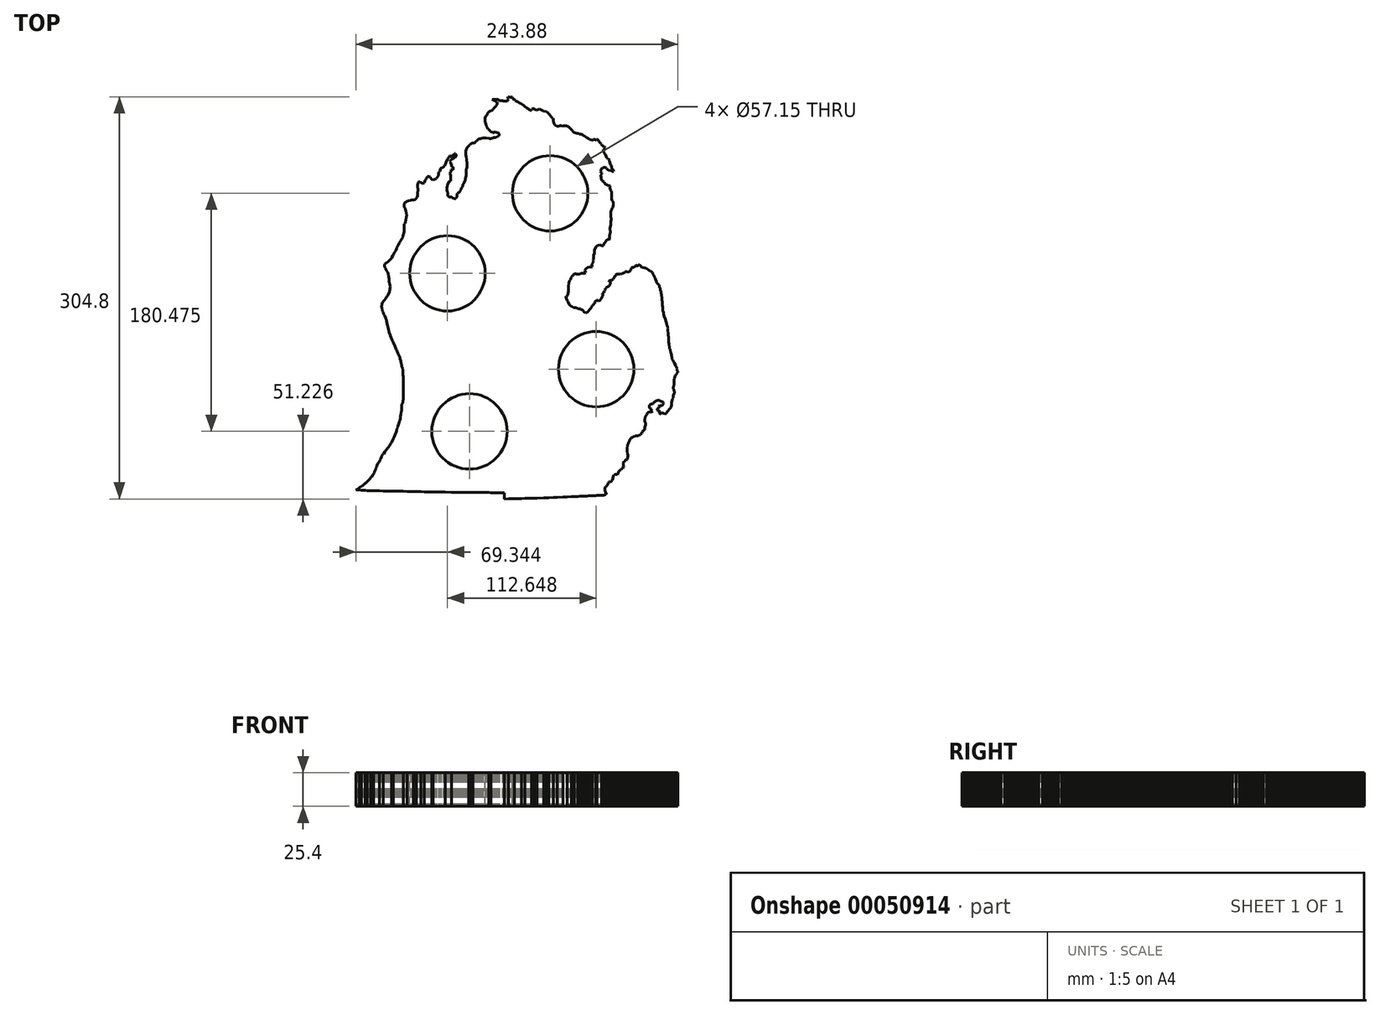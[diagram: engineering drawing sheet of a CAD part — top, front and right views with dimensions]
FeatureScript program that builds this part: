
annotation { "Feature Type Name" : "Feature", "Feature Type Description" : "" }
export const myFeature = defineFeature(function(context is Context, id is Id, definition is map)
    precondition{}
    {
        {
            var Q0;
            Q0=qCreatedBy(makeId("Top.planeOp"),FACE);
            var sketch = newSketch(context, id + "F0", { "sketchPlane" : qUnion([Q0])});
            skLineSegment(sketch, "E0", {"start": v(-98.47, -18.7) * mm, "end": v(-98.65, -17.82) * mm});
            skLineSegment(sketch, "E1", {"start": v(-98.65, -17.82) * mm, "end": v(-98.82, -17.3) * mm});
            skLineSegment(sketch, "E2", {"start": v(-98.82, -17.3) * mm, "end": v(-98.82, -16.95) * mm});
            skLineSegment(sketch, "E3", {"start": v(-98.82, -16.95) * mm, "end": v(-99.34, -15.56) * mm});
            skLineSegment(sketch, "E4", {"start": v(-99.34, -15.56) * mm, "end": v(-99.34, -15.39) * mm});
            skLineSegment(sketch, "E5", {"start": v(-99.34, -15.39) * mm, "end": v(-100.38, -13.13) * mm});
            skLineSegment(sketch, "E6", {"start": v(-100.38, -13.13) * mm, "end": v(-100.56, -12.6) * mm});
            skLineSegment(sketch, "E7", {"start": v(-100.56, -12.6) * mm, "end": v(-100.9, -12.08) * mm});
            skLineSegment(sketch, "E8", {"start": v(-100.9, -12.08) * mm, "end": v(-101.43, -10.87) * mm});
            skLineSegment(sketch, "E9", {"start": v(-101.43, -10.87) * mm, "end": v(-101.77, -9.82) * mm});
            skLineSegment(sketch, "E10", {"start": v(-101.77, -9.82) * mm, "end": v(-101.95, -9.65) * mm});
            skLineSegment(sketch, "E11", {"start": v(-101.95, -9.65) * mm, "end": v(-101.95, -9.48) * mm});
            skLineSegment(sketch, "E12", {"start": v(-101.95, -9.48) * mm, "end": v(-102.3, -7.74) * mm});
            skLineSegment(sketch, "E13", {"start": v(-102.3, -7.74) * mm, "end": v(-102.47, -6.7) * mm});
            skLineSegment(sketch, "E14", {"start": v(-102.47, -6.7) * mm, "end": v(-102.47, -6.52) * mm});
            skLineSegment(sketch, "E15", {"start": v(-102.47, -6.52) * mm, "end": v(-102.47, -6) * mm});
            skLineSegment(sketch, "E16", {"start": v(-102.47, -6) * mm, "end": v(-102.47, -5.83) * mm});
            skLineSegment(sketch, "E17", {"start": v(-102.47, -5.83) * mm, "end": v(-102.47, -5.65) * mm});
            skLineSegment(sketch, "E18", {"start": v(-102.47, -5.65) * mm, "end": v(-102.3, -5.65) * mm});
            skLineSegment(sketch, "E19", {"start": v(-102.3, -5.65) * mm, "end": v(-102.3, -4.96) * mm});
            skLineSegment(sketch, "E20", {"start": v(-102.3, -4.96) * mm, "end": v(-102.3, -4.78) * mm});
            skLineSegment(sketch, "E21", {"start": v(-102.3, -4.78) * mm, "end": v(-102.3, -4.6) * mm});
            skLineSegment(sketch, "E22", {"start": v(-102.3, -4.6) * mm, "end": v(-101.77, -3.4) * mm});
            skLineSegment(sketch, "E23", {"start": v(-101.77, -3.4) * mm, "end": v(-100.73, -1.83) * mm});
            skLineSegment(sketch, "E24", {"start": v(-100.73, -1.83) * mm, "end": v(-99, 0.09) * mm});
            skLineSegment(sketch, "E25", {"start": v(-99, 0.09) * mm, "end": v(-98.65, 0.78) * mm});
            skLineSegment(sketch, "E26", {"start": v(-98.65, 0.78) * mm, "end": v(-97.95, 1.65) * mm});
            skLineSegment(sketch, "E27", {"start": v(-97.95, 1.65) * mm, "end": v(-97.95, 1.83) * mm});
            skLineSegment(sketch, "E28", {"start": v(-97.95, 1.83) * mm, "end": v(-97.08, 3.4) * mm});
            skLineSegment(sketch, "E29", {"start": v(-97.08, 3.4) * mm, "end": v(-97.08, 3.56) * mm});
            skLineSegment(sketch, "E30", {"start": v(-97.08, 3.56) * mm, "end": v(-96.9, 3.56) * mm});
            skLineSegment(sketch, "E31", {"start": v(-96.9, 3.56) * mm, "end": v(-96.9, 3.74) * mm});
            skLineSegment(sketch, "E32", {"start": v(-96.9, 3.74) * mm, "end": v(-96.9, 3.91) * mm});
            skLineSegment(sketch, "E33", {"start": v(-96.9, 3.91) * mm, "end": v(-96.56, 4.78) * mm});
            skLineSegment(sketch, "E34", {"start": v(-96.56, 4.78) * mm, "end": v(-96.56, 4.96) * mm});
            skLineSegment(sketch, "E35", {"start": v(-96.56, 4.96) * mm, "end": v(-96.21, 6.7) * mm});
            skLineSegment(sketch, "E36", {"start": v(-96.21, 6.7) * mm, "end": v(-96.21, 6.87) * mm});
            skLineSegment(sketch, "E37", {"start": v(-96.21, 6.87) * mm, "end": v(-96.21, 7.04) * mm});
            skLineSegment(sketch, "E38", {"start": v(-96.21, 7.04) * mm, "end": v(-96.04, 8.6) * mm});
            skLineSegment(sketch, "E39", {"start": v(-96.04, 8.6) * mm, "end": v(-96.21, 9.82) * mm});
            skLineSegment(sketch, "E40", {"start": v(-96.21, 9.82) * mm, "end": v(-96.73, 12.26) * mm});
            skLineSegment(sketch, "E41", {"start": v(-96.73, 12.26) * mm, "end": v(-96.73, 12.43) * mm});
            skLineSegment(sketch, "E42", {"start": v(-96.73, 12.43) * mm, "end": v(-96.73, 13.13) * mm});
            skLineSegment(sketch, "E43", {"start": v(-96.73, 13.13) * mm, "end": v(-96.9, 14.52) * mm});
            skLineSegment(sketch, "E44", {"start": v(-96.9, 14.52) * mm, "end": v(-97.25, 16.08) * mm});
            skLineSegment(sketch, "E45", {"start": v(-97.25, 16.08) * mm, "end": v(-97.25, 16.6) * mm});
            skLineSegment(sketch, "E46", {"start": v(-97.25, 16.6) * mm, "end": v(-97.25, 16.95) * mm});
            skLineSegment(sketch, "E47", {"start": v(-97.25, 16.95) * mm, "end": v(-97.43, 17.47) * mm});
            skLineSegment(sketch, "E48", {"start": v(-97.43, 17.47) * mm, "end": v(-97.6, 18.34) * mm});
            skLineSegment(sketch, "E49", {"start": v(-97.6, 18.34) * mm, "end": v(-97.6, 18.52) * mm});
            skLineSegment(sketch, "E50", {"start": v(-97.6, 18.52) * mm, "end": v(-97.95, 19.39) * mm});
            skLineSegment(sketch, "E51", {"start": v(-97.95, 19.39) * mm, "end": v(-98.65, 20.6) * mm});
            skLineSegment(sketch, "E52", {"start": v(-98.65, 20.6) * mm, "end": v(-99.34, 22) * mm});
            skLineSegment(sketch, "E53", {"start": v(-99.34, 22) * mm, "end": v(-99.51, 22.17) * mm});
            skLineSegment(sketch, "E54", {"start": v(-99.51, 22.17) * mm, "end": v(-99.51, 22.34) * mm});
            skLineSegment(sketch, "E55", {"start": v(-99.51, 22.34) * mm, "end": v(-99.86, 22.86) * mm});
            skLineSegment(sketch, "E56", {"start": v(-99.86, 22.86) * mm, "end": v(-99.86, 23.04) * mm});
            skLineSegment(sketch, "E57", {"start": v(-99.86, 23.04) * mm, "end": v(-100.04, 23.21) * mm});
            skLineSegment(sketch, "E58", {"start": v(-100.04, 23.21) * mm, "end": v(-100.2, 24.26) * mm});
            skLineSegment(sketch, "E59", {"start": v(-100.2, 24.26) * mm, "end": v(-100.2, 24.95) * mm});
            skLineSegment(sketch, "E60", {"start": v(-100.2, 24.95) * mm, "end": v(-99.86, 25.65) * mm});
            skLineSegment(sketch, "E61", {"start": v(-99.86, 25.65) * mm, "end": v(-99.34, 26.17) * mm});
            skLineSegment(sketch, "E62", {"start": v(-99.34, 26.17) * mm, "end": v(-98.82, 26.69) * mm});
            skLineSegment(sketch, "E63", {"start": v(-98.82, 26.69) * mm, "end": v(-97.95, 27.21) * mm});
            skLineSegment(sketch, "E64", {"start": v(-97.95, 27.21) * mm, "end": v(-96.56, 28.43) * mm});
            skLineSegment(sketch, "E65", {"start": v(-96.56, 28.43) * mm, "end": v(-96.39, 28.43) * mm});
            skLineSegment(sketch, "E66", {"start": v(-96.39, 28.43) * mm, "end": v(-96.39, 28.6) * mm});
            skLineSegment(sketch, "E67", {"start": v(-96.39, 28.6) * mm, "end": v(-95.52, 29.47) * mm});
            skLineSegment(sketch, "E68", {"start": v(-95.52, 29.47) * mm, "end": v(-95, 30.17) * mm});
            skLineSegment(sketch, "E69", {"start": v(-95, 30.17) * mm, "end": v(-95, 30.34) * mm});
            skLineSegment(sketch, "E70", {"start": v(-95, 30.34) * mm, "end": v(-93.95, 32.08) * mm});
            skLineSegment(sketch, "E71", {"start": v(-93.95, 32.08) * mm, "end": v(-93.08, 33.82) * mm});
            skLineSegment(sketch, "E72", {"start": v(-93.08, 33.82) * mm, "end": v(-92.74, 34.51) * mm});
            skLineSegment(sketch, "E73", {"start": v(-92.74, 34.51) * mm, "end": v(-92.56, 34.69) * mm});
            skLineSegment(sketch, "E74", {"start": v(-92.56, 34.69) * mm, "end": v(-91.7, 35.9) * mm});
            skLineSegment(sketch, "E75", {"start": v(-91.7, 35.9) * mm, "end": v(-91.17, 37.47) * mm});
            skLineSegment(sketch, "E76", {"start": v(-91.17, 37.47) * mm, "end": v(-91, 38) * mm});
            skLineSegment(sketch, "E77", {"start": v(-91, 38) * mm, "end": v(-90.65, 39.03) * mm});
            skLineSegment(sketch, "E78", {"start": v(-90.65, 39.03) * mm, "end": v(-89.78, 39.9) * mm});
            skLineSegment(sketch, "E79", {"start": v(-89.78, 39.9) * mm, "end": v(-89.78, 40.08) * mm});
            skLineSegment(sketch, "E80", {"start": v(-89.78, 40.08) * mm, "end": v(-89.08, 41.47) * mm});
            skLineSegment(sketch, "E81", {"start": v(-89.08, 41.47) * mm, "end": v(-88.74, 42.34) * mm});
            skLineSegment(sketch, "E82", {"start": v(-88.74, 42.34) * mm, "end": v(-88.22, 43.2) * mm});
            skLineSegment(sketch, "E83", {"start": v(-88.22, 43.2) * mm, "end": v(-86.48, 45.99) * mm});
            skLineSegment(sketch, "E84", {"start": v(-86.48, 45.99) * mm, "end": v(-86.3, 46.86) * mm});
            skLineSegment(sketch, "E85", {"start": v(-86.3, 46.86) * mm, "end": v(-86.3, 47.03) * mm});
            skLineSegment(sketch, "E86", {"start": v(-86.3, 47.03) * mm, "end": v(-85.43, 50.16) * mm});
            skLineSegment(sketch, "E87", {"start": v(-85.43, 50.16) * mm, "end": v(-85.26, 51.55) * mm});
            skLineSegment(sketch, "E88", {"start": v(-85.26, 51.55) * mm, "end": v(-85.26, 52.07) * mm});
            skLineSegment(sketch, "E89", {"start": v(-85.26, 52.07) * mm, "end": v(-85.26, 52.42) * mm});
            skLineSegment(sketch, "E90", {"start": v(-85.26, 52.42) * mm, "end": v(-85.26, 52.6) * mm});
            skLineSegment(sketch, "E91", {"start": v(-85.26, 52.6) * mm, "end": v(-85.26, 52.77) * mm});
            skLineSegment(sketch, "E92", {"start": v(-85.26, 52.77) * mm, "end": v(-85.43, 53.81) * mm});
            skLineSegment(sketch, "E93", {"start": v(-85.43, 53.81) * mm, "end": v(-85.43, 54.16) * mm});
            skLineSegment(sketch, "E94", {"start": v(-85.43, 54.16) * mm, "end": v(-85.43, 54.68) * mm});
            skLineSegment(sketch, "E95", {"start": v(-85.43, 54.68) * mm, "end": v(-85.43, 54.86) * mm});
            skLineSegment(sketch, "E96", {"start": v(-85.43, 54.86) * mm, "end": v(-85.26, 55.03) * mm});
            skLineSegment(sketch, "E97", {"start": v(-85.26, 55.03) * mm, "end": v(-85.26, 55.2) * mm});
            skLineSegment(sketch, "E98", {"start": v(-85.26, 55.2) * mm, "end": v(-85.26, 56.25) * mm});
            skLineSegment(sketch, "E99", {"start": v(-85.26, 56.25) * mm, "end": v(-84.91, 56.6) * mm});
            skLineSegment(sketch, "E100", {"start": v(-84.91, 56.6) * mm, "end": v(-84.57, 57.47) * mm});
            skLineSegment(sketch, "E101", {"start": v(-84.57, 57.47) * mm, "end": v(-84.57, 57.64) * mm});
            skLineSegment(sketch, "E102", {"start": v(-84.57, 57.64) * mm, "end": v(-84.22, 58.86) * mm});
            skLineSegment(sketch, "E103", {"start": v(-84.22, 58.86) * mm, "end": v(-83.7, 61.12) * mm});
            skLineSegment(sketch, "E104", {"start": v(-83.7, 61.12) * mm, "end": v(-83.52, 62.5) * mm});
            skLineSegment(sketch, "E105", {"start": v(-83.52, 62.5) * mm, "end": v(-83.7, 64.25) * mm});
            skLineSegment(sketch, "E106", {"start": v(-83.7, 64.25) * mm, "end": v(-83.7, 64.42) * mm});
            skLineSegment(sketch, "E107", {"start": v(-83.7, 64.42) * mm, "end": v(-83.7, 64.6) * mm});
            skLineSegment(sketch, "E108", {"start": v(-83.7, 64.6) * mm, "end": v(-83.87, 64.94) * mm});
            skLineSegment(sketch, "E109", {"start": v(-83.87, 64.94) * mm, "end": v(-84.04, 65.29) * mm});
            skLineSegment(sketch, "E110", {"start": v(-84.04, 65.29) * mm, "end": v(-84.04, 65.64) * mm});
            skLineSegment(sketch, "E111", {"start": v(-84.04, 65.64) * mm, "end": v(-84.22, 65.81) * mm});
            skLineSegment(sketch, "E112", {"start": v(-84.22, 65.81) * mm, "end": v(-84.57, 67.2) * mm});
            skLineSegment(sketch, "E113", {"start": v(-84.57, 67.2) * mm, "end": v(-84.91, 67.9) * mm});
            skLineSegment(sketch, "E114", {"start": v(-84.91, 67.9) * mm, "end": v(-85.09, 68.25) * mm});
            skLineSegment(sketch, "E115", {"start": v(-85.09, 68.25) * mm, "end": v(-85.09, 68.6) * mm});
            skLineSegment(sketch, "E116", {"start": v(-85.09, 68.6) * mm, "end": v(-85.26, 69.29) * mm});
            skLineSegment(sketch, "E117", {"start": v(-85.26, 69.29) * mm, "end": v(-85.43, 69.64) * mm});
            skLineSegment(sketch, "E118", {"start": v(-85.43, 69.64) * mm, "end": v(-85.43, 69.8) * mm});
            skLineSegment(sketch, "E119", {"start": v(-85.43, 69.8) * mm, "end": v(-85.26, 70.68) * mm});
            skLineSegment(sketch, "E120", {"start": v(-85.26, 70.68) * mm, "end": v(-85.26, 71.38) * mm});
            skLineSegment(sketch, "E121", {"start": v(-85.26, 71.38) * mm, "end": v(-85.09, 71.72) * mm});
            skLineSegment(sketch, "E122", {"start": v(-85.09, 71.72) * mm, "end": v(-85.09, 71.9) * mm});
            skLineSegment(sketch, "E123", {"start": v(-85.09, 71.9) * mm, "end": v(-84.74, 72.24) * mm});
            skLineSegment(sketch, "E124", {"start": v(-84.74, 72.24) * mm, "end": v(-83.87, 72.77) * mm});
            skLineSegment(sketch, "E125", {"start": v(-83.87, 72.77) * mm, "end": v(-83.87, 72.94) * mm});
            skLineSegment(sketch, "E126", {"start": v(-83.87, 72.94) * mm, "end": v(-82.13, 73.46) * mm});
            skLineSegment(sketch, "E127", {"start": v(-82.13, 73.46) * mm, "end": v(-80.74, 73.8) * mm});
            skLineSegment(sketch, "E128", {"start": v(-80.74, 73.8) * mm, "end": v(-80.05, 74.33) * mm});
            skLineSegment(sketch, "E129", {"start": v(-80.05, 74.33) * mm, "end": v(-79.87, 74.33) * mm});
            skLineSegment(sketch, "E130", {"start": v(-79.87, 74.33) * mm, "end": v(-77.96, 74.33) * mm});
            skLineSegment(sketch, "E131", {"start": v(-77.96, 74.33) * mm, "end": v(-77.27, 74.5) * mm});
            skLineSegment(sketch, "E132", {"start": v(-77.27, 74.5) * mm, "end": v(-76.22, 75.2) * mm});
            skLineSegment(sketch, "E133", {"start": v(-76.22, 75.2) * mm, "end": v(-76.22, 75.37) * mm});
            skLineSegment(sketch, "E134", {"start": v(-76.22, 75.37) * mm, "end": v(-76.05, 75.9) * mm});
            skLineSegment(sketch, "E135", {"start": v(-76.05, 75.9) * mm, "end": v(-75.7, 76.6) * mm});
            skLineSegment(sketch, "E136", {"start": v(-75.7, 76.6) * mm, "end": v(-75.35, 77.29) * mm});
            skLineSegment(sketch, "E137", {"start": v(-75.35, 77.29) * mm, "end": v(-75.35, 77.98) * mm});
            skLineSegment(sketch, "E138", {"start": v(-75.35, 77.98) * mm, "end": v(-75.18, 79.9) * mm});
            skLineSegment(sketch, "E139", {"start": v(-75.18, 79.9) * mm, "end": v(-75, 81.11) * mm});
            skLineSegment(sketch, "E140", {"start": v(-75, 81.11) * mm, "end": v(-74.83, 81.29) * mm});
            skLineSegment(sketch, "E141", {"start": v(-74.83, 81.29) * mm, "end": v(-74.83, 81.46) * mm});
            skLineSegment(sketch, "E142", {"start": v(-74.83, 81.46) * mm, "end": v(-74.83, 82.16) * mm});
            skLineSegment(sketch, "E143", {"start": v(-74.83, 82.16) * mm, "end": v(-75.18, 84.42) * mm});
            skLineSegment(sketch, "E144", {"start": v(-75.18, 84.42) * mm, "end": v(-75.18, 85.98) * mm});
            skLineSegment(sketch, "E145", {"start": v(-75.18, 85.98) * mm, "end": v(-75, 86.68) * mm});
            skLineSegment(sketch, "E146", {"start": v(-75, 86.68) * mm, "end": v(-74.83, 87.55) * mm});
            skLineSegment(sketch, "E147", {"start": v(-74.83, 87.55) * mm, "end": v(-74.31, 87.9) * mm});
            skLineSegment(sketch, "E148", {"start": v(-74.31, 87.9) * mm, "end": v(-73.27, 88.24) * mm});
            skLineSegment(sketch, "E149", {"start": v(-73.27, 88.24) * mm, "end": v(-72.92, 87.55) * mm});
            skLineSegment(sketch, "E150", {"start": v(-72.92, 87.55) * mm, "end": v(-72.4, 87.2) * mm});
            skLineSegment(sketch, "E151", {"start": v(-72.4, 87.2) * mm, "end": v(-71.88, 87.02) * mm});
            skLineSegment(sketch, "E152", {"start": v(-71.88, 87.02) * mm, "end": v(-70.83, 87.02) * mm});
            skLineSegment(sketch, "E153", {"start": v(-70.83, 87.02) * mm, "end": v(-70.31, 87.37) * mm});
            skLineSegment(sketch, "E154", {"start": v(-70.31, 87.37) * mm, "end": v(-69.8, 88.07) * mm});
            skLineSegment(sketch, "E155", {"start": v(-69.8, 88.07) * mm, "end": v(-69.44, 89.1) * mm});
            skLineSegment(sketch, "E156", {"start": v(-69.44, 89.1) * mm, "end": v(-69.27, 89.63) * mm});
            skLineSegment(sketch, "E157", {"start": v(-69.27, 89.63) * mm, "end": v(-68.75, 89.98) * mm});
            skLineSegment(sketch, "E158", {"start": v(-68.75, 89.98) * mm, "end": v(-68.23, 90.85) * mm});
            skLineSegment(sketch, "E159", {"start": v(-68.23, 90.85) * mm, "end": v(-68.23, 91.02) * mm});
            skLineSegment(sketch, "E160", {"start": v(-68.23, 91.02) * mm, "end": v(-67.88, 91.72) * mm});
            skLineSegment(sketch, "E161", {"start": v(-67.88, 91.72) * mm, "end": v(-67.88, 91.9) * mm});
            skLineSegment(sketch, "E162", {"start": v(-67.88, 91.9) * mm, "end": v(-67.53, 92.07) * mm});
            skLineSegment(sketch, "E163", {"start": v(-67.53, 92.07) * mm, "end": v(-66.84, 92.07) * mm});
            skLineSegment(sketch, "E164", {"start": v(-66.84, 92.07) * mm, "end": v(-65.8, 91.54) * mm});
            skLineSegment(sketch, "E165", {"start": v(-65.8, 91.54) * mm, "end": v(-65.45, 91.2) * mm});
            skLineSegment(sketch, "E166", {"start": v(-65.45, 91.2) * mm, "end": v(-64.92, 90.15) * mm});
            skLineSegment(sketch, "E167", {"start": v(-64.92, 90.15) * mm, "end": v(-64.58, 89.8) * mm});
            skLineSegment(sketch, "E168", {"start": v(-64.58, 89.8) * mm, "end": v(-64.4, 89.8) * mm});
            skLineSegment(sketch, "E169", {"start": v(-64.4, 89.8) * mm, "end": v(-63.53, 89.63) * mm});
            skLineSegment(sketch, "E170", {"start": v(-63.53, 89.63) * mm, "end": v(-62.66, 89.8) * mm});
            skLineSegment(sketch, "E171", {"start": v(-62.66, 89.8) * mm, "end": v(-61.45, 90.15) * mm});
            skLineSegment(sketch, "E172", {"start": v(-61.45, 90.15) * mm, "end": v(-61.27, 90.33) * mm});
            skLineSegment(sketch, "E173", {"start": v(-61.27, 90.33) * mm, "end": v(-61.1, 90.5) * mm});
            skLineSegment(sketch, "E174", {"start": v(-61.1, 90.5) * mm, "end": v(-60.93, 90.67) * mm});
            skLineSegment(sketch, "E175", {"start": v(-60.93, 90.67) * mm, "end": v(-59.54, 92.59) * mm});
            skLineSegment(sketch, "E176", {"start": v(-59.54, 92.59) * mm, "end": v(-59.54, 92.94) * mm});
            skLineSegment(sketch, "E177", {"start": v(-59.54, 92.94) * mm, "end": v(-59.36, 94.33) * mm});
            skLineSegment(sketch, "E178", {"start": v(-59.36, 94.33) * mm, "end": v(-59.01, 95.37) * mm});
            skLineSegment(sketch, "E179", {"start": v(-59.01, 95.37) * mm, "end": v(-58.5, 95.9) * mm});
            skLineSegment(sketch, "E180", {"start": v(-58.5, 95.9) * mm, "end": v(-57.62, 97.98) * mm});
            skLineSegment(sketch, "E181", {"start": v(-57.62, 97.98) * mm, "end": v(-57.45, 98.33) * mm});
            skLineSegment(sketch, "E182", {"start": v(-57.45, 98.33) * mm, "end": v(-55.88, 99.02) * mm});
            skLineSegment(sketch, "E183", {"start": v(-55.88, 99.02) * mm, "end": v(-55.02, 99.9) * mm});
            skLineSegment(sketch, "E184", {"start": v(-55.02, 99.9) * mm, "end": v(-54.84, 100.24) * mm});
            skLineSegment(sketch, "E185", {"start": v(-54.84, 100.24) * mm, "end": v(-54.67, 100.41) * mm});
            skLineSegment(sketch, "E186", {"start": v(-54.67, 100.41) * mm, "end": v(-54.15, 101.1) * mm});
            skLineSegment(sketch, "E187", {"start": v(-54.15, 101.1) * mm, "end": v(-53.97, 101.98) * mm});
            skLineSegment(sketch, "E188", {"start": v(-53.97, 101.98) * mm, "end": v(-53.8, 102.85) * mm});
            skLineSegment(sketch, "E189", {"start": v(-53.8, 102.85) * mm, "end": v(-52.76, 104.93) * mm});
            skLineSegment(sketch, "E190", {"start": v(-52.76, 104.93) * mm, "end": v(-51.54, 106.67) * mm});
            skLineSegment(sketch, "E191", {"start": v(-51.54, 106.67) * mm, "end": v(-50.84, 107.89) * mm});
            skLineSegment(sketch, "E192", {"start": v(-50.84, 107.89) * mm, "end": v(-50.5, 107.89) * mm});
            skLineSegment(sketch, "E193", {"start": v(-50.5, 107.89) * mm, "end": v(-50.5, 107.54) * mm});
            skLineSegment(sketch, "E194", {"start": v(-50.5, 107.54) * mm, "end": v(-50.15, 107.37) * mm});
            skLineSegment(sketch, "E195", {"start": v(-50.15, 107.37) * mm, "end": v(-49.45, 107.37) * mm});
            skLineSegment(sketch, "E196", {"start": v(-49.45, 107.37) * mm, "end": v(-49.1, 107.54) * mm});
            skLineSegment(sketch, "E197", {"start": v(-49.1, 107.54) * mm, "end": v(-47.89, 108.41) * mm});
            skLineSegment(sketch, "E198", {"start": v(-47.89, 108.41) * mm, "end": v(-47.72, 108.93) * mm});
            skLineSegment(sketch, "E199", {"start": v(-47.72, 108.93) * mm, "end": v(-47.2, 109.63) * mm});
            skLineSegment(sketch, "E200", {"start": v(-47.2, 109.63) * mm, "end": v(-46.67, 109.63) * mm});
            skLineSegment(sketch, "E201", {"start": v(-46.67, 109.63) * mm, "end": v(-45.98, 108.06) * mm});
            skLineSegment(sketch, "E202", {"start": v(-45.98, 108.06) * mm, "end": v(-46.15, 107.2) * mm});
            skLineSegment(sketch, "E203", {"start": v(-46.15, 107.2) * mm, "end": v(-46.5, 106.85) * mm});
            skLineSegment(sketch, "E204", {"start": v(-46.5, 106.85) * mm, "end": v(-47.37, 106.5) * mm});
            skLineSegment(sketch, "E205", {"start": v(-47.37, 106.5) * mm, "end": v(-47.89, 105.8) * mm});
            skLineSegment(sketch, "E206", {"start": v(-47.89, 105.8) * mm, "end": v(-47.89, 105.63) * mm});
            skLineSegment(sketch, "E207", {"start": v(-47.89, 105.63) * mm, "end": v(-47.89, 105.45) * mm});
            skLineSegment(sketch, "E208", {"start": v(-47.89, 105.45) * mm, "end": v(-48.06, 105.45) * mm});
            skLineSegment(sketch, "E209", {"start": v(-48.06, 105.45) * mm, "end": v(-48.24, 105.45) * mm});
            skLineSegment(sketch, "E210", {"start": v(-48.24, 105.45) * mm, "end": v(-48.24, 105.63) * mm});
            skLineSegment(sketch, "E211", {"start": v(-48.24, 105.63) * mm, "end": v(-48.41, 105.63) * mm});
            skLineSegment(sketch, "E212", {"start": v(-48.41, 105.63) * mm, "end": v(-49.28, 105.45) * mm});
            skLineSegment(sketch, "E213", {"start": v(-49.28, 105.45) * mm, "end": v(-49.8, 105.1) * mm});
            skLineSegment(sketch, "E214", {"start": v(-49.8, 105.1) * mm, "end": v(-49.97, 104.76) * mm});
            skLineSegment(sketch, "E215", {"start": v(-49.97, 104.76) * mm, "end": v(-50.5, 104.06) * mm});
            skLineSegment(sketch, "E216", {"start": v(-50.5, 104.06) * mm, "end": v(-50.67, 103.54) * mm});
            skLineSegment(sketch, "E217", {"start": v(-50.67, 103.54) * mm, "end": v(-50.32, 102.5) * mm});
            skLineSegment(sketch, "E218", {"start": v(-50.32, 102.5) * mm, "end": v(-49.97, 101.63) * mm});
            skLineSegment(sketch, "E219", {"start": v(-49.97, 101.63) * mm, "end": v(-49.1, 99.37) * mm});
            skLineSegment(sketch, "E220", {"start": v(-49.1, 99.37) * mm, "end": v(-48.58, 99.2) * mm});
            skLineSegment(sketch, "E221", {"start": v(-48.58, 99.2) * mm, "end": v(-48.24, 98.5) * mm});
            skLineSegment(sketch, "E222", {"start": v(-48.24, 98.5) * mm, "end": v(-48.24, 97.28) * mm});
            skLineSegment(sketch, "E223", {"start": v(-48.24, 97.28) * mm, "end": v(-48.41, 97.1) * mm});
            skLineSegment(sketch, "E224", {"start": v(-48.41, 97.1) * mm, "end": v(-48.58, 97.28) * mm});
            skLineSegment(sketch, "E225", {"start": v(-48.58, 97.28) * mm, "end": v(-49.8, 97.1) * mm});
            skLineSegment(sketch, "E226", {"start": v(-49.8, 97.1) * mm, "end": v(-49.97, 95.9) * mm});
            skLineSegment(sketch, "E227", {"start": v(-49.97, 95.9) * mm, "end": v(-49.97, 95.72) * mm});
            skLineSegment(sketch, "E228", {"start": v(-49.97, 95.72) * mm, "end": v(-50.15, 95.54) * mm});
            skLineSegment(sketch, "E229", {"start": v(-50.15, 95.54) * mm, "end": v(-50.15, 95.37) * mm});
            skLineSegment(sketch, "E230", {"start": v(-50.15, 95.37) * mm, "end": v(-50.32, 95.2) * mm});
            skLineSegment(sketch, "E231", {"start": v(-50.32, 95.2) * mm, "end": v(-50.5, 95.02) * mm});
            skLineSegment(sketch, "E232", {"start": v(-50.5, 95.02) * mm, "end": v(-51.2, 94.33) * mm});
            skLineSegment(sketch, "E233", {"start": v(-51.2, 94.33) * mm, "end": v(-50.67, 93.8) * mm});
            skLineSegment(sketch, "E234", {"start": v(-50.67, 93.8) * mm, "end": v(-50.32, 93.28) * mm});
            skLineSegment(sketch, "E235", {"start": v(-50.32, 93.28) * mm, "end": v(-50.32, 93.46) * mm});
            skLineSegment(sketch, "E236", {"start": v(-50.32, 93.46) * mm, "end": v(-50.15, 92.07) * mm});
            skLineSegment(sketch, "E237", {"start": v(-50.15, 92.07) * mm, "end": v(-50.15, 90.5) * mm});
            skLineSegment(sketch, "E238", {"start": v(-50.15, 90.5) * mm, "end": v(-50.15, 88.59) * mm});
            skLineSegment(sketch, "E239", {"start": v(-50.15, 88.59) * mm, "end": v(-50.32, 88.59) * mm});
            skLineSegment(sketch, "E240", {"start": v(-50.32, 88.59) * mm, "end": v(-51.2, 88.41) * mm});
            skLineSegment(sketch, "E241", {"start": v(-51.2, 88.41) * mm, "end": v(-51.54, 88.24) * mm});
            skLineSegment(sketch, "E242", {"start": v(-51.54, 88.24) * mm, "end": v(-52.23, 85.98) * mm});
            skLineSegment(sketch, "E243", {"start": v(-52.23, 85.98) * mm, "end": v(-52.58, 85.46) * mm});
            skLineSegment(sketch, "E244", {"start": v(-52.58, 85.46) * mm, "end": v(-52.58, 85.29) * mm});
            skLineSegment(sketch, "E245", {"start": v(-52.58, 85.29) * mm, "end": v(-52.76, 84.76) * mm});
            skLineSegment(sketch, "E246", {"start": v(-52.76, 84.76) * mm, "end": v(-52.93, 83.9) * mm});
            skLineSegment(sketch, "E247", {"start": v(-52.93, 83.9) * mm, "end": v(-52.93, 83.02) * mm});
            skLineSegment(sketch, "E248", {"start": v(-52.93, 83.02) * mm, "end": v(-52.93, 82.85) * mm});
            skLineSegment(sketch, "E249", {"start": v(-52.93, 82.85) * mm, "end": v(-52.93, 81.63) * mm});
            skLineSegment(sketch, "E250", {"start": v(-52.93, 81.63) * mm, "end": v(-52.58, 80.6) * mm});
            skLineSegment(sketch, "E251", {"start": v(-52.58, 80.6) * mm, "end": v(-52.58, 80.42) * mm});
            skLineSegment(sketch, "E252", {"start": v(-52.58, 80.42) * mm, "end": v(-52.4, 80.07) * mm});
            skLineSegment(sketch, "E253", {"start": v(-52.4, 80.07) * mm, "end": v(-52.23, 78.85) * mm});
            skLineSegment(sketch, "E254", {"start": v(-52.23, 78.85) * mm, "end": v(-52.23, 78.5) * mm});
            skLineSegment(sketch, "E255", {"start": v(-52.23, 78.5) * mm, "end": v(-52.4, 77.8) * mm});
            skLineSegment(sketch, "E256", {"start": v(-52.4, 77.8) * mm, "end": v(-52.4, 77.63) * mm});
            skLineSegment(sketch, "E257", {"start": v(-52.4, 77.63) * mm, "end": v(-52.4, 77.46) * mm});
            skLineSegment(sketch, "E258", {"start": v(-52.4, 77.46) * mm, "end": v(-52.4, 77.29) * mm});
            skLineSegment(sketch, "E259", {"start": v(-52.4, 77.29) * mm, "end": v(-52.23, 77.11) * mm});
            skLineSegment(sketch, "E260", {"start": v(-52.23, 77.11) * mm, "end": v(-52.06, 76.94) * mm});
            skLineSegment(sketch, "E261", {"start": v(-52.06, 76.94) * mm, "end": v(-51.89, 76.76) * mm});
            skLineSegment(sketch, "E262", {"start": v(-51.89, 76.76) * mm, "end": v(-51.71, 76.76) * mm});
            skLineSegment(sketch, "E263", {"start": v(-51.71, 76.76) * mm, "end": v(-51.37, 76.6) * mm});
            skLineSegment(sketch, "E264", {"start": v(-51.37, 76.6) * mm, "end": v(-51.02, 76.6) * mm});
            skLineSegment(sketch, "E265", {"start": v(-51.02, 76.6) * mm, "end": v(-50.84, 76.6) * mm});
            skLineSegment(sketch, "E266", {"start": v(-50.84, 76.6) * mm, "end": v(-50.67, 76.6) * mm});
            skLineSegment(sketch, "E267", {"start": v(-50.67, 76.6) * mm, "end": v(-50.5, 76.6) * mm});
            skLineSegment(sketch, "E268", {"start": v(-50.5, 76.6) * mm, "end": v(-50.32, 76.6) * mm});
            skLineSegment(sketch, "E269", {"start": v(-50.32, 76.6) * mm, "end": v(-50.15, 76.6) * mm});
            skLineSegment(sketch, "E270", {"start": v(-50.15, 76.6) * mm, "end": v(-49.67, 76.32) * mm});
            skLineSegment(sketch, "E271", {"start": v(-49.67, 76.32) * mm, "end": v(-49.32, 76.44) * mm});
            skLineSegment(sketch, "E272", {"start": v(-49.32, 76.44) * mm, "end": v(-49.1, 76.24) * mm});
            skLineSegment(sketch, "E273", {"start": v(-49.1, 76.24) * mm, "end": v(-48.93, 76.07) * mm});
            skLineSegment(sketch, "E274", {"start": v(-48.93, 76.07) * mm, "end": v(-48.76, 75.9) * mm});
            skLineSegment(sketch, "E275", {"start": v(-48.76, 75.9) * mm, "end": v(-48.76, 75.72) * mm});
            skLineSegment(sketch, "E276", {"start": v(-48.76, 75.72) * mm, "end": v(-48.06, 75.37) * mm});
            skLineSegment(sketch, "E277", {"start": v(-48.06, 75.37) * mm, "end": v(-47.89, 75.37) * mm});
            skLineSegment(sketch, "E278", {"start": v(-47.89, 75.37) * mm, "end": v(-47.02, 75.2) * mm});
            skLineSegment(sketch, "E279", {"start": v(-47.02, 75.2) * mm, "end": v(-46.85, 75.2) * mm});
            skLineSegment(sketch, "E280", {"start": v(-46.85, 75.2) * mm, "end": v(-46.67, 75.2) * mm});
            skLineSegment(sketch, "E281", {"start": v(-46.67, 75.2) * mm, "end": v(-46.5, 75.2) * mm});
            skLineSegment(sketch, "E282", {"start": v(-46.5, 75.2) * mm, "end": v(-46.5, 75.37) * mm});
            skLineSegment(sketch, "E283", {"start": v(-46.5, 75.37) * mm, "end": v(-46.32, 75.37) * mm});
            skLineSegment(sketch, "E284", {"start": v(-46.32, 75.37) * mm, "end": v(-45.46, 76.42) * mm});
            skLineSegment(sketch, "E285", {"start": v(-45.46, 76.42) * mm, "end": v(-45.46, 76.6) * mm});
            skLineSegment(sketch, "E286", {"start": v(-45.46, 76.6) * mm, "end": v(-45.28, 76.76) * mm});
            skLineSegment(sketch, "E287", {"start": v(-45.28, 76.76) * mm, "end": v(-45.28, 76.94) * mm});
            skLineSegment(sketch, "E288", {"start": v(-45.28, 76.94) * mm, "end": v(-45.1, 77.11) * mm});
            skLineSegment(sketch, "E289", {"start": v(-45.1, 77.11) * mm, "end": v(-45.28, 77.11) * mm});
            skLineSegment(sketch, "E290", {"start": v(-45.28, 77.11) * mm, "end": v(-45.28, 77.63) * mm});
            skLineSegment(sketch, "E291", {"start": v(-45.28, 77.63) * mm, "end": v(-45.28, 77.98) * mm});
            skLineSegment(sketch, "E292", {"start": v(-45.28, 77.98) * mm, "end": v(-45.46, 78.16) * mm});
            skLineSegment(sketch, "E293", {"start": v(-45.46, 78.16) * mm, "end": v(-44.93, 79.37) * mm});
            skLineSegment(sketch, "E294", {"start": v(-44.93, 79.37) * mm, "end": v(-44.59, 79.55) * mm});
            skLineSegment(sketch, "E295", {"start": v(-44.59, 79.55) * mm, "end": v(-43.9, 79.9) * mm});
            skLineSegment(sketch, "E296", {"start": v(-43.9, 79.9) * mm, "end": v(-43.54, 80.24) * mm});
            skLineSegment(sketch, "E297", {"start": v(-43.54, 80.24) * mm, "end": v(-43.02, 80.94) * mm});
            skLineSegment(sketch, "E298", {"start": v(-43.02, 80.94) * mm, "end": v(-42.85, 81.63) * mm});
            skLineSegment(sketch, "E299", {"start": v(-42.85, 81.63) * mm, "end": v(-42.33, 82.5) * mm});
            skLineSegment(sketch, "E300", {"start": v(-42.33, 82.5) * mm, "end": v(-41.8, 83.55) * mm});
            skLineSegment(sketch, "E301", {"start": v(-41.8, 83.55) * mm, "end": v(-41.63, 83.72) * mm});
            skLineSegment(sketch, "E302", {"start": v(-41.63, 83.72) * mm, "end": v(-40.94, 85.11) * mm});
            skLineSegment(sketch, "E303", {"start": v(-40.94, 85.11) * mm, "end": v(-40.94, 85.46) * mm});
            skLineSegment(sketch, "E304", {"start": v(-40.94, 85.46) * mm, "end": v(-40.94, 85.63) * mm});
            skLineSegment(sketch, "E305", {"start": v(-40.94, 85.63) * mm, "end": v(-40.76, 86.15) * mm});
            skLineSegment(sketch, "E306", {"start": v(-40.76, 86.15) * mm, "end": v(-40.59, 86.33) * mm});
            skLineSegment(sketch, "E307", {"start": v(-40.59, 86.33) * mm, "end": v(-40.41, 86.5) * mm});
            skLineSegment(sketch, "E308", {"start": v(-40.41, 86.5) * mm, "end": v(-40.24, 86.85) * mm});
            skLineSegment(sketch, "E309", {"start": v(-40.24, 86.85) * mm, "end": v(-39.9, 87.37) * mm});
            skLineSegment(sketch, "E310", {"start": v(-39.9, 87.37) * mm, "end": v(-39.37, 88.76) * mm});
            skLineSegment(sketch, "E311", {"start": v(-39.37, 88.76) * mm, "end": v(-39.2, 89.46) * mm});
            skLineSegment(sketch, "E312", {"start": v(-39.2, 89.46) * mm, "end": v(-39.02, 89.98) * mm});
            skLineSegment(sketch, "E313", {"start": v(-39.02, 89.98) * mm, "end": v(-38.5, 93.1) * mm});
            skLineSegment(sketch, "E314", {"start": v(-38.5, 93.1) * mm, "end": v(-38.33, 93.8) * mm});
            skLineSegment(sketch, "E315", {"start": v(-38.33, 93.8) * mm, "end": v(-38.5, 95.2) * mm});
            skLineSegment(sketch, "E316", {"start": v(-38.5, 95.2) * mm, "end": v(-38.5, 95.37) * mm});
            skLineSegment(sketch, "E317", {"start": v(-38.5, 95.37) * mm, "end": v(-38.33, 97.28) * mm});
            skLineSegment(sketch, "E318", {"start": v(-38.33, 97.28) * mm, "end": v(-38.33, 97.46) * mm});
            skLineSegment(sketch, "E319", {"start": v(-38.33, 97.46) * mm, "end": v(-38.15, 97.98) * mm});
            skLineSegment(sketch, "E320", {"start": v(-38.15, 97.98) * mm, "end": v(-37.63, 99.02) * mm});
            skLineSegment(sketch, "E321", {"start": v(-37.63, 99.02) * mm, "end": v(-37.63, 100.24) * mm});
            skLineSegment(sketch, "E322", {"start": v(-37.63, 100.24) * mm, "end": v(-37.63, 102.67) * mm});
            skLineSegment(sketch, "E323", {"start": v(-37.63, 102.67) * mm, "end": v(-37.8, 103.02) * mm});
            skLineSegment(sketch, "E324", {"start": v(-37.8, 103.02) * mm, "end": v(-37.98, 103.37) * mm});
            skLineSegment(sketch, "E325", {"start": v(-37.98, 103.37) * mm, "end": v(-37.98, 103.54) * mm});
            skLineSegment(sketch, "E326", {"start": v(-37.98, 103.54) * mm, "end": v(-38.15, 104.58) * mm});
            skLineSegment(sketch, "E327", {"start": v(-38.15, 104.58) * mm, "end": v(-38.33, 107.37) * mm});
            skLineSegment(sketch, "E328", {"start": v(-38.33, 107.37) * mm, "end": v(-38.68, 108.06) * mm});
            skLineSegment(sketch, "E329", {"start": v(-38.68, 108.06) * mm, "end": v(-38.68, 109.28) * mm});
            skLineSegment(sketch, "E330", {"start": v(-38.68, 109.28) * mm, "end": v(-38.68, 111.37) * mm});
            skLineSegment(sketch, "E331", {"start": v(-38.68, 111.37) * mm, "end": v(-37.63, 113.97) * mm});
            skLineSegment(sketch, "E332", {"start": v(-37.63, 113.97) * mm, "end": v(-36.94, 114.84) * mm});
            skLineSegment(sketch, "E333", {"start": v(-36.94, 114.84) * mm, "end": v(-35.9, 115.71) * mm});
            skLineSegment(sketch, "E334", {"start": v(-35.9, 115.71) * mm, "end": v(-35.72, 115.71) * mm});
            skLineSegment(sketch, "E335", {"start": v(-35.72, 115.71) * mm, "end": v(-35.2, 116.4) * mm});
            skLineSegment(sketch, "E336", {"start": v(-35.2, 116.4) * mm, "end": v(-34.85, 116.76) * mm});
            skLineSegment(sketch, "E337", {"start": v(-34.85, 116.76) * mm, "end": v(-34.33, 117.1) * mm});
            skLineSegment(sketch, "E338", {"start": v(-34.33, 117.1) * mm, "end": v(-33.64, 117.45) * mm});
            skLineSegment(sketch, "E339", {"start": v(-33.64, 117.45) * mm, "end": v(-33.29, 117.28) * mm});
            skLineSegment(sketch, "E340", {"start": v(-33.29, 117.28) * mm, "end": v(-32.6, 117.28) * mm});
            skLineSegment(sketch, "E341", {"start": v(-32.6, 117.28) * mm, "end": v(-32.42, 117.45) * mm});
            skLineSegment(sketch, "E342", {"start": v(-32.42, 117.45) * mm, "end": v(-32.25, 117.45) * mm});
            skLineSegment(sketch, "E343", {"start": v(-32.25, 117.45) * mm, "end": v(-31.9, 117.63) * mm});
            skLineSegment(sketch, "E344", {"start": v(-31.9, 117.63) * mm, "end": v(-31.55, 117.97) * mm});
            skLineSegment(sketch, "E345", {"start": v(-31.55, 117.97) * mm, "end": v(-31.55, 118.15) * mm});
            skLineSegment(sketch, "E346", {"start": v(-31.55, 118.15) * mm, "end": v(-31.38, 118.5) * mm});
            skLineSegment(sketch, "E347", {"start": v(-31.38, 118.5) * mm, "end": v(-30.5, 119.02) * mm});
            skLineSegment(sketch, "E348", {"start": v(-30.5, 119.02) * mm, "end": v(-29.64, 119.89) * mm});
            skLineSegment(sketch, "E349", {"start": v(-29.64, 119.89) * mm, "end": v(-29.12, 120.4) * mm});
            skLineSegment(sketch, "E350", {"start": v(-29.12, 120.4) * mm, "end": v(-28.42, 120.58) * mm});
            skLineSegment(sketch, "E351", {"start": v(-28.42, 120.58) * mm, "end": v(-27.73, 120.58) * mm});
            skLineSegment(sketch, "E352", {"start": v(-27.73, 120.58) * mm, "end": v(-27.03, 120.93) * mm});
            skLineSegment(sketch, "E353", {"start": v(-27.03, 120.93) * mm, "end": v(-25.64, 121.28) * mm});
            skLineSegment(sketch, "E354", {"start": v(-25.64, 121.28) * mm, "end": v(-23.2, 121.1) * mm});
            skLineSegment(sketch, "E355", {"start": v(-23.2, 121.1) * mm, "end": v(-20.95, 120.75) * mm});
            skLineSegment(sketch, "E356", {"start": v(-20.95, 120.75) * mm, "end": v(-20.42, 120.58) * mm});
            skLineSegment(sketch, "E357", {"start": v(-20.42, 120.58) * mm, "end": v(-19.9, 120.58) * mm});
            skLineSegment(sketch, "E358", {"start": v(-19.9, 120.58) * mm, "end": v(-19.38, 120.93) * mm});
            skLineSegment(sketch, "E359", {"start": v(-19.38, 120.93) * mm, "end": v(-18.16, 121.28) * mm});
            skLineSegment(sketch, "E360", {"start": v(-18.16, 121.28) * mm, "end": v(-18, 121.28) * mm});
            skLineSegment(sketch, "E361", {"start": v(-18, 121.28) * mm, "end": v(-17.3, 121.45) * mm});
            skLineSegment(sketch, "E362", {"start": v(-17.3, 121.45) * mm, "end": v(-16.77, 121.45) * mm});
            skLineSegment(sketch, "E363", {"start": v(-16.77, 121.45) * mm, "end": v(-16.08, 121.62) * mm});
            skLineSegment(sketch, "E364", {"start": v(-16.08, 121.62) * mm, "end": v(-15.9, 121.62) * mm});
            skLineSegment(sketch, "E365", {"start": v(-15.9, 121.62) * mm, "end": v(-15.04, 122.15) * mm});
            skLineSegment(sketch, "E366", {"start": v(-15.04, 122.15) * mm, "end": v(-13.82, 122.84) * mm});
            skLineSegment(sketch, "E367", {"start": v(-13.82, 122.84) * mm, "end": v(-13.65, 122.84) * mm});
            skLineSegment(sketch, "E368", {"start": v(-13.65, 122.84) * mm, "end": v(-13.65, 123.02) * mm});
            skLineSegment(sketch, "E369", {"start": v(-13.65, 123.02) * mm, "end": v(-13.47, 123.54) * mm});
            skLineSegment(sketch, "E370", {"start": v(-13.47, 123.54) * mm, "end": v(-13.47, 123.71) * mm});
            skLineSegment(sketch, "E371", {"start": v(-13.47, 123.71) * mm, "end": v(-13.47, 123.88) * mm});
            skLineSegment(sketch, "E372", {"start": v(-13.47, 123.88) * mm, "end": v(-13.47, 124.23) * mm});
            skLineSegment(sketch, "E373", {"start": v(-13.47, 124.23) * mm, "end": v(-13.65, 124.23) * mm});
            skLineSegment(sketch, "E374", {"start": v(-13.65, 124.23) * mm, "end": v(-13.65, 124.4) * mm});
            skLineSegment(sketch, "E375", {"start": v(-13.65, 124.4) * mm, "end": v(-13.65, 124.75) * mm});
            skLineSegment(sketch, "E376", {"start": v(-13.65, 124.75) * mm, "end": v(-14, 125.1) * mm});
            skLineSegment(sketch, "E377", {"start": v(-14, 125.1) * mm, "end": v(-16.6, 125.62) * mm});
            skLineSegment(sketch, "E378", {"start": v(-16.6, 125.62) * mm, "end": v(-17.12, 125.62) * mm});
            skLineSegment(sketch, "E379", {"start": v(-17.12, 125.62) * mm, "end": v(-17.64, 125.45) * mm});
            skLineSegment(sketch, "E380", {"start": v(-17.64, 125.45) * mm, "end": v(-17.64, 125.28) * mm});
            skLineSegment(sketch, "E381", {"start": v(-17.64, 125.28) * mm, "end": v(-17.3, 124.93) * mm});
            skLineSegment(sketch, "E382", {"start": v(-17.3, 124.93) * mm, "end": v(-16.95, 124.93) * mm});
            skLineSegment(sketch, "E383", {"start": v(-16.95, 124.93) * mm, "end": v(-17.82, 125.1) * mm});
            skLineSegment(sketch, "E384", {"start": v(-17.82, 125.1) * mm, "end": v(-17.82, 125.28) * mm});
            skLineSegment(sketch, "E385", {"start": v(-17.82, 125.28) * mm, "end": v(-18.86, 125.62) * mm});
            skLineSegment(sketch, "E386", {"start": v(-18.86, 125.62) * mm, "end": v(-19.9, 126.14) * mm});
            skLineSegment(sketch, "E387", {"start": v(-19.9, 126.14) * mm, "end": v(-20.25, 126.14) * mm});
            skLineSegment(sketch, "E388", {"start": v(-20.25, 126.14) * mm, "end": v(-20.42, 126.5) * mm});
            skLineSegment(sketch, "E389", {"start": v(-20.42, 126.5) * mm, "end": v(-20.95, 127.19) * mm});
            skLineSegment(sketch, "E390", {"start": v(-20.95, 127.19) * mm, "end": v(-21.64, 127.88) * mm});
            skLineSegment(sketch, "E391", {"start": v(-21.64, 127.88) * mm, "end": v(-21.82, 127.88) * mm});
            skLineSegment(sketch, "E392", {"start": v(-21.82, 127.88) * mm, "end": v(-22.68, 129.27) * mm});
            skLineSegment(sketch, "E393", {"start": v(-22.68, 129.27) * mm, "end": v(-22.68, 129.45) * mm});
            skLineSegment(sketch, "E394", {"start": v(-22.68, 129.45) * mm, "end": v(-23.03, 130.5) * mm});
            skLineSegment(sketch, "E395", {"start": v(-23.03, 130.5) * mm, "end": v(-23.55, 131.7) * mm});
            skLineSegment(sketch, "E396", {"start": v(-23.55, 131.7) * mm, "end": v(-23.73, 132.58) * mm});
            skLineSegment(sketch, "E397", {"start": v(-23.73, 132.58) * mm, "end": v(-23.73, 132.75) * mm});
            skLineSegment(sketch, "E398", {"start": v(-23.73, 132.75) * mm, "end": v(-24.07, 133.97) * mm});
            skLineSegment(sketch, "E399", {"start": v(-24.07, 133.97) * mm, "end": v(-24.07, 134.66) * mm});
            skLineSegment(sketch, "E400", {"start": v(-24.07, 134.66) * mm, "end": v(-24.25, 136.06) * mm});
            skLineSegment(sketch, "E401", {"start": v(-24.25, 136.06) * mm, "end": v(-24.25, 136.58) * mm});
            skLineSegment(sketch, "E402", {"start": v(-24.25, 136.58) * mm, "end": v(-23.9, 137.27) * mm});
            skLineSegment(sketch, "E403", {"start": v(-23.9, 137.27) * mm, "end": v(-22.86, 138.49) * mm});
            skLineSegment(sketch, "E404", {"start": v(-22.86, 138.49) * mm, "end": v(-22.16, 139.7) * mm});
            skLineSegment(sketch, "E405", {"start": v(-22.16, 139.7) * mm, "end": v(-21.99, 140.05) * mm});
            skLineSegment(sketch, "E406", {"start": v(-21.99, 140.05) * mm, "end": v(-21.99, 140.23) * mm});
            skLineSegment(sketch, "E407", {"start": v(-21.99, 140.23) * mm, "end": v(-21.82, 140.58) * mm});
            skLineSegment(sketch, "E408", {"start": v(-21.82, 140.58) * mm, "end": v(-21.12, 141.27) * mm});
            skLineSegment(sketch, "E409", {"start": v(-21.12, 141.27) * mm, "end": v(-20.25, 141.62) * mm});
            skLineSegment(sketch, "E410", {"start": v(-20.25, 141.62) * mm, "end": v(-18.86, 142.14) * mm});
            skLineSegment(sketch, "E411", {"start": v(-18.86, 142.14) * mm, "end": v(-18.69, 142.14) * mm});
            skLineSegment(sketch, "E412", {"start": v(-18.69, 142.14) * mm, "end": v(-18.69, 142.32) * mm});
            skLineSegment(sketch, "E413", {"start": v(-18.69, 142.32) * mm, "end": v(-18.34, 142.49) * mm});
            skLineSegment(sketch, "E414", {"start": v(-18.34, 142.49) * mm, "end": v(-18, 142.84) * mm});
            skLineSegment(sketch, "E415", {"start": v(-18, 142.84) * mm, "end": v(-17.82, 143.53) * mm});
            skLineSegment(sketch, "E416", {"start": v(-17.82, 143.53) * mm, "end": v(-16.77, 144.4) * mm});
            skLineSegment(sketch, "E417", {"start": v(-16.77, 144.4) * mm, "end": v(-16.6, 144.58) * mm});
            skLineSegment(sketch, "E418", {"start": v(-16.6, 144.58) * mm, "end": v(-16.43, 144.75) * mm});
            skLineSegment(sketch, "E419", {"start": v(-16.43, 144.75) * mm, "end": v(-15.04, 146.49) * mm});
            skLineSegment(sketch, "E420", {"start": v(-15.04, 146.49) * mm, "end": v(-15.04, 146.66) * mm});
            skLineSegment(sketch, "E421", {"start": v(-15.04, 146.66) * mm, "end": v(-14.86, 147.36) * mm});
            skLineSegment(sketch, "E422", {"start": v(-14.86, 147.36) * mm, "end": v(-14.86, 147.88) * mm});
            skLineSegment(sketch, "E423", {"start": v(-14.86, 147.88) * mm, "end": v(-15.38, 148.57) * mm});
            skLineSegment(sketch, "E424", {"start": v(-15.38, 148.57) * mm, "end": v(-15.73, 148.75) * mm});
            skLineSegment(sketch, "E425", {"start": v(-15.73, 148.75) * mm, "end": v(-16.25, 149.1) * mm});
            skLineSegment(sketch, "E426", {"start": v(-16.25, 149.1) * mm, "end": v(-16.95, 149.62) * mm});
            skLineSegment(sketch, "E427", {"start": v(-16.95, 149.62) * mm, "end": v(-17.3, 149.8) * mm});
            skLineSegment(sketch, "E428", {"start": v(-17.3, 149.8) * mm, "end": v(-17.64, 149.8) * mm});
            skLineSegment(sketch, "E429", {"start": v(-17.64, 149.8) * mm, "end": v(-18, 149.8) * mm});
            skLineSegment(sketch, "E430", {"start": v(-18, 149.8) * mm, "end": v(-18.51, 150.14) * mm});
            skLineSegment(sketch, "E431", {"start": v(-18.51, 150.14) * mm, "end": v(-18.69, 150.31) * mm});
            skLineSegment(sketch, "E432", {"start": v(-18.69, 150.31) * mm, "end": v(-18.34, 150.49) * mm});
            skLineSegment(sketch, "E433", {"start": v(-18.34, 150.49) * mm, "end": v(-17.64, 150.31) * mm});
            skLineSegment(sketch, "E434", {"start": v(-17.64, 150.31) * mm, "end": v(-14.69, 150.31) * mm});
            skLineSegment(sketch, "E435", {"start": v(-14.69, 150.31) * mm, "end": v(-14, 149.97) * mm});
            skLineSegment(sketch, "E436", {"start": v(-14, 149.97) * mm, "end": v(-13.3, 149.44) * mm});
            skLineSegment(sketch, "E437", {"start": v(-13.3, 149.44) * mm, "end": v(-11.04, 149.62) * mm});
            skLineSegment(sketch, "E438", {"start": v(-11.04, 149.62) * mm, "end": v(-10.7, 149.62) * mm});
            skLineSegment(sketch, "E439", {"start": v(-10.7, 149.62) * mm, "end": v(-10.52, 149.44) * mm});
            skLineSegment(sketch, "E440", {"start": v(-10.52, 149.44) * mm, "end": v(-10.34, 149.27) * mm});
            skLineSegment(sketch, "E441", {"start": v(-10.34, 149.27) * mm, "end": v(-9.65, 149.1) * mm});
            skLineSegment(sketch, "E442", {"start": v(-9.65, 149.1) * mm, "end": v(-7.9, 149.1) * mm});
            skLineSegment(sketch, "E443", {"start": v(-7.9, 149.1) * mm, "end": v(-7.39, 149.27) * mm});
            skLineSegment(sketch, "E444", {"start": v(-7.39, 149.27) * mm, "end": v(-7.04, 149.62) * mm});
            skLineSegment(sketch, "E445", {"start": v(-7.04, 149.62) * mm, "end": v(-6.87, 149.62) * mm});
            skLineSegment(sketch, "E446", {"start": v(-6.87, 149.62) * mm, "end": v(-6.52, 150.31) * mm});
            skLineSegment(sketch, "E447", {"start": v(-6.52, 150.31) * mm, "end": v(-6.34, 150.84) * mm});
            skLineSegment(sketch, "E448", {"start": v(-6.34, 150.84) * mm, "end": v(-6.52, 151) * mm});
            skLineSegment(sketch, "E449", {"start": v(-6.52, 151) * mm, "end": v(-6.87, 151.36) * mm});
            skLineSegment(sketch, "E450", {"start": v(-6.87, 151.36) * mm, "end": v(-7.04, 151.53) * mm});
            skLineSegment(sketch, "E451", {"start": v(-7.04, 151.53) * mm, "end": v(-7.04, 151.7) * mm});
            skLineSegment(sketch, "E452", {"start": v(-7.04, 151.7) * mm, "end": v(-6.52, 152.23) * mm});
            skLineSegment(sketch, "E453", {"start": v(-6.52, 152.23) * mm, "end": v(-6.34, 152.23) * mm});
            skLineSegment(sketch, "E454", {"start": v(-6.34, 152.23) * mm, "end": v(-6.17, 152.4) * mm});
            skLineSegment(sketch, "E455", {"start": v(-6.17, 152.4) * mm, "end": v(-6, 152.4) * mm});
            skLineSegment(sketch, "E456", {"start": v(-6, 152.4) * mm, "end": v(-4.95, 151.88) * mm});
            skLineSegment(sketch, "E457", {"start": v(-4.95, 151.88) * mm, "end": v(-4.43, 152.05) * mm});
            skLineSegment(sketch, "E458", {"start": v(-4.43, 152.05) * mm, "end": v(-4.08, 152.23) * mm});
            skLineSegment(sketch, "E459", {"start": v(-4.08, 152.23) * mm, "end": v(-3.91, 152.23) * mm});
            skLineSegment(sketch, "E460", {"start": v(-3.91, 152.23) * mm, "end": v(-3.56, 152.23) * mm});
            skLineSegment(sketch, "E461", {"start": v(-3.56, 152.23) * mm, "end": v(-3.56, 151.88) * mm});
            skLineSegment(sketch, "E462", {"start": v(-3.56, 151.88) * mm, "end": v(-3.22, 151.53) * mm});
            skLineSegment(sketch, "E463", {"start": v(-3.22, 151.53) * mm, "end": v(-3.04, 150.66) * mm});
            skLineSegment(sketch, "E464", {"start": v(-3.04, 150.66) * mm, "end": v(-1.3, 149.97) * mm});
            skLineSegment(sketch, "E465", {"start": v(-1.3, 149.97) * mm, "end": v(-1.3, 149.62) * mm});
            skLineSegment(sketch, "E466", {"start": v(-1.3, 149.62) * mm, "end": v(-1.13, 149.44) * mm});
            skLineSegment(sketch, "E467", {"start": v(-1.13, 149.44) * mm, "end": v(-0.09, 148.92) * mm});
            skLineSegment(sketch, "E468", {"start": v(-0.09, 148.92) * mm, "end": v(0.6, 148.75) * mm});
            skLineSegment(sketch, "E469", {"start": v(0.6, 148.75) * mm, "end": v(2, 147.7) * mm});
            skLineSegment(sketch, "E470", {"start": v(2, 147.7) * mm, "end": v(2.52, 147.53) * mm});
            skLineSegment(sketch, "E471", {"start": v(2.52, 147.53) * mm, "end": v(2.7, 147.36) * mm});
            skLineSegment(sketch, "E472", {"start": v(2.7, 147.36) * mm, "end": v(2.87, 147.18) * mm});
            skLineSegment(sketch, "E473", {"start": v(2.87, 147.18) * mm, "end": v(3.04, 147.18) * mm});
            skLineSegment(sketch, "E474", {"start": v(3.04, 147.18) * mm, "end": v(4.26, 146.49) * mm});
            skLineSegment(sketch, "E475", {"start": v(4.26, 146.49) * mm, "end": v(5.3, 145.8) * mm});
            skLineSegment(sketch, "E476", {"start": v(5.3, 145.8) * mm, "end": v(5.3, 145.62) * mm});
            skLineSegment(sketch, "E477", {"start": v(5.3, 145.62) * mm, "end": v(5.65, 145.27) * mm});
            skLineSegment(sketch, "E478", {"start": v(5.65, 145.27) * mm, "end": v(6.17, 144.92) * mm});
            skLineSegment(sketch, "E479", {"start": v(6.17, 144.92) * mm, "end": v(6.52, 144.58) * mm});
            skLineSegment(sketch, "E480", {"start": v(6.52, 144.58) * mm, "end": v(7.21, 144.23) * mm});
            skLineSegment(sketch, "E481", {"start": v(7.21, 144.23) * mm, "end": v(7.9, 143.7) * mm});
            skLineSegment(sketch, "E482", {"start": v(7.9, 143.7) * mm, "end": v(8.26, 143.53) * mm});
            skLineSegment(sketch, "E483", {"start": v(8.26, 143.53) * mm, "end": v(8.95, 143.01) * mm});
            skLineSegment(sketch, "E484", {"start": v(8.95, 143.01) * mm, "end": v(9.13, 142.84) * mm});
            skLineSegment(sketch, "E485", {"start": v(9.13, 142.84) * mm, "end": v(9.82, 142.32) * mm});
            skLineSegment(sketch, "E486", {"start": v(9.82, 142.32) * mm, "end": v(10, 142.32) * mm});
            skLineSegment(sketch, "E487", {"start": v(10, 142.32) * mm, "end": v(10, 142.14) * mm});
            skLineSegment(sketch, "E488", {"start": v(10, 142.14) * mm, "end": v(10.17, 142.14) * mm});
            skLineSegment(sketch, "E489", {"start": v(10.17, 142.14) * mm, "end": v(10.7, 142.32) * mm});
            skLineSegment(sketch, "E490", {"start": v(10.7, 142.32) * mm, "end": v(11.21, 142.32) * mm});
            skLineSegment(sketch, "E491", {"start": v(11.21, 142.32) * mm, "end": v(11.56, 143.01) * mm});
            skLineSegment(sketch, "E492", {"start": v(11.56, 143.01) * mm, "end": v(11.9, 143.36) * mm});
            skLineSegment(sketch, "E493", {"start": v(11.9, 143.36) * mm, "end": v(12.6, 143.36) * mm});
            skLineSegment(sketch, "E494", {"start": v(12.6, 143.36) * mm, "end": v(13.3, 143.01) * mm});
            skLineSegment(sketch, "E495", {"start": v(13.3, 143.01) * mm, "end": v(13.47, 142.84) * mm});
            skLineSegment(sketch, "E496", {"start": v(13.47, 142.84) * mm, "end": v(13.64, 142.84) * mm});
            skLineSegment(sketch, "E497", {"start": v(13.64, 142.84) * mm, "end": v(13.82, 142.66) * mm});
            skLineSegment(sketch, "E498", {"start": v(13.82, 142.66) * mm, "end": v(14.34, 142.49) * mm});
            skLineSegment(sketch, "E499", {"start": v(14.34, 142.49) * mm, "end": v(14.51, 142.32) * mm});
            skLineSegment(sketch, "E500", {"start": v(14.51, 142.32) * mm, "end": v(16.08, 142.84) * mm});
            skLineSegment(sketch, "E501", {"start": v(16.08, 142.84) * mm, "end": v(17.12, 143.01) * mm});
            skLineSegment(sketch, "E502", {"start": v(17.12, 143.01) * mm, "end": v(18.34, 142.49) * mm});
            skLineSegment(sketch, "E503", {"start": v(18.34, 142.49) * mm, "end": v(19.03, 142.14) * mm});
            skLineSegment(sketch, "E504", {"start": v(19.03, 142.14) * mm, "end": v(19.2, 142.14) * mm});
            skLineSegment(sketch, "E505", {"start": v(19.2, 142.14) * mm, "end": v(19.56, 141.97) * mm});
            skLineSegment(sketch, "E506", {"start": v(19.56, 141.97) * mm, "end": v(20.08, 141.62) * mm});
            skLineSegment(sketch, "E507", {"start": v(20.08, 141.62) * mm, "end": v(22.34, 141.1) * mm});
            skLineSegment(sketch, "E508", {"start": v(22.34, 141.1) * mm, "end": v(23.03, 140.75) * mm});
            skLineSegment(sketch, "E509", {"start": v(23.03, 140.75) * mm, "end": v(23.55, 140.23) * mm});
            skLineSegment(sketch, "E510", {"start": v(23.55, 140.23) * mm, "end": v(24.07, 139.88) * mm});
            skLineSegment(sketch, "E511", {"start": v(24.07, 139.88) * mm, "end": v(24.77, 138.66) * mm});
            skLineSegment(sketch, "E512", {"start": v(24.77, 138.66) * mm, "end": v(24.94, 138.49) * mm});
            skLineSegment(sketch, "E513", {"start": v(24.94, 138.49) * mm, "end": v(25.64, 137.62) * mm});
            skLineSegment(sketch, "E514", {"start": v(25.64, 137.62) * mm, "end": v(25.99, 137.1) * mm});
            skLineSegment(sketch, "E515", {"start": v(25.99, 137.1) * mm, "end": v(27.03, 136.23) * mm});
            skLineSegment(sketch, "E516", {"start": v(27.03, 136.23) * mm, "end": v(27.2, 136.06) * mm});
            skLineSegment(sketch, "E517", {"start": v(27.2, 136.06) * mm, "end": v(27.55, 135.36) * mm});
            skLineSegment(sketch, "E518", {"start": v(27.55, 135.36) * mm, "end": v(27.73, 135.01) * mm});
            skLineSegment(sketch, "E519", {"start": v(27.73, 135.01) * mm, "end": v(27.73, 134.14) * mm});
            skLineSegment(sketch, "E520", {"start": v(27.73, 134.14) * mm, "end": v(27.55, 133.97) * mm});
            skLineSegment(sketch, "E521", {"start": v(27.55, 133.97) * mm, "end": v(27.73, 133.8) * mm});
            skLineSegment(sketch, "E522", {"start": v(27.73, 133.8) * mm, "end": v(27.9, 132.58) * mm});
            skLineSegment(sketch, "E523", {"start": v(27.9, 132.58) * mm, "end": v(28.25, 131.88) * mm});
            skLineSegment(sketch, "E524", {"start": v(28.25, 131.88) * mm, "end": v(28.25, 131.7) * mm});
            skLineSegment(sketch, "E525", {"start": v(28.25, 131.7) * mm, "end": v(28.6, 131.36) * mm});
            skLineSegment(sketch, "E526", {"start": v(28.6, 131.36) * mm, "end": v(28.6, 131.19) * mm});
            skLineSegment(sketch, "E527", {"start": v(28.6, 131.19) * mm, "end": v(28.77, 131.01) * mm});
            skLineSegment(sketch, "E528", {"start": v(28.77, 131.01) * mm, "end": v(29.29, 130.67) * mm});
            skLineSegment(sketch, "E529", {"start": v(29.29, 130.67) * mm, "end": v(30.16, 130.14) * mm});
            skLineSegment(sketch, "E530", {"start": v(30.16, 130.14) * mm, "end": v(30.33, 130.14) * mm});
            skLineSegment(sketch, "E531", {"start": v(30.33, 130.14) * mm, "end": v(30.5, 130.14) * mm});
            skLineSegment(sketch, "E532", {"start": v(30.5, 130.14) * mm, "end": v(31.2, 129.97) * mm});
            skLineSegment(sketch, "E533", {"start": v(31.2, 129.97) * mm, "end": v(31.38, 129.97) * mm});
            skLineSegment(sketch, "E534", {"start": v(31.38, 129.97) * mm, "end": v(32.24, 130.32) * mm});
            skLineSegment(sketch, "E535", {"start": v(32.24, 130.32) * mm, "end": v(32.42, 130.5) * mm});
            skLineSegment(sketch, "E536", {"start": v(32.42, 130.5) * mm, "end": v(32.77, 130.67) * mm});
            skLineSegment(sketch, "E537", {"start": v(32.77, 130.67) * mm, "end": v(32.94, 130.67) * mm});
            skLineSegment(sketch, "E538", {"start": v(32.94, 130.67) * mm, "end": v(33.29, 130.5) * mm});
            skLineSegment(sketch, "E539", {"start": v(33.29, 130.5) * mm, "end": v(33.8, 130.5) * mm});
            skLineSegment(sketch, "E540", {"start": v(33.8, 130.5) * mm, "end": v(34.33, 130.14) * mm});
            skLineSegment(sketch, "E541", {"start": v(34.33, 130.14) * mm, "end": v(35.2, 130.32) * mm});
            skLineSegment(sketch, "E542", {"start": v(35.2, 130.32) * mm, "end": v(35.37, 130.32) * mm});
            skLineSegment(sketch, "E543", {"start": v(35.37, 130.32) * mm, "end": v(36.07, 130.32) * mm});
            skLineSegment(sketch, "E544", {"start": v(36.07, 130.32) * mm, "end": v(36.42, 130.32) * mm});
            skLineSegment(sketch, "E545", {"start": v(36.42, 130.32) * mm, "end": v(37.46, 130.32) * mm});
            skLineSegment(sketch, "E546", {"start": v(37.46, 130.32) * mm, "end": v(37.98, 130.14) * mm});
            skLineSegment(sketch, "E547", {"start": v(37.98, 130.14) * mm, "end": v(38.68, 129.97) * mm});
            skLineSegment(sketch, "E548", {"start": v(38.68, 129.97) * mm, "end": v(39.02, 129.8) * mm});
            skLineSegment(sketch, "E549", {"start": v(39.02, 129.8) * mm, "end": v(40.41, 128.4) * mm});
            skLineSegment(sketch, "E550", {"start": v(40.41, 128.4) * mm, "end": v(41.8, 126.84) * mm});
            skLineSegment(sketch, "E551", {"start": v(41.8, 126.84) * mm, "end": v(42.15, 126.5) * mm});
            skLineSegment(sketch, "E552", {"start": v(42.15, 126.5) * mm, "end": v(42.33, 126.32) * mm});
            skLineSegment(sketch, "E553", {"start": v(42.33, 126.32) * mm, "end": v(42.5, 126.14) * mm});
            skLineSegment(sketch, "E554", {"start": v(42.5, 126.14) * mm, "end": v(42.67, 126.14) * mm});
            skLineSegment(sketch, "E555", {"start": v(42.67, 126.14) * mm, "end": v(42.67, 125.97) * mm});
            skLineSegment(sketch, "E556", {"start": v(42.67, 125.97) * mm, "end": v(43.02, 125.8) * mm});
            skLineSegment(sketch, "E557", {"start": v(43.02, 125.8) * mm, "end": v(43.54, 125.45) * mm});
            skLineSegment(sketch, "E558", {"start": v(43.54, 125.45) * mm, "end": v(43.72, 125.45) * mm});
            skLineSegment(sketch, "E559", {"start": v(43.72, 125.45) * mm, "end": v(44.06, 125.1) * mm});
            skLineSegment(sketch, "E560", {"start": v(44.06, 125.1) * mm, "end": v(44.41, 124.93) * mm});
            skLineSegment(sketch, "E561", {"start": v(44.41, 124.93) * mm, "end": v(45.45, 124.75) * mm});
            skLineSegment(sketch, "E562", {"start": v(45.45, 124.75) * mm, "end": v(46.15, 124.75) * mm});
            skLineSegment(sketch, "E563", {"start": v(46.15, 124.75) * mm, "end": v(46.85, 124.4) * mm});
            skLineSegment(sketch, "E564", {"start": v(46.85, 124.4) * mm, "end": v(47.2, 124.23) * mm});
            skLineSegment(sketch, "E565", {"start": v(47.2, 124.23) * mm, "end": v(47.71, 124.23) * mm});
            skLineSegment(sketch, "E566", {"start": v(47.71, 124.23) * mm, "end": v(48.06, 124.23) * mm});
            skLineSegment(sketch, "E567", {"start": v(48.06, 124.23) * mm, "end": v(48.24, 124.23) * mm});
            skLineSegment(sketch, "E568", {"start": v(48.24, 124.23) * mm, "end": v(48.93, 124.4) * mm});
            skLineSegment(sketch, "E569", {"start": v(48.93, 124.4) * mm, "end": v(49.97, 123.54) * mm});
            skLineSegment(sketch, "E570", {"start": v(49.97, 123.54) * mm, "end": v(50.15, 123.19) * mm});
            skLineSegment(sketch, "E571", {"start": v(50.15, 123.19) * mm, "end": v(50.32, 123.19) * mm});
            skLineSegment(sketch, "E572", {"start": v(50.32, 123.19) * mm, "end": v(50.84, 122.84) * mm});
            skLineSegment(sketch, "E573", {"start": v(50.84, 122.84) * mm, "end": v(51.2, 122.67) * mm});
            skLineSegment(sketch, "E574", {"start": v(51.2, 122.67) * mm, "end": v(51.71, 122.32) * mm});
            skLineSegment(sketch, "E575", {"start": v(51.71, 122.32) * mm, "end": v(52.76, 121.62) * mm});
            skLineSegment(sketch, "E576", {"start": v(52.76, 121.62) * mm, "end": v(52.93, 121.45) * mm});
            skLineSegment(sketch, "E577", {"start": v(52.93, 121.45) * mm, "end": v(53.1, 121.45) * mm});
            skLineSegment(sketch, "E578", {"start": v(53.1, 121.45) * mm, "end": v(53.28, 121.28) * mm});
            skLineSegment(sketch, "E579", {"start": v(53.28, 121.28) * mm, "end": v(53.97, 120.93) * mm});
            skLineSegment(sketch, "E580", {"start": v(53.97, 120.93) * mm, "end": v(55.36, 120.06) * mm});
            skLineSegment(sketch, "E581", {"start": v(55.36, 120.06) * mm, "end": v(55.54, 119.89) * mm});
            skLineSegment(sketch, "E582", {"start": v(55.54, 119.89) * mm, "end": v(56.75, 119.71) * mm});
            skLineSegment(sketch, "E583", {"start": v(56.75, 119.71) * mm, "end": v(56.93, 119.54) * mm});
            skLineSegment(sketch, "E584", {"start": v(56.93, 119.54) * mm, "end": v(57.62, 119.71) * mm});
            skLineSegment(sketch, "E585", {"start": v(57.62, 119.71) * mm, "end": v(57.97, 119.89) * mm});
            skLineSegment(sketch, "E586", {"start": v(57.97, 119.89) * mm, "end": v(58.14, 120.06) * mm});
            skLineSegment(sketch, "E587", {"start": v(58.14, 120.06) * mm, "end": v(58.14, 120.23) * mm});
            skLineSegment(sketch, "E588", {"start": v(58.14, 120.23) * mm, "end": v(58.14, 120.4) * mm});
            skLineSegment(sketch, "E589", {"start": v(58.14, 120.4) * mm, "end": v(58.32, 120.4) * mm});
            skLineSegment(sketch, "E590", {"start": v(58.32, 120.4) * mm, "end": v(58.5, 120.4) * mm});
            skLineSegment(sketch, "E591", {"start": v(58.5, 120.4) * mm, "end": v(59.53, 119.71) * mm});
            skLineSegment(sketch, "E592", {"start": v(59.53, 119.71) * mm, "end": v(59.88, 119.54) * mm});
            skLineSegment(sketch, "E593", {"start": v(59.88, 119.54) * mm, "end": v(60.75, 120.4) * mm});
            skLineSegment(sketch, "E594", {"start": v(60.75, 120.4) * mm, "end": v(61.1, 120.23) * mm});
            skLineSegment(sketch, "E595", {"start": v(61.1, 120.23) * mm, "end": v(61.45, 119.71) * mm});
            skLineSegment(sketch, "E596", {"start": v(61.45, 119.71) * mm, "end": v(61.8, 119.2) * mm});
            skLineSegment(sketch, "E597", {"start": v(61.8, 119.2) * mm, "end": v(62.32, 118.5) * mm});
            skLineSegment(sketch, "E598", {"start": v(62.32, 118.5) * mm, "end": v(63.18, 117.28) * mm});
            skLineSegment(sketch, "E599", {"start": v(63.18, 117.28) * mm, "end": v(63.53, 116.93) * mm});
            skLineSegment(sketch, "E600", {"start": v(63.53, 116.93) * mm, "end": v(64.23, 116.4) * mm});
            skLineSegment(sketch, "E601", {"start": v(64.23, 116.4) * mm, "end": v(64.58, 115.89) * mm});
            skLineSegment(sketch, "E602", {"start": v(64.58, 115.89) * mm, "end": v(64.75, 115.54) * mm});
            skLineSegment(sketch, "E603", {"start": v(64.75, 115.54) * mm, "end": v(64.75, 115.36) * mm});
            skLineSegment(sketch, "E604", {"start": v(64.75, 115.36) * mm, "end": v(65.8, 114.67) * mm});
            skLineSegment(sketch, "E605", {"start": v(65.8, 114.67) * mm, "end": v(65.97, 114.67) * mm});
            skLineSegment(sketch, "E606", {"start": v(65.97, 114.67) * mm, "end": v(66.49, 114.5) * mm});
            skLineSegment(sketch, "E607", {"start": v(66.49, 114.5) * mm, "end": v(66.66, 114.32) * mm});
            skLineSegment(sketch, "E608", {"start": v(66.66, 114.32) * mm, "end": v(66.84, 113.97) * mm});
            skLineSegment(sketch, "E609", {"start": v(66.84, 113.97) * mm, "end": v(66.49, 112.93) * mm});
            skLineSegment(sketch, "E610", {"start": v(66.49, 112.93) * mm, "end": v(65.97, 112.58) * mm});
            skLineSegment(sketch, "E611", {"start": v(65.97, 112.58) * mm, "end": v(65.27, 112.24) * mm});
            skLineSegment(sketch, "E612", {"start": v(65.27, 112.24) * mm, "end": v(65.27, 111.71) * mm});
            skLineSegment(sketch, "E613", {"start": v(65.27, 111.71) * mm, "end": v(65.62, 111.02) * mm});
            skLineSegment(sketch, "E614", {"start": v(65.62, 111.02) * mm, "end": v(65.62, 110.84) * mm});
            skLineSegment(sketch, "E615", {"start": v(65.62, 110.84) * mm, "end": v(66.14, 110.15) * mm});
            skLineSegment(sketch, "E616", {"start": v(66.14, 110.15) * mm, "end": v(66.31, 109.8) * mm});
            skLineSegment(sketch, "E617", {"start": v(66.31, 109.8) * mm, "end": v(66.49, 109.63) * mm});
            skLineSegment(sketch, "E618", {"start": v(66.49, 109.63) * mm, "end": v(66.66, 109.28) * mm});
            skLineSegment(sketch, "E619", {"start": v(66.66, 109.28) * mm, "end": v(66.66, 109.1) * mm});
            skLineSegment(sketch, "E620", {"start": v(66.66, 109.1) * mm, "end": v(66.84, 109.1) * mm});
            skLineSegment(sketch, "E621", {"start": v(66.84, 109.1) * mm, "end": v(67, 108.93) * mm});
            skLineSegment(sketch, "E622", {"start": v(67, 108.93) * mm, "end": v(67.7, 107.37) * mm});
            skLineSegment(sketch, "E623", {"start": v(67.7, 107.37) * mm, "end": v(67.7, 106.67) * mm});
            skLineSegment(sketch, "E624", {"start": v(67.7, 106.67) * mm, "end": v(67.88, 106.32) * mm});
            skLineSegment(sketch, "E625", {"start": v(67.88, 106.32) * mm, "end": v(68.05, 105.98) * mm});
            skLineSegment(sketch, "E626", {"start": v(68.05, 105.98) * mm, "end": v(68.75, 105.98) * mm});
            skLineSegment(sketch, "E627", {"start": v(68.75, 105.98) * mm, "end": v(68.75, 105.8) * mm});
            skLineSegment(sketch, "E628", {"start": v(68.75, 105.8) * mm, "end": v(68.75, 105.63) * mm});
            skLineSegment(sketch, "E629", {"start": v(68.75, 105.63) * mm, "end": v(69.27, 104.93) * mm});
            skLineSegment(sketch, "E630", {"start": v(69.27, 104.93) * mm, "end": v(70.49, 104.41) * mm});
            skLineSegment(sketch, "E631", {"start": v(70.49, 104.41) * mm, "end": v(70.31, 104.24) * mm});
            skLineSegment(sketch, "E632", {"start": v(70.31, 104.24) * mm, "end": v(70.31, 103.54) * mm});
            skLineSegment(sketch, "E633", {"start": v(70.31, 103.54) * mm, "end": v(70.83, 101.28) * mm});
            skLineSegment(sketch, "E634", {"start": v(70.83, 101.28) * mm, "end": v(71.35, 100.59) * mm});
            skLineSegment(sketch, "E635", {"start": v(71.35, 100.59) * mm, "end": v(71.88, 99.02) * mm});
            skLineSegment(sketch, "E636", {"start": v(71.88, 99.02) * mm, "end": v(71.88, 98.67) * mm});
            skLineSegment(sketch, "E637", {"start": v(71.88, 98.67) * mm, "end": v(72.4, 97.28) * mm});
            skLineSegment(sketch, "E638", {"start": v(72.4, 97.28) * mm, "end": v(72.57, 97.28) * mm});
            skLineSegment(sketch, "E639", {"start": v(72.57, 97.28) * mm, "end": v(72.92, 96.76) * mm});
            skLineSegment(sketch, "E640", {"start": v(72.92, 96.76) * mm, "end": v(73.27, 95.9) * mm});
            skLineSegment(sketch, "E641", {"start": v(73.27, 95.9) * mm, "end": v(72.92, 95.72) * mm});
            skLineSegment(sketch, "E642", {"start": v(72.92, 95.72) * mm, "end": v(72.05, 95.9) * mm});
            skLineSegment(sketch, "E643", {"start": v(72.05, 95.9) * mm, "end": v(71.35, 96.41) * mm});
            skLineSegment(sketch, "E644", {"start": v(71.35, 96.41) * mm, "end": v(69.27, 96.93) * mm});
            skLineSegment(sketch, "E645", {"start": v(69.27, 96.93) * mm, "end": v(68.4, 97.63) * mm});
            skLineSegment(sketch, "E646", {"start": v(68.4, 97.63) * mm, "end": v(67.88, 98.5) * mm});
            skLineSegment(sketch, "E647", {"start": v(67.88, 98.5) * mm, "end": v(67.36, 98.67) * mm});
            skLineSegment(sketch, "E648", {"start": v(67.36, 98.67) * mm, "end": v(66.49, 99.02) * mm});
            skLineSegment(sketch, "E649", {"start": v(66.49, 99.02) * mm, "end": v(66.31, 99.02) * mm});
            skLineSegment(sketch, "E650", {"start": v(66.31, 99.02) * mm, "end": v(66.14, 99.02) * mm});
            skLineSegment(sketch, "E651", {"start": v(66.14, 99.02) * mm, "end": v(65.44, 98.67) * mm});
            skLineSegment(sketch, "E652", {"start": v(65.44, 98.67) * mm, "end": v(65.1, 98.67) * mm});
            skLineSegment(sketch, "E653", {"start": v(65.1, 98.67) * mm, "end": v(64.75, 98.33) * mm});
            skLineSegment(sketch, "E654", {"start": v(64.75, 98.33) * mm, "end": v(64.58, 98.15) * mm});
            skLineSegment(sketch, "E655", {"start": v(64.58, 98.15) * mm, "end": v(64.4, 98.15) * mm});
            skLineSegment(sketch, "E656", {"start": v(64.4, 98.15) * mm, "end": v(64.23, 98.15) * mm});
            skLineSegment(sketch, "E657", {"start": v(64.23, 98.15) * mm, "end": v(63.88, 97.63) * mm});
            skLineSegment(sketch, "E658", {"start": v(63.88, 97.63) * mm, "end": v(63.7, 97.1) * mm});
            skLineSegment(sketch, "E659", {"start": v(63.7, 97.1) * mm, "end": v(63.53, 96.93) * mm});
            skLineSegment(sketch, "E660", {"start": v(63.53, 96.93) * mm, "end": v(63.36, 96.41) * mm});
            skLineSegment(sketch, "E661", {"start": v(63.36, 96.41) * mm, "end": v(63.18, 96.24) * mm});
            skLineSegment(sketch, "E662", {"start": v(63.18, 96.24) * mm, "end": v(63.36, 95.9) * mm});
            skLineSegment(sketch, "E663", {"start": v(63.36, 95.9) * mm, "end": v(63.7, 95.02) * mm});
            skLineSegment(sketch, "E664", {"start": v(63.7, 95.02) * mm, "end": v(64.23, 94.67) * mm});
            skLineSegment(sketch, "E665", {"start": v(64.23, 94.67) * mm, "end": v(64.58, 94.5) * mm});
            skLineSegment(sketch, "E666", {"start": v(64.58, 94.5) * mm, "end": v(64.4, 94.15) * mm});
            skLineSegment(sketch, "E667", {"start": v(64.4, 94.15) * mm, "end": v(64.23, 93.8) * mm});
            skLineSegment(sketch, "E668", {"start": v(64.23, 93.8) * mm, "end": v(64.05, 93.8) * mm});
            skLineSegment(sketch, "E669", {"start": v(64.05, 93.8) * mm, "end": v(63.53, 93.1) * mm});
            skLineSegment(sketch, "E670", {"start": v(63.53, 93.1) * mm, "end": v(63.53, 92.59) * mm});
            skLineSegment(sketch, "E671", {"start": v(63.53, 92.59) * mm, "end": v(63.7, 91.72) * mm});
            skLineSegment(sketch, "E672", {"start": v(63.7, 91.72) * mm, "end": v(63.7, 91.2) * mm});
            skLineSegment(sketch, "E673", {"start": v(63.7, 91.2) * mm, "end": v(63.88, 90.85) * mm});
            skLineSegment(sketch, "E674", {"start": v(63.88, 90.85) * mm, "end": v(63.88, 90.33) * mm});
            skLineSegment(sketch, "E675", {"start": v(63.88, 90.33) * mm, "end": v(64.05, 89.8) * mm});
            skLineSegment(sketch, "E676", {"start": v(64.05, 89.8) * mm, "end": v(64.23, 89.46) * mm});
            skLineSegment(sketch, "E677", {"start": v(64.23, 89.46) * mm, "end": v(64.4, 88.76) * mm});
            skLineSegment(sketch, "E678", {"start": v(64.4, 88.76) * mm, "end": v(64.58, 88.76) * mm});
            skLineSegment(sketch, "E679", {"start": v(64.58, 88.76) * mm, "end": v(64.92, 88.41) * mm});
            skLineSegment(sketch, "E680", {"start": v(64.92, 88.41) * mm, "end": v(65.1, 88.24) * mm});
            skLineSegment(sketch, "E681", {"start": v(65.1, 88.24) * mm, "end": v(65.27, 88.24) * mm});
            skLineSegment(sketch, "E682", {"start": v(65.27, 88.24) * mm, "end": v(65.97, 87.9) * mm});
            skLineSegment(sketch, "E683", {"start": v(65.97, 87.9) * mm, "end": v(66.31, 86.85) * mm});
            skLineSegment(sketch, "E684", {"start": v(66.31, 86.85) * mm, "end": v(66.49, 86.68) * mm});
            skLineSegment(sketch, "E685", {"start": v(66.49, 86.68) * mm, "end": v(68.75, 85.46) * mm});
            skLineSegment(sketch, "E686", {"start": v(68.75, 85.46) * mm, "end": v(70.49, 84.94) * mm});
            skLineSegment(sketch, "E687", {"start": v(70.49, 84.94) * mm, "end": v(70.49, 83.37) * mm});
            skLineSegment(sketch, "E688", {"start": v(70.49, 83.37) * mm, "end": v(70.49, 83.02) * mm});
            skLineSegment(sketch, "E689", {"start": v(70.49, 83.02) * mm, "end": v(70.83, 82.16) * mm});
            skLineSegment(sketch, "E690", {"start": v(70.83, 82.16) * mm, "end": v(71.18, 81.63) * mm});
            skLineSegment(sketch, "E691", {"start": v(71.18, 81.63) * mm, "end": v(71.53, 81.29) * mm});
            skLineSegment(sketch, "E692", {"start": v(71.53, 81.29) * mm, "end": v(71.53, 80.76) * mm});
            skLineSegment(sketch, "E693", {"start": v(71.53, 80.76) * mm, "end": v(71.7, 80.24) * mm});
            skLineSegment(sketch, "E694", {"start": v(71.7, 80.24) * mm, "end": v(71.88, 78.5) * mm});
            skLineSegment(sketch, "E695", {"start": v(71.88, 78.5) * mm, "end": v(71.88, 77.46) * mm});
            skLineSegment(sketch, "E696", {"start": v(71.88, 77.46) * mm, "end": v(71.88, 77.11) * mm});
            skLineSegment(sketch, "E697", {"start": v(71.88, 77.11) * mm, "end": v(71.88, 75.9) * mm});
            skLineSegment(sketch, "E698", {"start": v(71.88, 75.9) * mm, "end": v(71.7, 75.72) * mm});
            skLineSegment(sketch, "E699", {"start": v(71.7, 75.72) * mm, "end": v(71.7, 75.55) * mm});
            skLineSegment(sketch, "E700", {"start": v(71.7, 75.55) * mm, "end": v(71.88, 75.03) * mm});
            skLineSegment(sketch, "E701", {"start": v(71.88, 75.03) * mm, "end": v(72.22, 73.8) * mm});
            skLineSegment(sketch, "E702", {"start": v(72.22, 73.8) * mm, "end": v(72.22, 73.64) * mm});
            skLineSegment(sketch, "E703", {"start": v(72.22, 73.64) * mm, "end": v(72.57, 73.29) * mm});
            skLineSegment(sketch, "E704", {"start": v(72.57, 73.29) * mm, "end": v(72.57, 73.11) * mm});
            skLineSegment(sketch, "E705", {"start": v(72.57, 73.11) * mm, "end": v(72.92, 72.77) * mm});
            skLineSegment(sketch, "E706", {"start": v(72.92, 72.77) * mm, "end": v(73.1, 72.6) * mm});
            skLineSegment(sketch, "E707", {"start": v(73.1, 72.6) * mm, "end": v(73.1, 72.07) * mm});
            skLineSegment(sketch, "E708", {"start": v(73.1, 72.07) * mm, "end": v(72.92, 71.2) * mm});
            skLineSegment(sketch, "E709", {"start": v(72.92, 71.2) * mm, "end": v(72.92, 70.85) * mm});
            skLineSegment(sketch, "E710", {"start": v(72.92, 70.85) * mm, "end": v(72.92, 70.5) * mm});
            skLineSegment(sketch, "E711", {"start": v(72.92, 70.5) * mm, "end": v(72.57, 68.94) * mm});
            skLineSegment(sketch, "E712", {"start": v(72.57, 68.94) * mm, "end": v(72.4, 68.42) * mm});
            skLineSegment(sketch, "E713", {"start": v(72.4, 68.42) * mm, "end": v(72.4, 68.07) * mm});
            skLineSegment(sketch, "E714", {"start": v(72.4, 68.07) * mm, "end": v(72.22, 68.07) * mm});
            skLineSegment(sketch, "E715", {"start": v(72.22, 68.07) * mm, "end": v(72.05, 67.55) * mm});
            skLineSegment(sketch, "E716", {"start": v(72.05, 67.55) * mm, "end": v(71.35, 66.33) * mm});
            skLineSegment(sketch, "E717", {"start": v(71.35, 66.33) * mm, "end": v(71, 64.94) * mm});
            skLineSegment(sketch, "E718", {"start": v(71, 64.94) * mm, "end": v(71, 64.77) * mm});
            skLineSegment(sketch, "E719", {"start": v(71, 64.77) * mm, "end": v(71, 64.42) * mm});
            skLineSegment(sketch, "E720", {"start": v(71, 64.42) * mm, "end": v(71, 64.07) * mm});
            skLineSegment(sketch, "E721", {"start": v(71, 64.07) * mm, "end": v(71, 63.72) * mm});
            skLineSegment(sketch, "E722", {"start": v(71, 63.72) * mm, "end": v(71, 63.55) * mm});
            skLineSegment(sketch, "E723", {"start": v(71, 63.55) * mm, "end": v(71, 63.2) * mm});
            skLineSegment(sketch, "E724", {"start": v(71, 63.2) * mm, "end": v(71.18, 61.46) * mm});
            skLineSegment(sketch, "E725", {"start": v(71.18, 61.46) * mm, "end": v(71.35, 60.42) * mm});
            skLineSegment(sketch, "E726", {"start": v(71.35, 60.42) * mm, "end": v(71.35, 60.25) * mm});
            skLineSegment(sketch, "E727", {"start": v(71.35, 60.25) * mm, "end": v(71.35, 59.73) * mm});
            skLineSegment(sketch, "E728", {"start": v(71.35, 59.73) * mm, "end": v(71.35, 59.38) * mm});
            skLineSegment(sketch, "E729", {"start": v(71.35, 59.38) * mm, "end": v(71, 57.81) * mm});
            skLineSegment(sketch, "E730", {"start": v(71, 57.81) * mm, "end": v(71, 57.64) * mm});
            skLineSegment(sketch, "E731", {"start": v(71, 57.64) * mm, "end": v(71, 56.77) * mm});
            skLineSegment(sketch, "E732", {"start": v(71, 56.77) * mm, "end": v(71, 55.73) * mm});
            skLineSegment(sketch, "E733", {"start": v(71, 55.73) * mm, "end": v(71, 55.55) * mm});
            skLineSegment(sketch, "E734", {"start": v(71, 55.55) * mm, "end": v(71, 55.38) * mm});
            skLineSegment(sketch, "E735", {"start": v(71, 55.38) * mm, "end": v(70.49, 52.6) * mm});
            skLineSegment(sketch, "E736", {"start": v(70.49, 52.6) * mm, "end": v(70.49, 51.38) * mm});
            skLineSegment(sketch, "E737", {"start": v(70.49, 51.38) * mm, "end": v(70.66, 51.2) * mm});
            skLineSegment(sketch, "E738", {"start": v(70.66, 51.2) * mm, "end": v(70.66, 50.51) * mm});
            skLineSegment(sketch, "E739", {"start": v(70.66, 50.51) * mm, "end": v(70.66, 50.34) * mm});
            skLineSegment(sketch, "E740", {"start": v(70.66, 50.34) * mm, "end": v(70.83, 49.99) * mm});
            skLineSegment(sketch, "E741", {"start": v(70.83, 49.99) * mm, "end": v(70.83, 49.81) * mm});
            skLineSegment(sketch, "E742", {"start": v(70.83, 49.81) * mm, "end": v(70.83, 49.64) * mm});
            skLineSegment(sketch, "E743", {"start": v(70.83, 49.64) * mm, "end": v(70.49, 48.42) * mm});
            skLineSegment(sketch, "E744", {"start": v(70.49, 48.42) * mm, "end": v(70.31, 47.2) * mm});
            skLineSegment(sketch, "E745", {"start": v(70.31, 47.2) * mm, "end": v(70.14, 46.16) * mm});
            skLineSegment(sketch, "E746", {"start": v(70.14, 46.16) * mm, "end": v(70.31, 45.12) * mm});
            skLineSegment(sketch, "E747", {"start": v(70.31, 45.12) * mm, "end": v(70.31, 44.77) * mm});
            skLineSegment(sketch, "E748", {"start": v(70.31, 44.77) * mm, "end": v(70.31, 44.6) * mm});
            skLineSegment(sketch, "E749", {"start": v(70.31, 44.6) * mm, "end": v(70.14, 44.25) * mm});
            skLineSegment(sketch, "E750", {"start": v(70.14, 44.25) * mm, "end": v(69.79, 44.08) * mm});
            skLineSegment(sketch, "E751", {"start": v(69.79, 44.08) * mm, "end": v(69.27, 44.25) * mm});
            skLineSegment(sketch, "E752", {"start": v(69.27, 44.25) * mm, "end": v(68.57, 44.25) * mm});
            skLineSegment(sketch, "E753", {"start": v(68.57, 44.25) * mm, "end": v(68.23, 43.9) * mm});
            skLineSegment(sketch, "E754", {"start": v(68.23, 43.9) * mm, "end": v(68.05, 43.73) * mm});
            skLineSegment(sketch, "E755", {"start": v(68.05, 43.73) * mm, "end": v(66.66, 41.82) * mm});
            skLineSegment(sketch, "E756", {"start": v(66.66, 41.82) * mm, "end": v(66.31, 41.47) * mm});
            skLineSegment(sketch, "E757", {"start": v(66.31, 41.47) * mm, "end": v(65.97, 41.3) * mm});
            skLineSegment(sketch, "E758", {"start": v(65.97, 41.3) * mm, "end": v(65.8, 40.77) * mm});
            skLineSegment(sketch, "E759", {"start": v(65.8, 40.77) * mm, "end": v(65.62, 40.25) * mm});
            skLineSegment(sketch, "E760", {"start": v(65.62, 40.25) * mm, "end": v(65.44, 39.73) * mm});
            skLineSegment(sketch, "E761", {"start": v(65.44, 39.73) * mm, "end": v(65.27, 39.56) * mm});
            skLineSegment(sketch, "E762", {"start": v(65.27, 39.56) * mm, "end": v(64.58, 39.2) * mm});
            skLineSegment(sketch, "E763", {"start": v(64.58, 39.2) * mm, "end": v(64.4, 39.73) * mm});
            skLineSegment(sketch, "E764", {"start": v(64.4, 39.73) * mm, "end": v(64.23, 39.73) * mm});
            skLineSegment(sketch, "E765", {"start": v(64.23, 39.73) * mm, "end": v(63.53, 40.08) * mm});
            skLineSegment(sketch, "E766", {"start": v(63.53, 40.08) * mm, "end": v(63.36, 40.08) * mm});
            skLineSegment(sketch, "E767", {"start": v(63.36, 40.08) * mm, "end": v(62.49, 40.25) * mm});
            skLineSegment(sketch, "E768", {"start": v(62.49, 40.25) * mm, "end": v(62.14, 40.08) * mm});
            skLineSegment(sketch, "E769", {"start": v(62.14, 40.08) * mm, "end": v(61.45, 39.9) * mm});
            skLineSegment(sketch, "E770", {"start": v(61.45, 39.9) * mm, "end": v(61.27, 39.9) * mm});
            skLineSegment(sketch, "E771", {"start": v(61.27, 39.9) * mm, "end": v(60.93, 39.73) * mm});
            skLineSegment(sketch, "E772", {"start": v(60.93, 39.73) * mm, "end": v(60.06, 38.86) * mm});
            skLineSegment(sketch, "E773", {"start": v(60.06, 38.86) * mm, "end": v(59.53, 38) * mm});
            skLineSegment(sketch, "E774", {"start": v(59.53, 38) * mm, "end": v(59.53, 37.82) * mm});
            skLineSegment(sketch, "E775", {"start": v(59.53, 37.82) * mm, "end": v(59.36, 37.82) * mm});
            skLineSegment(sketch, "E776", {"start": v(59.36, 37.82) * mm, "end": v(59.36, 37.64) * mm});
            skLineSegment(sketch, "E777", {"start": v(59.36, 37.64) * mm, "end": v(58.84, 36.25) * mm});
            skLineSegment(sketch, "E778", {"start": v(58.84, 36.25) * mm, "end": v(58.66, 35.04) * mm});
            skLineSegment(sketch, "E779", {"start": v(58.66, 35.04) * mm, "end": v(58.66, 34) * mm});
            skLineSegment(sketch, "E780", {"start": v(58.66, 34) * mm, "end": v(58.14, 32.25) * mm});
            skLineSegment(sketch, "E781", {"start": v(58.14, 32.25) * mm, "end": v(57.97, 31.56) * mm});
            skLineSegment(sketch, "E782", {"start": v(57.97, 31.56) * mm, "end": v(57.97, 31.21) * mm});
            skLineSegment(sketch, "E783", {"start": v(57.97, 31.21) * mm, "end": v(57.97, 30.86) * mm});
            skLineSegment(sketch, "E784", {"start": v(57.97, 30.86) * mm, "end": v(57.97, 30) * mm});
            skLineSegment(sketch, "E785", {"start": v(57.97, 30) * mm, "end": v(57.8, 28.78) * mm});
            skLineSegment(sketch, "E786", {"start": v(57.8, 28.78) * mm, "end": v(57.97, 28.25) * mm});
            skLineSegment(sketch, "E787", {"start": v(57.97, 28.25) * mm, "end": v(57.8, 27.9) * mm});
            skLineSegment(sketch, "E788", {"start": v(57.8, 27.9) * mm, "end": v(57.62, 26.86) * mm});
            skLineSegment(sketch, "E789", {"start": v(57.62, 26.86) * mm, "end": v(56.93, 25.82) * mm});
            skLineSegment(sketch, "E790", {"start": v(56.93, 25.82) * mm, "end": v(56.93, 25.65) * mm});
            skLineSegment(sketch, "E791", {"start": v(56.93, 25.65) * mm, "end": v(56.75, 25.12) * mm});
            skLineSegment(sketch, "E792", {"start": v(56.75, 25.12) * mm, "end": v(56.75, 24.43) * mm});
            skLineSegment(sketch, "E793", {"start": v(56.75, 24.43) * mm, "end": v(57.1, 23.56) * mm});
            skLineSegment(sketch, "E794", {"start": v(57.1, 23.56) * mm, "end": v(56.23, 23.39) * mm});
            skLineSegment(sketch, "E795", {"start": v(56.23, 23.39) * mm, "end": v(55.19, 23.56) * mm});
            skLineSegment(sketch, "E796", {"start": v(55.19, 23.56) * mm, "end": v(53.62, 23.21) * mm});
            skLineSegment(sketch, "E797", {"start": v(53.62, 23.21) * mm, "end": v(52.76, 22.52) * mm});
            skLineSegment(sketch, "E798", {"start": v(52.76, 22.52) * mm, "end": v(52.06, 22) * mm});
            skLineSegment(sketch, "E799", {"start": v(52.06, 22) * mm, "end": v(51.89, 21.47) * mm});
            skLineSegment(sketch, "E800", {"start": v(51.89, 21.47) * mm, "end": v(51.71, 21.47) * mm});
            skLineSegment(sketch, "E801", {"start": v(51.71, 21.47) * mm, "end": v(51.71, 21.3) * mm});
            skLineSegment(sketch, "E802", {"start": v(51.71, 21.3) * mm, "end": v(51.54, 20.95) * mm});
            skLineSegment(sketch, "E803", {"start": v(51.54, 20.95) * mm, "end": v(51.54, 20.78) * mm});
            skLineSegment(sketch, "E804", {"start": v(51.54, 20.78) * mm, "end": v(52.06, 18.86) * mm});
            skLineSegment(sketch, "E805", {"start": v(52.06, 18.86) * mm, "end": v(51.2, 18.7) * mm});
            skLineSegment(sketch, "E806", {"start": v(51.2, 18.7) * mm, "end": v(50.5, 18.7) * mm});
            skLineSegment(sketch, "E807", {"start": v(50.5, 18.7) * mm, "end": v(48.58, 18.7) * mm});
            skLineSegment(sketch, "E808", {"start": v(48.58, 18.7) * mm, "end": v(48.41, 18.34) * mm});
            skLineSegment(sketch, "E809", {"start": v(48.41, 18.34) * mm, "end": v(48.06, 18.34) * mm});
            skLineSegment(sketch, "E810", {"start": v(48.06, 18.34) * mm, "end": v(47.71, 18.17) * mm});
            skLineSegment(sketch, "E811", {"start": v(47.71, 18.17) * mm, "end": v(47.54, 18.17) * mm});
            skLineSegment(sketch, "E812", {"start": v(47.54, 18.17) * mm, "end": v(46.67, 18.17) * mm});
            skLineSegment(sketch, "E813", {"start": v(46.67, 18.17) * mm, "end": v(46.15, 18.17) * mm});
            skLineSegment(sketch, "E814", {"start": v(46.15, 18.17) * mm, "end": v(45.1, 18.17) * mm});
            skLineSegment(sketch, "E815", {"start": v(45.1, 18.17) * mm, "end": v(44.59, 18.34) * mm});
            skLineSegment(sketch, "E816", {"start": v(44.59, 18.34) * mm, "end": v(44.06, 18.34) * mm});
            skLineSegment(sketch, "E817", {"start": v(44.06, 18.34) * mm, "end": v(43.02, 17.82) * mm});
            skLineSegment(sketch, "E818", {"start": v(43.02, 17.82) * mm, "end": v(42.67, 17.47) * mm});
            skLineSegment(sketch, "E819", {"start": v(42.67, 17.47) * mm, "end": v(42.5, 17.13) * mm});
            skLineSegment(sketch, "E820", {"start": v(42.5, 17.13) * mm, "end": v(42.33, 16.95) * mm});
            skLineSegment(sketch, "E821", {"start": v(42.33, 16.95) * mm, "end": v(41.8, 16.26) * mm});
            skLineSegment(sketch, "E822", {"start": v(41.8, 16.26) * mm, "end": v(41.46, 16.08) * mm});
            skLineSegment(sketch, "E823", {"start": v(41.46, 16.08) * mm, "end": v(40.93, 15.21) * mm});
            skLineSegment(sketch, "E824", {"start": v(40.93, 15.21) * mm, "end": v(40.76, 14.34) * mm});
            skLineSegment(sketch, "E825", {"start": v(40.76, 14.34) * mm, "end": v(40.76, 13.47) * mm});
            skLineSegment(sketch, "E826", {"start": v(40.76, 13.47) * mm, "end": v(39.9, 13.13) * mm});
            skLineSegment(sketch, "E827", {"start": v(39.9, 13.13) * mm, "end": v(39.54, 12.43) * mm});
            skLineSegment(sketch, "E828", {"start": v(39.54, 12.43) * mm, "end": v(39.37, 11.74) * mm});
            skLineSegment(sketch, "E829", {"start": v(39.37, 11.74) * mm, "end": v(39.2, 8.43) * mm});
            skLineSegment(sketch, "E830", {"start": v(39.2, 8.43) * mm, "end": v(39.2, 7.91) * mm});
            skLineSegment(sketch, "E831", {"start": v(39.2, 7.91) * mm, "end": v(39.02, 6.17) * mm});
            skLineSegment(sketch, "E832", {"start": v(39.02, 6.17) * mm, "end": v(39.02, 5.13) * mm});
            skLineSegment(sketch, "E833", {"start": v(39.02, 5.13) * mm, "end": v(38.85, 3.4) * mm});
            skLineSegment(sketch, "E834", {"start": v(38.85, 3.4) * mm, "end": v(38.68, 2.7) * mm});
            skLineSegment(sketch, "E835", {"start": v(38.68, 2.7) * mm, "end": v(38.68, 2.52) * mm});
            skLineSegment(sketch, "E836", {"start": v(38.68, 2.52) * mm, "end": v(38.5, 2.17) * mm});
            skLineSegment(sketch, "E837", {"start": v(38.5, 2.17) * mm, "end": v(37.98, 1.65) * mm});
            skLineSegment(sketch, "E838", {"start": v(37.98, 1.65) * mm, "end": v(37.8, 1.3) * mm});
            skLineSegment(sketch, "E839", {"start": v(37.8, 1.3) * mm, "end": v(37.29, 1.3) * mm});
            skLineSegment(sketch, "E840", {"start": v(37.29, 1.3) * mm, "end": v(37.29, 0.96) * mm});
            skLineSegment(sketch, "E841", {"start": v(37.29, 0.96) * mm, "end": v(37.29, 0.6) * mm});
            skLineSegment(sketch, "E842", {"start": v(37.29, 0.6) * mm, "end": v(37.63, -0.26) * mm});
            skLineSegment(sketch, "E843", {"start": v(37.63, -0.26) * mm, "end": v(38.15, -2) * mm});
            skLineSegment(sketch, "E844", {"start": v(38.15, -2) * mm, "end": v(38.68, -3.04) * mm});
            skLineSegment(sketch, "E845", {"start": v(38.68, -3.04) * mm, "end": v(39.72, -5.13) * mm});
            skLineSegment(sketch, "E846", {"start": v(39.72, -5.13) * mm, "end": v(40.41, -5.83) * mm});
            skLineSegment(sketch, "E847", {"start": v(40.41, -5.83) * mm, "end": v(41.28, -6.35) * mm});
            skLineSegment(sketch, "E848", {"start": v(41.28, -6.35) * mm, "end": v(41.63, -6.52) * mm});
            skLineSegment(sketch, "E849", {"start": v(41.63, -6.52) * mm, "end": v(42.85, -7.22) * mm});
            skLineSegment(sketch, "E850", {"start": v(42.85, -7.22) * mm, "end": v(43.02, -7.22) * mm});
            skLineSegment(sketch, "E851", {"start": v(43.02, -7.22) * mm, "end": v(44.93, -7.39) * mm});
            skLineSegment(sketch, "E852", {"start": v(44.93, -7.39) * mm, "end": v(45.28, -7.56) * mm});
            skLineSegment(sketch, "E853", {"start": v(45.28, -7.56) * mm, "end": v(46.85, -8.26) * mm});
            skLineSegment(sketch, "E854", {"start": v(46.85, -8.26) * mm, "end": v(47.37, -8.43) * mm});
            skLineSegment(sketch, "E855", {"start": v(47.37, -8.43) * mm, "end": v(47.37, -7.91) * mm});
            skLineSegment(sketch, "E856", {"start": v(47.37, -7.91) * mm, "end": v(47.89, -8.26) * mm});
            skLineSegment(sketch, "E857", {"start": v(47.89, -8.26) * mm, "end": v(48.24, -8.43) * mm});
            skLineSegment(sketch, "E858", {"start": v(48.24, -8.43) * mm, "end": v(48.41, -8.43) * mm});
            skLineSegment(sketch, "E859", {"start": v(48.41, -8.43) * mm, "end": v(48.58, -8.6) * mm});
            skLineSegment(sketch, "E860", {"start": v(48.58, -8.6) * mm, "end": v(49.8, -9.13) * mm});
            skLineSegment(sketch, "E861", {"start": v(49.8, -9.13) * mm, "end": v(51.02, -10.7) * mm});
            skLineSegment(sketch, "E862", {"start": v(51.02, -10.7) * mm, "end": v(51.2, -10.7) * mm});
            skLineSegment(sketch, "E863", {"start": v(51.2, -10.7) * mm, "end": v(52.76, -11.21) * mm});
            skLineSegment(sketch, "E864", {"start": v(52.76, -11.21) * mm, "end": v(52.93, -11.21) * mm});
            skLineSegment(sketch, "E865", {"start": v(52.93, -11.21) * mm, "end": v(53.62, -10.52) * mm});
            skLineSegment(sketch, "E866", {"start": v(53.62, -10.52) * mm, "end": v(55.54, -8.26) * mm});
            skLineSegment(sketch, "E867", {"start": v(55.54, -8.26) * mm, "end": v(56.75, -6.7) * mm});
            skLineSegment(sketch, "E868", {"start": v(56.75, -6.7) * mm, "end": v(56.93, -6.52) * mm});
            skLineSegment(sketch, "E869", {"start": v(56.93, -6.52) * mm, "end": v(57.27, -5.83) * mm});
            skLineSegment(sketch, "E870", {"start": v(57.27, -5.83) * mm, "end": v(57.97, -5.13) * mm});
            skLineSegment(sketch, "E871", {"start": v(57.97, -5.13) * mm, "end": v(58.5, -4.26) * mm});
            skLineSegment(sketch, "E872", {"start": v(58.5, -4.26) * mm, "end": v(58.5, -4.09) * mm});
            skLineSegment(sketch, "E873", {"start": v(58.5, -4.09) * mm, "end": v(59.01, -4.09) * mm});
            skLineSegment(sketch, "E874", {"start": v(59.01, -4.09) * mm, "end": v(59.19, -3.4) * mm});
            skLineSegment(sketch, "E875", {"start": v(59.19, -3.4) * mm, "end": v(59.19, -3.04) * mm});
            skLineSegment(sketch, "E876", {"start": v(59.19, -3.04) * mm, "end": v(59.19, -2.87) * mm});
            skLineSegment(sketch, "E877", {"start": v(59.19, -2.87) * mm, "end": v(59.36, -2.7) * mm});
            skLineSegment(sketch, "E878", {"start": v(59.36, -2.7) * mm, "end": v(59.7, -2.35) * mm});
            skLineSegment(sketch, "E879", {"start": v(59.7, -2.35) * mm, "end": v(60.58, -1.65) * mm});
            skLineSegment(sketch, "E880", {"start": v(60.58, -1.65) * mm, "end": v(61.1, -1.65) * mm});
            skLineSegment(sketch, "E881", {"start": v(61.1, -1.65) * mm, "end": v(61.1, -1.83) * mm});
            skLineSegment(sketch, "E882", {"start": v(61.1, -1.83) * mm, "end": v(61.45, -2.17) * mm});
            skLineSegment(sketch, "E883", {"start": v(61.45, -2.17) * mm, "end": v(63.01, -1.83) * mm});
            skLineSegment(sketch, "E884", {"start": v(63.01, -1.83) * mm, "end": v(63.53, -1.13) * mm});
            skLineSegment(sketch, "E885", {"start": v(63.53, -1.13) * mm, "end": v(63.7, -0.78) * mm});
            skLineSegment(sketch, "E886", {"start": v(63.7, -0.78) * mm, "end": v(63.7, -0.44) * mm});
            skLineSegment(sketch, "E887", {"start": v(63.7, -0.44) * mm, "end": v(63.88, -0.26) * mm});
            skLineSegment(sketch, "E888", {"start": v(63.88, -0.26) * mm, "end": v(64.05, 0.09) * mm});
            skLineSegment(sketch, "E889", {"start": v(64.05, 0.09) * mm, "end": v(64.75, 1.13) * mm});
            skLineSegment(sketch, "E890", {"start": v(64.75, 1.13) * mm, "end": v(65.1, 1.65) * mm});
            skLineSegment(sketch, "E891", {"start": v(65.1, 1.65) * mm, "end": v(65.1, 2) * mm});
            skLineSegment(sketch, "E892", {"start": v(65.1, 2) * mm, "end": v(64.92, 2.35) * mm});
            skLineSegment(sketch, "E893", {"start": v(64.92, 2.35) * mm, "end": v(64.75, 2.35) * mm});
            skLineSegment(sketch, "E894", {"start": v(64.75, 2.35) * mm, "end": v(65.1, 3.56) * mm});
            skLineSegment(sketch, "E895", {"start": v(65.1, 3.56) * mm, "end": v(65.8, 4.43) * mm});
            skLineSegment(sketch, "E896", {"start": v(65.8, 4.43) * mm, "end": v(66.31, 4.6) * mm});
            skLineSegment(sketch, "E897", {"start": v(66.31, 4.6) * mm, "end": v(66.66, 4.96) * mm});
            skLineSegment(sketch, "E898", {"start": v(66.66, 4.96) * mm, "end": v(66.66, 5.13) * mm});
            skLineSegment(sketch, "E899", {"start": v(66.66, 5.13) * mm, "end": v(66.49, 5.82) * mm});
            skLineSegment(sketch, "E900", {"start": v(66.49, 5.82) * mm, "end": v(66.66, 6.35) * mm});
            skLineSegment(sketch, "E901", {"start": v(66.66, 6.35) * mm, "end": v(66.84, 6.87) * mm});
            skLineSegment(sketch, "E902", {"start": v(66.84, 6.87) * mm, "end": v(67, 7.04) * mm});
            skLineSegment(sketch, "E903", {"start": v(67, 7.04) * mm, "end": v(67.7, 7.39) * mm});
            skLineSegment(sketch, "E904", {"start": v(67.7, 7.39) * mm, "end": v(67.7, 7.56) * mm});
            skLineSegment(sketch, "E905", {"start": v(67.7, 7.56) * mm, "end": v(67.7, 7.91) * mm});
            skLineSegment(sketch, "E906", {"start": v(67.7, 7.91) * mm, "end": v(69.44, 8.78) * mm});
            skLineSegment(sketch, "E907", {"start": v(69.44, 8.78) * mm, "end": v(70.83, 10.52) * mm});
            skLineSegment(sketch, "E908", {"start": v(70.83, 10.52) * mm, "end": v(70.83, 11.04) * mm});
            skLineSegment(sketch, "E909", {"start": v(70.83, 11.04) * mm, "end": v(70.83, 11.21) * mm});
            skLineSegment(sketch, "E910", {"start": v(70.83, 11.21) * mm, "end": v(70.83, 11.39) * mm});
            skLineSegment(sketch, "E911", {"start": v(70.83, 11.39) * mm, "end": v(70.83, 11.56) * mm});
            skLineSegment(sketch, "E912", {"start": v(70.83, 11.56) * mm, "end": v(70.66, 11.91) * mm});
            skLineSegment(sketch, "E913", {"start": v(70.66, 11.91) * mm, "end": v(70.49, 12.08) * mm});
            skLineSegment(sketch, "E914", {"start": v(70.49, 12.08) * mm, "end": v(70.31, 12.43) * mm});
            skLineSegment(sketch, "E915", {"start": v(70.31, 12.43) * mm, "end": v(69.96, 12.43) * mm});
            skLineSegment(sketch, "E916", {"start": v(69.96, 12.43) * mm, "end": v(69.79, 12.78) * mm});
            skLineSegment(sketch, "E917", {"start": v(69.79, 12.78) * mm, "end": v(69.96, 12.95) * mm});
            skLineSegment(sketch, "E918", {"start": v(69.96, 12.95) * mm, "end": v(70.31, 13.13) * mm});
            skLineSegment(sketch, "E919", {"start": v(70.31, 13.13) * mm, "end": v(70.49, 13.13) * mm});
            skLineSegment(sketch, "E920", {"start": v(70.49, 13.13) * mm, "end": v(71.53, 13.3) * mm});
            skLineSegment(sketch, "E921", {"start": v(71.53, 13.3) * mm, "end": v(72.05, 13.65) * mm});
            skLineSegment(sketch, "E922", {"start": v(72.05, 13.65) * mm, "end": v(72.22, 13.65) * mm});
            skLineSegment(sketch, "E923", {"start": v(72.22, 13.65) * mm, "end": v(72.4, 13.82) * mm});
            skLineSegment(sketch, "E924", {"start": v(72.4, 13.82) * mm, "end": v(72.92, 14.34) * mm});
            skLineSegment(sketch, "E925", {"start": v(72.92, 14.34) * mm, "end": v(73.44, 14.87) * mm});
            skLineSegment(sketch, "E926", {"start": v(73.44, 14.87) * mm, "end": v(73.96, 16.08) * mm});
            skLineSegment(sketch, "E927", {"start": v(73.96, 16.08) * mm, "end": v(74.14, 16.26) * mm});
            skLineSegment(sketch, "E928", {"start": v(74.14, 16.26) * mm, "end": v(74.48, 17.13) * mm});
            skLineSegment(sketch, "E929", {"start": v(74.48, 17.13) * mm, "end": v(74.48, 17.47) * mm});
            skLineSegment(sketch, "E930", {"start": v(74.48, 17.47) * mm, "end": v(75.18, 17.82) * mm});
            skLineSegment(sketch, "E931", {"start": v(75.18, 17.82) * mm, "end": v(75.53, 17.82) * mm});
            skLineSegment(sketch, "E932", {"start": v(75.53, 17.82) * mm, "end": v(75.7, 18) * mm});
            skLineSegment(sketch, "E933", {"start": v(75.7, 18) * mm, "end": v(76.22, 18.17) * mm});
            skLineSegment(sketch, "E934", {"start": v(76.22, 18.17) * mm, "end": v(76.4, 18.17) * mm});
            skLineSegment(sketch, "E935", {"start": v(76.4, 18.17) * mm, "end": v(77.26, 18.17) * mm});
            skLineSegment(sketch, "E936", {"start": v(77.26, 18.17) * mm, "end": v(77.44, 18.17) * mm});
            skLineSegment(sketch, "E937", {"start": v(77.44, 18.17) * mm, "end": v(77.96, 18.34) * mm});
            skLineSegment(sketch, "E938", {"start": v(77.96, 18.34) * mm, "end": v(78.13, 18.34) * mm});
            skLineSegment(sketch, "E939", {"start": v(78.13, 18.34) * mm, "end": v(78.83, 18.17) * mm});
            skLineSegment(sketch, "E940", {"start": v(78.83, 18.17) * mm, "end": v(80.22, 18.7) * mm});
            skLineSegment(sketch, "E941", {"start": v(80.22, 18.7) * mm, "end": v(80.57, 18.7) * mm});
            skLineSegment(sketch, "E942", {"start": v(80.57, 18.7) * mm, "end": v(80.74, 18.86) * mm});
            skLineSegment(sketch, "E943", {"start": v(80.74, 18.86) * mm, "end": v(81.09, 19.04) * mm});
            skLineSegment(sketch, "E944", {"start": v(81.09, 19.04) * mm, "end": v(81.26, 19.04) * mm});
            skLineSegment(sketch, "E945", {"start": v(81.26, 19.04) * mm, "end": v(81.44, 19.21) * mm});
            skLineSegment(sketch, "E946", {"start": v(81.44, 19.21) * mm, "end": v(81.78, 19.39) * mm});
            skLineSegment(sketch, "E947", {"start": v(81.78, 19.39) * mm, "end": v(81.96, 19.56) * mm});
            skLineSegment(sketch, "E948", {"start": v(81.96, 19.56) * mm, "end": v(81.96, 19.73) * mm});
            skLineSegment(sketch, "E949", {"start": v(81.96, 19.73) * mm, "end": v(82.65, 19.9) * mm});
            skLineSegment(sketch, "E950", {"start": v(82.65, 19.9) * mm, "end": v(82.83, 19.9) * mm});
            skLineSegment(sketch, "E951", {"start": v(82.83, 19.9) * mm, "end": v(84.22, 19.73) * mm});
            skLineSegment(sketch, "E952", {"start": v(84.22, 19.73) * mm, "end": v(84.4, 19.73) * mm});
            skLineSegment(sketch, "E953", {"start": v(84.4, 19.73) * mm, "end": v(84.91, 19.9) * mm});
            skLineSegment(sketch, "E954", {"start": v(84.91, 19.9) * mm, "end": v(85.09, 20.08) * mm});
            skLineSegment(sketch, "E955", {"start": v(85.09, 20.08) * mm, "end": v(85.43, 20.08) * mm});
            skLineSegment(sketch, "E956", {"start": v(85.43, 20.08) * mm, "end": v(85.96, 20.78) * mm});
            skLineSegment(sketch, "E957", {"start": v(85.96, 20.78) * mm, "end": v(86.3, 21.47) * mm});
            skLineSegment(sketch, "E958", {"start": v(86.3, 21.47) * mm, "end": v(86.3, 21.65) * mm});
            skLineSegment(sketch, "E959", {"start": v(86.3, 21.65) * mm, "end": v(86.48, 22) * mm});
            skLineSegment(sketch, "E960", {"start": v(86.48, 22) * mm, "end": v(86.65, 22.17) * mm});
            skLineSegment(sketch, "E961", {"start": v(86.65, 22.17) * mm, "end": v(86.82, 22.7) * mm});
            skLineSegment(sketch, "E962", {"start": v(86.82, 22.7) * mm, "end": v(87.17, 23.04) * mm});
            skLineSegment(sketch, "E963", {"start": v(87.17, 23.04) * mm, "end": v(87.7, 23.04) * mm});
            skLineSegment(sketch, "E964", {"start": v(87.7, 23.04) * mm, "end": v(87.87, 23.21) * mm});
            skLineSegment(sketch, "E965", {"start": v(87.87, 23.21) * mm, "end": v(88.39, 23.21) * mm});
            skLineSegment(sketch, "E966", {"start": v(88.39, 23.21) * mm, "end": v(88.56, 23.21) * mm});
            skLineSegment(sketch, "E967", {"start": v(88.56, 23.21) * mm, "end": v(88.91, 23.39) * mm});
            skLineSegment(sketch, "E968", {"start": v(88.91, 23.39) * mm, "end": v(89.26, 23.73) * mm});
            skLineSegment(sketch, "E969", {"start": v(89.26, 23.73) * mm, "end": v(89.43, 23.9) * mm});
            skLineSegment(sketch, "E970", {"start": v(89.43, 23.9) * mm, "end": v(90.13, 24.6) * mm});
            skLineSegment(sketch, "E971", {"start": v(90.13, 24.6) * mm, "end": v(90.65, 24.6) * mm});
            skLineSegment(sketch, "E972", {"start": v(90.65, 24.6) * mm, "end": v(90.82, 24.43) * mm});
            skLineSegment(sketch, "E973", {"start": v(90.82, 24.43) * mm, "end": v(91.34, 24.43) * mm});
            skLineSegment(sketch, "E974", {"start": v(91.34, 24.43) * mm, "end": v(92.04, 24.78) * mm});
            skLineSegment(sketch, "E975", {"start": v(92.04, 24.78) * mm, "end": v(92.04, 24.95) * mm});
            skLineSegment(sketch, "E976", {"start": v(92.04, 24.95) * mm, "end": v(92.21, 24.95) * mm});
            skLineSegment(sketch, "E977", {"start": v(92.21, 24.95) * mm, "end": v(92.9, 25.12) * mm});
            skLineSegment(sketch, "E978", {"start": v(92.9, 25.12) * mm, "end": v(93.43, 24.6) * mm});
            skLineSegment(sketch, "E979", {"start": v(93.43, 24.6) * mm, "end": v(93.6, 24.43) * mm});
            skLineSegment(sketch, "E980", {"start": v(93.6, 24.43) * mm, "end": v(94.3, 23.56) * mm});
            skLineSegment(sketch, "E981", {"start": v(94.3, 23.56) * mm, "end": v(95.17, 23.21) * mm});
            skLineSegment(sketch, "E982", {"start": v(95.17, 23.21) * mm, "end": v(96.39, 22.86) * mm});
            skLineSegment(sketch, "E983", {"start": v(96.39, 22.86) * mm, "end": v(97.43, 22.7) * mm});
            skLineSegment(sketch, "E984", {"start": v(97.43, 22.7) * mm, "end": v(97.6, 22.52) * mm});
            skLineSegment(sketch, "E985", {"start": v(97.6, 22.52) * mm, "end": v(98.12, 22.34) * mm});
            skLineSegment(sketch, "E986", {"start": v(98.12, 22.34) * mm, "end": v(98.3, 22.17) * mm});
            skLineSegment(sketch, "E987", {"start": v(98.3, 22.17) * mm, "end": v(98.47, 22.17) * mm});
            skLineSegment(sketch, "E988", {"start": v(98.47, 22.17) * mm, "end": v(99.51, 21.65) * mm});
            skLineSegment(sketch, "E989", {"start": v(99.51, 21.65) * mm, "end": v(99.86, 20.95) * mm});
            skLineSegment(sketch, "E990", {"start": v(99.86, 20.95) * mm, "end": v(100.2, 20.6) * mm});
            skLineSegment(sketch, "E991", {"start": v(100.2, 20.6) * mm, "end": v(100.56, 20.6) * mm});
            skLineSegment(sketch, "E992", {"start": v(100.56, 20.6) * mm, "end": v(100.9, 20.43) * mm});
            skLineSegment(sketch, "E993", {"start": v(100.9, 20.43) * mm, "end": v(101.08, 20.43) * mm});
            skLineSegment(sketch, "E994", {"start": v(101.08, 20.43) * mm, "end": v(102.12, 19.73) * mm});
            skLineSegment(sketch, "E995", {"start": v(102.12, 19.73) * mm, "end": v(102.47, 19.39) * mm});
            skLineSegment(sketch, "E996", {"start": v(102.47, 19.39) * mm, "end": v(102.64, 19.21) * mm});
            skLineSegment(sketch, "E997", {"start": v(102.64, 19.21) * mm, "end": v(103.16, 18) * mm});
            skLineSegment(sketch, "E998", {"start": v(103.16, 18) * mm, "end": v(103.34, 17.65) * mm});
            skLineSegment(sketch, "E999", {"start": v(103.34, 17.65) * mm, "end": v(103.51, 17.47) * mm});
            skLineSegment(sketch, "E1000", {"start": v(103.51, 17.47) * mm, "end": v(104.03, 16.26) * mm});
            skLineSegment(sketch, "E1001", {"start": v(104.03, 16.26) * mm, "end": v(104.2, 16.08) * mm});
            skLineSegment(sketch, "E1002", {"start": v(104.2, 16.08) * mm, "end": v(104.55, 15.39) * mm});
            skLineSegment(sketch, "E1003", {"start": v(104.55, 15.39) * mm, "end": v(104.73, 15.04) * mm});
            skLineSegment(sketch, "E1004", {"start": v(104.73, 15.04) * mm, "end": v(104.73, 14.87) * mm});
            skLineSegment(sketch, "E1005", {"start": v(104.73, 14.87) * mm, "end": v(105.08, 14) * mm});
            skLineSegment(sketch, "E1006", {"start": v(105.08, 14) * mm, "end": v(105.6, 12.26) * mm});
            skLineSegment(sketch, "E1007", {"start": v(105.6, 12.26) * mm, "end": v(105.77, 12.08) * mm});
            skLineSegment(sketch, "E1008", {"start": v(105.77, 12.08) * mm, "end": v(105.95, 11.39) * mm});
            skLineSegment(sketch, "E1009", {"start": v(105.95, 11.39) * mm, "end": v(106.99, 10.52) * mm});
            skLineSegment(sketch, "E1010", {"start": v(106.99, 10.52) * mm, "end": v(107.16, 10.17) * mm});
            skLineSegment(sketch, "E1011", {"start": v(107.16, 10.17) * mm, "end": v(107.51, 9.82) * mm});
            skLineSegment(sketch, "E1012", {"start": v(107.51, 9.82) * mm, "end": v(107.68, 9.65) * mm});
            skLineSegment(sketch, "E1013", {"start": v(107.68, 9.65) * mm, "end": v(107.86, 9.3) * mm});
            skLineSegment(sketch, "E1014", {"start": v(107.86, 9.3) * mm, "end": v(107.86, 9.13) * mm});
            skLineSegment(sketch, "E1015", {"start": v(107.86, 9.13) * mm, "end": v(107.86, 8.95) * mm});
            skLineSegment(sketch, "E1016", {"start": v(107.86, 8.95) * mm, "end": v(108.03, 8.6) * mm});
            skLineSegment(sketch, "E1017", {"start": v(108.03, 8.6) * mm, "end": v(107.86, 8.6) * mm});
            skLineSegment(sketch, "E1018", {"start": v(107.86, 8.6) * mm, "end": v(107.68, 8.43) * mm});
            skLineSegment(sketch, "E1019", {"start": v(107.68, 8.43) * mm, "end": v(107.86, 8.09) * mm});
            skLineSegment(sketch, "E1020", {"start": v(107.86, 8.09) * mm, "end": v(108.03, 7.91) * mm});
            skLineSegment(sketch, "E1021", {"start": v(108.03, 7.91) * mm, "end": v(108.2, 7.74) * mm});
            skLineSegment(sketch, "E1022", {"start": v(108.2, 7.74) * mm, "end": v(108.38, 7.56) * mm});
            skLineSegment(sketch, "E1023", {"start": v(108.38, 7.56) * mm, "end": v(108.55, 7.56) * mm});
            skLineSegment(sketch, "E1024", {"start": v(108.55, 7.56) * mm, "end": v(108.55, 7.04) * mm});
            skLineSegment(sketch, "E1025", {"start": v(108.55, 7.04) * mm, "end": v(108.73, 5.82) * mm});
            skLineSegment(sketch, "E1026", {"start": v(108.73, 5.82) * mm, "end": v(109.07, 4.6) * mm});
            skLineSegment(sketch, "E1027", {"start": v(109.07, 4.6) * mm, "end": v(109.07, 4.09) * mm});
            skLineSegment(sketch, "E1028", {"start": v(109.07, 4.09) * mm, "end": v(109.25, 3.56) * mm});
            skLineSegment(sketch, "E1029", {"start": v(109.25, 3.56) * mm, "end": v(109.42, 2.87) * mm});
            skLineSegment(sketch, "E1030", {"start": v(109.42, 2.87) * mm, "end": v(109.42, 2) * mm});
            skLineSegment(sketch, "E1031", {"start": v(109.42, 2) * mm, "end": v(109.42, 1.3) * mm});
            skLineSegment(sketch, "E1032", {"start": v(109.42, 1.3) * mm, "end": v(109.77, 0.78) * mm});
            skLineSegment(sketch, "E1033", {"start": v(109.77, 0.78) * mm, "end": v(109.94, -0.96) * mm});
            skLineSegment(sketch, "E1034", {"start": v(109.94, -0.96) * mm, "end": v(109.94, -1.65) * mm});
            skLineSegment(sketch, "E1035", {"start": v(109.94, -1.65) * mm, "end": v(110.12, -2.87) * mm});
            skLineSegment(sketch, "E1036", {"start": v(110.12, -2.87) * mm, "end": v(110.3, -3.74) * mm});
            skLineSegment(sketch, "E1037", {"start": v(110.3, -3.74) * mm, "end": v(110.3, -4.09) * mm});
            skLineSegment(sketch, "E1038", {"start": v(110.3, -4.09) * mm, "end": v(110.3, -4.43) * mm});
            skLineSegment(sketch, "E1039", {"start": v(110.3, -4.43) * mm, "end": v(110.3, -4.6) * mm});
            skLineSegment(sketch, "E1040", {"start": v(110.3, -4.6) * mm, "end": v(110.3, -5.48) * mm});
            skLineSegment(sketch, "E1041", {"start": v(110.3, -5.48) * mm, "end": v(110.3, -5.65) * mm});
            skLineSegment(sketch, "E1042", {"start": v(110.3, -5.65) * mm, "end": v(110.3, -5.83) * mm});
            skLineSegment(sketch, "E1043", {"start": v(110.3, -5.83) * mm, "end": v(110.47, -6.87) * mm});
            skLineSegment(sketch, "E1044", {"start": v(110.47, -6.87) * mm, "end": v(110.47, -7.22) * mm});
            skLineSegment(sketch, "E1045", {"start": v(110.47, -7.22) * mm, "end": v(110.64, -9.13) * mm});
            skLineSegment(sketch, "E1046", {"start": v(110.64, -9.13) * mm, "end": v(110.64, -9.3) * mm});
            skLineSegment(sketch, "E1047", {"start": v(110.64, -9.3) * mm, "end": v(110.64, -9.48) * mm});
            skLineSegment(sketch, "E1048", {"start": v(110.64, -9.48) * mm, "end": v(110.81, -10.35) * mm});
            skLineSegment(sketch, "E1049", {"start": v(110.81, -10.35) * mm, "end": v(110.99, -11.04) * mm});
            skLineSegment(sketch, "E1050", {"start": v(110.99, -11.04) * mm, "end": v(111.16, -12.08) * mm});
            skLineSegment(sketch, "E1051", {"start": v(111.16, -12.08) * mm, "end": v(111.16, -12.26) * mm});
            skLineSegment(sketch, "E1052", {"start": v(111.16, -12.26) * mm, "end": v(111.5, -13.82) * mm});
            skLineSegment(sketch, "E1053", {"start": v(111.5, -13.82) * mm, "end": v(112.38, -15.91) * mm});
            skLineSegment(sketch, "E1054", {"start": v(112.38, -15.91) * mm, "end": v(112.72, -16.78) * mm});
            skLineSegment(sketch, "E1055", {"start": v(112.72, -16.78) * mm, "end": v(112.72, -17.3) * mm});
            skLineSegment(sketch, "E1056", {"start": v(112.72, -17.3) * mm, "end": v(112.9, -18.17) * mm});
            skLineSegment(sketch, "E1057", {"start": v(112.9, -18.17) * mm, "end": v(113.25, -19.04) * mm});
            skLineSegment(sketch, "E1058", {"start": v(113.25, -19.04) * mm, "end": v(113.42, -19.74) * mm});
            skLineSegment(sketch, "E1059", {"start": v(113.42, -19.74) * mm, "end": v(113.77, -20.43) * mm});
            skLineSegment(sketch, "E1060", {"start": v(113.77, -20.43) * mm, "end": v(114.12, -21.65) * mm});
            skLineSegment(sketch, "E1061", {"start": v(114.12, -21.65) * mm, "end": v(114.29, -22.17) * mm});
            skLineSegment(sketch, "E1062", {"start": v(114.29, -22.17) * mm, "end": v(114.29, -22.52) * mm});
            skLineSegment(sketch, "E1063", {"start": v(114.29, -22.52) * mm, "end": v(114.12, -22.86) * mm});
            skLineSegment(sketch, "E1064", {"start": v(114.12, -22.86) * mm, "end": v(114.29, -23.21) * mm});
            skLineSegment(sketch, "E1065", {"start": v(114.29, -23.21) * mm, "end": v(114.29, -24.08) * mm});
            skLineSegment(sketch, "E1066", {"start": v(114.29, -24.08) * mm, "end": v(114.29, -24.26) * mm});
            skLineSegment(sketch, "E1067", {"start": v(114.29, -24.26) * mm, "end": v(114.29, -24.95) * mm});
            skLineSegment(sketch, "E1068", {"start": v(114.29, -24.95) * mm, "end": v(114.46, -26.86) * mm});
            skLineSegment(sketch, "E1069", {"start": v(114.46, -26.86) * mm, "end": v(114.46, -28.25) * mm});
            skLineSegment(sketch, "E1070", {"start": v(114.46, -28.25) * mm, "end": v(114.64, -28.6) * mm});
            skLineSegment(sketch, "E1071", {"start": v(114.64, -28.6) * mm, "end": v(114.81, -29.3) * mm});
            skLineSegment(sketch, "E1072", {"start": v(114.81, -29.3) * mm, "end": v(114.98, -30.69) * mm});
            skLineSegment(sketch, "E1073", {"start": v(114.98, -30.69) * mm, "end": v(114.98, -31.04) * mm});
            skLineSegment(sketch, "E1074", {"start": v(114.98, -31.04) * mm, "end": v(114.81, -31.38) * mm});
            skLineSegment(sketch, "E1075", {"start": v(114.81, -31.38) * mm, "end": v(114.81, -32.25) * mm});
            skLineSegment(sketch, "E1076", {"start": v(114.81, -32.25) * mm, "end": v(114.98, -33.3) * mm});
            skLineSegment(sketch, "E1077", {"start": v(114.98, -33.3) * mm, "end": v(114.98, -33.64) * mm});
            skLineSegment(sketch, "E1078", {"start": v(114.98, -33.64) * mm, "end": v(115.16, -34.69) * mm});
            skLineSegment(sketch, "E1079", {"start": v(115.16, -34.69) * mm, "end": v(115.16, -34.86) * mm});
            skLineSegment(sketch, "E1080", {"start": v(115.16, -34.86) * mm, "end": v(115.16, -35.04) * mm});
            skLineSegment(sketch, "E1081", {"start": v(115.16, -35.04) * mm, "end": v(115.16, -35.38) * mm});
            skLineSegment(sketch, "E1082", {"start": v(115.16, -35.38) * mm, "end": v(115.5, -37.47) * mm});
            skLineSegment(sketch, "E1083", {"start": v(115.5, -37.47) * mm, "end": v(115.68, -38.17) * mm});
            skLineSegment(sketch, "E1084", {"start": v(115.68, -38.17) * mm, "end": v(115.68, -38.34) * mm});
            skLineSegment(sketch, "E1085", {"start": v(115.68, -38.34) * mm, "end": v(115.68, -38.51) * mm});
            skLineSegment(sketch, "E1086", {"start": v(115.68, -38.51) * mm, "end": v(115.85, -38.69) * mm});
            skLineSegment(sketch, "E1087", {"start": v(115.85, -38.69) * mm, "end": v(116.2, -39.56) * mm});
            skLineSegment(sketch, "E1088", {"start": v(116.2, -39.56) * mm, "end": v(116.55, -41.64) * mm});
            skLineSegment(sketch, "E1089", {"start": v(116.55, -41.64) * mm, "end": v(116.72, -41.64) * mm});
            skLineSegment(sketch, "E1090", {"start": v(116.72, -41.64) * mm, "end": v(116.72, -42.16) * mm});
            skLineSegment(sketch, "E1091", {"start": v(116.72, -42.16) * mm, "end": v(117.07, -43.2) * mm});
            skLineSegment(sketch, "E1092", {"start": v(117.07, -43.2) * mm, "end": v(117.24, -43.38) * mm});
            skLineSegment(sketch, "E1093", {"start": v(117.24, -43.38) * mm, "end": v(117.24, -43.56) * mm});
            skLineSegment(sketch, "E1094", {"start": v(117.24, -43.56) * mm, "end": v(117.24, -44.25) * mm});
            skLineSegment(sketch, "E1095", {"start": v(117.24, -44.25) * mm, "end": v(117.42, -44.77) * mm});
            skLineSegment(sketch, "E1096", {"start": v(117.42, -44.77) * mm, "end": v(117.42, -45.3) * mm});
            skLineSegment(sketch, "E1097", {"start": v(117.42, -45.3) * mm, "end": v(117.6, -46.51) * mm});
            skLineSegment(sketch, "E1098", {"start": v(117.6, -46.51) * mm, "end": v(118.46, -47.56) * mm});
            skLineSegment(sketch, "E1099", {"start": v(118.46, -47.56) * mm, "end": v(118.64, -47.9) * mm});
            skLineSegment(sketch, "E1100", {"start": v(118.64, -47.9) * mm, "end": v(119.16, -49.12) * mm});
            skLineSegment(sketch, "E1101", {"start": v(119.16, -49.12) * mm, "end": v(119.33, -49.64) * mm});
            skLineSegment(sketch, "E1102", {"start": v(119.33, -49.64) * mm, "end": v(120.2, -51.2) * mm});
            skLineSegment(sketch, "E1103", {"start": v(120.2, -51.2) * mm, "end": v(120.37, -51.55) * mm});
            skLineSegment(sketch, "E1104", {"start": v(120.37, -51.55) * mm, "end": v(120.72, -52.25) * mm});
            skLineSegment(sketch, "E1105", {"start": v(120.72, -52.25) * mm, "end": v(120.9, -52.77) * mm});
            skLineSegment(sketch, "E1106", {"start": v(120.9, -52.77) * mm, "end": v(121.07, -52.95) * mm});
            skLineSegment(sketch, "E1107", {"start": v(121.07, -52.95) * mm, "end": v(121.24, -53.47) * mm});
            skLineSegment(sketch, "E1108", {"start": v(121.24, -53.47) * mm, "end": v(121.6, -53.64) * mm});
            skLineSegment(sketch, "E1109", {"start": v(121.6, -53.64) * mm, "end": v(121.6, -53.81) * mm});
            skLineSegment(sketch, "E1110", {"start": v(121.6, -53.81) * mm, "end": v(121.24, -53.99) * mm});
            skLineSegment(sketch, "E1111", {"start": v(121.24, -53.99) * mm, "end": v(121.24, -54.16) * mm});
            skLineSegment(sketch, "E1112", {"start": v(121.24, -54.16) * mm, "end": v(121.24, -54.34) * mm});
            skLineSegment(sketch, "E1113", {"start": v(121.24, -54.34) * mm, "end": v(121.24, -54.5) * mm});
            skLineSegment(sketch, "E1114", {"start": v(121.24, -54.5) * mm, "end": v(121.24, -54.68) * mm});
            skLineSegment(sketch, "E1115", {"start": v(121.24, -54.68) * mm, "end": v(121.24, -54.86) * mm});
            skLineSegment(sketch, "E1116", {"start": v(121.24, -54.86) * mm, "end": v(121.42, -55.03) * mm});
            skLineSegment(sketch, "E1117", {"start": v(121.42, -55.03) * mm, "end": v(121.42, -55.2) * mm});
            skLineSegment(sketch, "E1118", {"start": v(121.42, -55.2) * mm, "end": v(121.6, -55.38) * mm});
            skLineSegment(sketch, "E1119", {"start": v(121.6, -55.38) * mm, "end": v(121.94, -55.73) * mm});
            skLineSegment(sketch, "E1120", {"start": v(121.94, -55.73) * mm, "end": v(121.76, -56.25) * mm});
            skLineSegment(sketch, "E1121", {"start": v(121.76, -56.25) * mm, "end": v(121.76, -56.42) * mm});
            skLineSegment(sketch, "E1122", {"start": v(121.76, -56.42) * mm, "end": v(121.76, -56.6) * mm});
            skLineSegment(sketch, "E1123", {"start": v(121.76, -56.6) * mm, "end": v(121.6, -56.6) * mm});
            skLineSegment(sketch, "E1124", {"start": v(121.6, -56.6) * mm, "end": v(121.07, -57.64) * mm});
            skLineSegment(sketch, "E1125", {"start": v(121.07, -57.64) * mm, "end": v(120.55, -58.16) * mm});
            skLineSegment(sketch, "E1126", {"start": v(120.55, -58.16) * mm, "end": v(120.37, -58.5) * mm});
            skLineSegment(sketch, "E1127", {"start": v(120.37, -58.5) * mm, "end": v(120.03, -58.68) * mm});
            skLineSegment(sketch, "E1128", {"start": v(120.03, -58.68) * mm, "end": v(120.03, -58.86) * mm});
            skLineSegment(sketch, "E1129", {"start": v(120.03, -58.86) * mm, "end": v(119.68, -59.55) * mm});
            skLineSegment(sketch, "E1130", {"start": v(119.68, -59.55) * mm, "end": v(119.33, -60.94) * mm});
            skLineSegment(sketch, "E1131", {"start": v(119.33, -60.94) * mm, "end": v(119.16, -61.46) * mm});
            skLineSegment(sketch, "E1132", {"start": v(119.16, -61.46) * mm, "end": v(118.98, -61.99) * mm});
            skLineSegment(sketch, "E1133", {"start": v(118.98, -61.99) * mm, "end": v(118.98, -62.16) * mm});
            skLineSegment(sketch, "E1134", {"start": v(118.98, -62.16) * mm, "end": v(118.98, -62.5) * mm});
            skLineSegment(sketch, "E1135", {"start": v(118.98, -62.5) * mm, "end": v(118.98, -62.86) * mm});
            skLineSegment(sketch, "E1136", {"start": v(118.98, -62.86) * mm, "end": v(118.98, -63.03) * mm});
            skLineSegment(sketch, "E1137", {"start": v(118.98, -63.03) * mm, "end": v(118.98, -63.2) * mm});
            skLineSegment(sketch, "E1138", {"start": v(118.98, -63.2) * mm, "end": v(119.16, -64.6) * mm});
            skLineSegment(sketch, "E1139", {"start": v(119.16, -64.6) * mm, "end": v(118.98, -65.12) * mm});
            skLineSegment(sketch, "E1140", {"start": v(118.98, -65.12) * mm, "end": v(118.98, -65.98) * mm});
            skLineSegment(sketch, "E1141", {"start": v(118.98, -65.98) * mm, "end": v(118.8, -66.33) * mm});
            skLineSegment(sketch, "E1142", {"start": v(118.8, -66.33) * mm, "end": v(118.64, -67.03) * mm});
            skLineSegment(sketch, "E1143", {"start": v(118.64, -67.03) * mm, "end": v(118.64, -67.2) * mm});
            skLineSegment(sketch, "E1144", {"start": v(118.64, -67.2) * mm, "end": v(118.46, -67.55) * mm});
            skLineSegment(sketch, "E1145", {"start": v(118.46, -67.55) * mm, "end": v(118.46, -68.42) * mm});
            skLineSegment(sketch, "E1146", {"start": v(118.46, -68.42) * mm, "end": v(118.46, -68.6) * mm});
            skLineSegment(sketch, "E1147", {"start": v(118.46, -68.6) * mm, "end": v(118.46, -68.94) * mm});
            skLineSegment(sketch, "E1148", {"start": v(118.46, -68.94) * mm, "end": v(118.64, -69.29) * mm});
            skLineSegment(sketch, "E1149", {"start": v(118.64, -69.29) * mm, "end": v(118.98, -70.16) * mm});
            skLineSegment(sketch, "E1150", {"start": v(118.98, -70.16) * mm, "end": v(119.33, -71.38) * mm});
            skLineSegment(sketch, "E1151", {"start": v(119.33, -71.38) * mm, "end": v(119.33, -71.9) * mm});
            skLineSegment(sketch, "E1152", {"start": v(119.33, -71.9) * mm, "end": v(119.16, -72.42) * mm});
            skLineSegment(sketch, "E1153", {"start": v(119.16, -72.42) * mm, "end": v(118.46, -73.98) * mm});
            skLineSegment(sketch, "E1154", {"start": v(118.46, -73.98) * mm, "end": v(118.46, -74.33) * mm});
            skLineSegment(sketch, "E1155", {"start": v(118.46, -74.33) * mm, "end": v(118.46, -74.68) * mm});
            skLineSegment(sketch, "E1156", {"start": v(118.46, -74.68) * mm, "end": v(118.46, -75.2) * mm});
            skLineSegment(sketch, "E1157", {"start": v(118.46, -75.2) * mm, "end": v(118.46, -75.37) * mm});
            skLineSegment(sketch, "E1158", {"start": v(118.46, -75.37) * mm, "end": v(118.29, -75.55) * mm});
            skLineSegment(sketch, "E1159", {"start": v(118.29, -75.55) * mm, "end": v(117.94, -76.42) * mm});
            skLineSegment(sketch, "E1160", {"start": v(117.94, -76.42) * mm, "end": v(117.77, -76.77) * mm});
            skLineSegment(sketch, "E1161", {"start": v(117.77, -76.77) * mm, "end": v(117.07, -79.2) * mm});
            skLineSegment(sketch, "E1162", {"start": v(117.07, -79.2) * mm, "end": v(117.07, -80.07) * mm});
            skLineSegment(sketch, "E1163", {"start": v(117.07, -80.07) * mm, "end": v(117.24, -81.11) * mm});
            skLineSegment(sketch, "E1164", {"start": v(117.24, -81.11) * mm, "end": v(117.07, -81.46) * mm});
            skLineSegment(sketch, "E1165", {"start": v(117.07, -81.46) * mm, "end": v(116.9, -82.33) * mm});
            skLineSegment(sketch, "E1166", {"start": v(116.9, -82.33) * mm, "end": v(116.9, -82.5) * mm});
            skLineSegment(sketch, "E1167", {"start": v(116.9, -82.5) * mm, "end": v(116.72, -82.85) * mm});
            skLineSegment(sketch, "E1168", {"start": v(116.72, -82.85) * mm, "end": v(116.72, -83.03) * mm});
            skLineSegment(sketch, "E1169", {"start": v(116.72, -83.03) * mm, "end": v(116.55, -83.37) * mm});
            skLineSegment(sketch, "E1170", {"start": v(116.55, -83.37) * mm, "end": v(115.16, -84.6) * mm});
            skLineSegment(sketch, "E1171", {"start": v(115.16, -84.6) * mm, "end": v(114.98, -84.76) * mm});
            skLineSegment(sketch, "E1172", {"start": v(114.98, -84.76) * mm, "end": v(114.81, -85.28) * mm});
            skLineSegment(sketch, "E1173", {"start": v(114.81, -85.28) * mm, "end": v(113.94, -85.98) * mm});
            skLineSegment(sketch, "E1174", {"start": v(113.94, -85.98) * mm, "end": v(113.6, -86.5) * mm});
            skLineSegment(sketch, "E1175", {"start": v(113.6, -86.5) * mm, "end": v(113.42, -86.68) * mm});
            skLineSegment(sketch, "E1176", {"start": v(113.42, -86.68) * mm, "end": v(113.25, -87.55) * mm});
            skLineSegment(sketch, "E1177", {"start": v(113.25, -87.55) * mm, "end": v(112.9, -87.72) * mm});
            skLineSegment(sketch, "E1178", {"start": v(112.9, -87.72) * mm, "end": v(112.03, -87.9) * mm});
            skLineSegment(sketch, "E1179", {"start": v(112.03, -87.9) * mm, "end": v(111.68, -87.72) * mm});
            skLineSegment(sketch, "E1180", {"start": v(111.68, -87.72) * mm, "end": v(111.5, -87.55) * mm});
            skLineSegment(sketch, "E1181", {"start": v(111.5, -87.55) * mm, "end": v(110.99, -87.37) * mm});
            skLineSegment(sketch, "E1182", {"start": v(110.99, -87.37) * mm, "end": v(110.47, -87.37) * mm});
            skLineSegment(sketch, "E1183", {"start": v(110.47, -87.37) * mm, "end": v(110.12, -87.55) * mm});
            skLineSegment(sketch, "E1184", {"start": v(110.12, -87.55) * mm, "end": v(110.16, -87.17) * mm});
            skLineSegment(sketch, "E1185", {"start": v(110.16, -87.17) * mm, "end": v(110.1, -87.16) * mm});
            skLineSegment(sketch, "E1186", {"start": v(110.1, -87.16) * mm, "end": v(110.03, -87.16) * mm});
            skLineSegment(sketch, "E1187", {"start": v(110.03, -87.16) * mm, "end": v(109.96, -87.16) * mm});
            skLineSegment(sketch, "E1188", {"start": v(109.96, -87.16) * mm, "end": v(109.9, -87.16) * mm});
            skLineSegment(sketch, "E1189", {"start": v(109.9, -87.16) * mm, "end": v(109.84, -87.17) * mm});
            skLineSegment(sketch, "E1190", {"start": v(109.84, -87.17) * mm, "end": v(109.78, -87.19) * mm});
            skLineSegment(sketch, "E1191", {"start": v(109.78, -87.19) * mm, "end": v(109.65, -87.23) * mm});
            skLineSegment(sketch, "E1192", {"start": v(109.65, -87.23) * mm, "end": v(109.54, -87.28) * mm});
            skLineSegment(sketch, "E1193", {"start": v(109.54, -87.28) * mm, "end": v(109.42, -87.35) * mm});
            skLineSegment(sketch, "E1194", {"start": v(109.42, -87.35) * mm, "end": v(109.3, -87.42) * mm});
            skLineSegment(sketch, "E1195", {"start": v(109.3, -87.42) * mm, "end": v(109.2, -87.5) * mm});
            skLineSegment(sketch, "E1196", {"start": v(109.2, -87.5) * mm, "end": v(109, -87.65) * mm});
            skLineSegment(sketch, "E1197", {"start": v(109, -87.65) * mm, "end": v(108.84, -87.8) * mm});
            skLineSegment(sketch, "E1198", {"start": v(108.84, -87.8) * mm, "end": v(108.76, -87.86) * mm});
            skLineSegment(sketch, "E1199", {"start": v(108.76, -87.86) * mm, "end": v(108.7, -87.91) * mm});
            skLineSegment(sketch, "E1200", {"start": v(108.7, -87.91) * mm, "end": v(108.63, -87.95) * mm});
            skLineSegment(sketch, "E1201", {"start": v(108.63, -87.95) * mm, "end": v(108.58, -87.97) * mm});
            skLineSegment(sketch, "E1202", {"start": v(108.58, -87.97) * mm, "end": v(108, -87.47) * mm});
            skLineSegment(sketch, "E1203", {"start": v(108, -87.47) * mm, "end": v(107.86, -87.37) * mm});
            skLineSegment(sketch, "E1204", {"start": v(107.86, -87.37) * mm, "end": v(107.86, -85.98) * mm});
            skLineSegment(sketch, "E1205", {"start": v(107.86, -85.98) * mm, "end": v(107.51, -85.11) * mm});
            skLineSegment(sketch, "E1206", {"start": v(107.51, -85.11) * mm, "end": v(106.81, -85.28) * mm});
            skLineSegment(sketch, "E1207", {"start": v(106.81, -85.28) * mm, "end": v(106.12, -84.94) * mm});
            skLineSegment(sketch, "E1208", {"start": v(106.12, -84.94) * mm, "end": v(106.12, -84.42) * mm});
            skLineSegment(sketch, "E1209", {"start": v(106.12, -84.42) * mm, "end": v(106.64, -83.72) * mm});
            skLineSegment(sketch, "E1210", {"start": v(106.64, -83.72) * mm, "end": v(107.68, -83.55) * mm});
            skLineSegment(sketch, "E1211", {"start": v(107.68, -83.55) * mm, "end": v(107.68, -82.85) * mm});
            skLineSegment(sketch, "E1212", {"start": v(107.68, -82.85) * mm, "end": v(107.34, -82.33) * mm});
            skLineSegment(sketch, "E1213", {"start": v(107.34, -82.33) * mm, "end": v(107.34, -82.16) * mm});
            skLineSegment(sketch, "E1214", {"start": v(107.34, -82.16) * mm, "end": v(108.38, -81.46) * mm});
            skLineSegment(sketch, "E1215", {"start": v(108.38, -81.46) * mm, "end": v(109.25, -81.63) * mm});
            skLineSegment(sketch, "E1216", {"start": v(109.25, -81.63) * mm, "end": v(109.42, -81.63) * mm});
            skLineSegment(sketch, "E1217", {"start": v(109.42, -81.63) * mm, "end": v(109.6, -81.8) * mm});
            skLineSegment(sketch, "E1218", {"start": v(109.6, -81.8) * mm, "end": v(109.77, -81.8) * mm});
            skLineSegment(sketch, "E1219", {"start": v(109.77, -81.8) * mm, "end": v(110.47, -81.11) * mm});
            skLineSegment(sketch, "E1220", {"start": v(110.47, -81.11) * mm, "end": v(110.47, -80.94) * mm});
            skLineSegment(sketch, "E1221", {"start": v(110.47, -80.94) * mm, "end": v(110.81, -80.6) * mm});
            skLineSegment(sketch, "E1222", {"start": v(110.81, -80.6) * mm, "end": v(110.81, -80.24) * mm});
            skLineSegment(sketch, "E1223", {"start": v(110.81, -80.24) * mm, "end": v(110.99, -79.9) * mm});
            skLineSegment(sketch, "E1224", {"start": v(110.99, -79.9) * mm, "end": v(110.99, -79.72) * mm});
            skLineSegment(sketch, "E1225", {"start": v(110.99, -79.72) * mm, "end": v(110.81, -79.2) * mm});
            skLineSegment(sketch, "E1226", {"start": v(110.81, -79.2) * mm, "end": v(110.64, -78.85) * mm});
            skLineSegment(sketch, "E1227", {"start": v(110.64, -78.85) * mm, "end": v(110.47, -78.68) * mm});
            skLineSegment(sketch, "E1228", {"start": v(110.47, -78.68) * mm, "end": v(110.3, -78.5) * mm});
            skLineSegment(sketch, "E1229", {"start": v(110.3, -78.5) * mm, "end": v(109.94, -78.5) * mm});
            skLineSegment(sketch, "E1230", {"start": v(109.94, -78.5) * mm, "end": v(109.07, -78.33) * mm});
            skLineSegment(sketch, "E1231", {"start": v(109.07, -78.33) * mm, "end": v(108.9, -78.33) * mm});
            skLineSegment(sketch, "E1232", {"start": v(108.9, -78.33) * mm, "end": v(108.73, -78.16) * mm});
            skLineSegment(sketch, "E1233", {"start": v(108.73, -78.16) * mm, "end": v(108.03, -77.63) * mm});
            skLineSegment(sketch, "E1234", {"start": v(108.03, -77.63) * mm, "end": v(107.51, -77.46) * mm});
            skLineSegment(sketch, "E1235", {"start": v(107.51, -77.46) * mm, "end": v(106.64, -77.46) * mm});
            skLineSegment(sketch, "E1236", {"start": v(106.64, -77.46) * mm, "end": v(106.3, -77.98) * mm});
            skLineSegment(sketch, "E1237", {"start": v(106.3, -77.98) * mm, "end": v(105.25, -77.98) * mm});
            skLineSegment(sketch, "E1238", {"start": v(105.25, -77.98) * mm, "end": v(104.73, -78.33) * mm});
            skLineSegment(sketch, "E1239", {"start": v(104.73, -78.33) * mm, "end": v(104.38, -78.68) * mm});
            skLineSegment(sketch, "E1240", {"start": v(104.38, -78.68) * mm, "end": v(103.69, -79.03) * mm});
            skLineSegment(sketch, "E1241", {"start": v(103.69, -79.03) * mm, "end": v(103.51, -79.37) * mm});
            skLineSegment(sketch, "E1242", {"start": v(103.51, -79.37) * mm, "end": v(103.34, -79.55) * mm});
            skLineSegment(sketch, "E1243", {"start": v(103.34, -79.55) * mm, "end": v(103.16, -80.07) * mm});
            skLineSegment(sketch, "E1244", {"start": v(103.16, -80.07) * mm, "end": v(103, -80.24) * mm});
            skLineSegment(sketch, "E1245", {"start": v(103, -80.24) * mm, "end": v(102.3, -80.42) * mm});
            skLineSegment(sketch, "E1246", {"start": v(102.3, -80.42) * mm, "end": v(101.95, -80.24) * mm});
            skLineSegment(sketch, "E1247", {"start": v(101.95, -80.24) * mm, "end": v(101.6, -80.24) * mm});
            skLineSegment(sketch, "E1248", {"start": v(101.6, -80.24) * mm, "end": v(101.43, -80.24) * mm});
            skLineSegment(sketch, "E1249", {"start": v(101.43, -80.24) * mm, "end": v(100.73, -80.94) * mm});
            skLineSegment(sketch, "E1250", {"start": v(100.73, -80.94) * mm, "end": v(100.56, -81.29) * mm});
            skLineSegment(sketch, "E1251", {"start": v(100.56, -81.29) * mm, "end": v(100.38, -81.29) * mm});
            skLineSegment(sketch, "E1252", {"start": v(100.38, -81.29) * mm, "end": v(100.38, -81.46) * mm});
            skLineSegment(sketch, "E1253", {"start": v(100.38, -81.46) * mm, "end": v(100.2, -81.98) * mm});
            skLineSegment(sketch, "E1254", {"start": v(100.2, -81.98) * mm, "end": v(100.2, -82.16) * mm});
            skLineSegment(sketch, "E1255", {"start": v(100.2, -82.16) * mm, "end": v(100.2, -82.33) * mm});
            skLineSegment(sketch, "E1256", {"start": v(100.2, -82.33) * mm, "end": v(100.2, -83.03) * mm});
            skLineSegment(sketch, "E1257", {"start": v(100.2, -83.03) * mm, "end": v(100.73, -83.55) * mm});
            skLineSegment(sketch, "E1258", {"start": v(100.73, -83.55) * mm, "end": v(101.08, -83.72) * mm});
            skLineSegment(sketch, "E1259", {"start": v(101.08, -83.72) * mm, "end": v(101.95, -84.07) * mm});
            skLineSegment(sketch, "E1260", {"start": v(101.95, -84.07) * mm, "end": v(101.95, -84.42) * mm});
            skLineSegment(sketch, "E1261", {"start": v(101.95, -84.42) * mm, "end": v(101.95, -84.76) * mm});
            skLineSegment(sketch, "E1262", {"start": v(101.95, -84.76) * mm, "end": v(101.95, -85.63) * mm});
            skLineSegment(sketch, "E1263", {"start": v(101.95, -85.63) * mm, "end": v(102.3, -86.33) * mm});
            skLineSegment(sketch, "E1264", {"start": v(102.3, -86.33) * mm, "end": v(102.3, -86.85) * mm});
            skLineSegment(sketch, "E1265", {"start": v(102.3, -86.85) * mm, "end": v(102.12, -87.02) * mm});
            skLineSegment(sketch, "E1266", {"start": v(102.12, -87.02) * mm, "end": v(101.95, -86.68) * mm});
            skLineSegment(sketch, "E1267", {"start": v(101.95, -86.68) * mm, "end": v(101.43, -86.5) * mm});
            skLineSegment(sketch, "E1268", {"start": v(101.43, -86.5) * mm, "end": v(100.73, -86.5) * mm});
            skLineSegment(sketch, "E1269", {"start": v(100.73, -86.5) * mm, "end": v(100.56, -86.5) * mm});
            skLineSegment(sketch, "E1270", {"start": v(100.56, -86.5) * mm, "end": v(100.38, -86.5) * mm});
            skLineSegment(sketch, "E1271", {"start": v(100.38, -86.5) * mm, "end": v(100.2, -86.5) * mm});
            skLineSegment(sketch, "E1272", {"start": v(100.2, -86.5) * mm, "end": v(99.51, -86.68) * mm});
            skLineSegment(sketch, "E1273", {"start": v(99.51, -86.68) * mm, "end": v(99.34, -86.85) * mm});
            skLineSegment(sketch, "E1274", {"start": v(99.34, -86.85) * mm, "end": v(99.17, -86.85) * mm});
            skLineSegment(sketch, "E1275", {"start": v(99.17, -86.85) * mm, "end": v(99.17, -87.02) * mm});
            skLineSegment(sketch, "E1276", {"start": v(99.17, -87.02) * mm, "end": v(98.82, -87.2) * mm});
            skLineSegment(sketch, "E1277", {"start": v(98.82, -87.2) * mm, "end": v(98.82, -87.37) * mm});
            skLineSegment(sketch, "E1278", {"start": v(98.82, -87.37) * mm, "end": v(98.64, -87.37) * mm});
            skLineSegment(sketch, "E1279", {"start": v(98.64, -87.37) * mm, "end": v(98.64, -87.72) * mm});
            skLineSegment(sketch, "E1280", {"start": v(98.64, -87.72) * mm, "end": v(98.47, -88.24) * mm});
            skLineSegment(sketch, "E1281", {"start": v(98.47, -88.24) * mm, "end": v(98.12, -88.76) * mm});
            skLineSegment(sketch, "E1282", {"start": v(98.12, -88.76) * mm, "end": v(97.95, -88.94) * mm});
            skLineSegment(sketch, "E1283", {"start": v(97.95, -88.94) * mm, "end": v(97.6, -89.46) * mm});
            skLineSegment(sketch, "E1284", {"start": v(97.6, -89.46) * mm, "end": v(97.43, -89.63) * mm});
            skLineSegment(sketch, "E1285", {"start": v(97.43, -89.63) * mm, "end": v(97.43, -89.8) * mm});
            skLineSegment(sketch, "E1286", {"start": v(97.43, -89.8) * mm, "end": v(97.43, -89.98) * mm});
            skLineSegment(sketch, "E1287", {"start": v(97.43, -89.98) * mm, "end": v(97.25, -90.15) * mm});
            skLineSegment(sketch, "E1288", {"start": v(97.25, -90.15) * mm, "end": v(97.25, -90.33) * mm});
            skLineSegment(sketch, "E1289", {"start": v(97.25, -90.33) * mm, "end": v(97.08, -91.02) * mm});
            skLineSegment(sketch, "E1290", {"start": v(97.08, -91.02) * mm, "end": v(96.9, -91.37) * mm});
            skLineSegment(sketch, "E1291", {"start": v(96.9, -91.37) * mm, "end": v(96.9, -91.72) * mm});
            skLineSegment(sketch, "E1292", {"start": v(96.9, -91.72) * mm, "end": v(96.9, -91.9) * mm});
            skLineSegment(sketch, "E1293", {"start": v(96.9, -91.9) * mm, "end": v(96.9, -92.07) * mm});
            skLineSegment(sketch, "E1294", {"start": v(96.9, -92.07) * mm, "end": v(96.9, -92.59) * mm});
            skLineSegment(sketch, "E1295", {"start": v(96.9, -92.59) * mm, "end": v(96.9, -92.76) * mm});
            skLineSegment(sketch, "E1296", {"start": v(96.9, -92.76) * mm, "end": v(96.9, -92.94) * mm});
            skLineSegment(sketch, "E1297", {"start": v(96.9, -92.94) * mm, "end": v(96.9, -93.28) * mm});
            skLineSegment(sketch, "E1298", {"start": v(96.9, -93.28) * mm, "end": v(96.9, -93.46) * mm});
            skLineSegment(sketch, "E1299", {"start": v(96.9, -93.46) * mm, "end": v(96.9, -93.63) * mm});
            skLineSegment(sketch, "E1300", {"start": v(96.9, -93.63) * mm, "end": v(96.9, -93.8) * mm});
            skLineSegment(sketch, "E1301", {"start": v(96.9, -93.8) * mm, "end": v(96.9, -93.98) * mm});
            skLineSegment(sketch, "E1302", {"start": v(96.9, -93.98) * mm, "end": v(96.9, -94.15) * mm});
            skLineSegment(sketch, "E1303", {"start": v(96.9, -94.15) * mm, "end": v(97.08, -94.5) * mm});
            skLineSegment(sketch, "E1304", {"start": v(97.08, -94.5) * mm, "end": v(97.43, -95.02) * mm});
            skLineSegment(sketch, "E1305", {"start": v(97.43, -95.02) * mm, "end": v(97.6, -95.54) * mm});
            skLineSegment(sketch, "E1306", {"start": v(97.6, -95.54) * mm, "end": v(97.43, -96.41) * mm});
            skLineSegment(sketch, "E1307", {"start": v(97.43, -96.41) * mm, "end": v(96.9, -98.15) * mm});
            skLineSegment(sketch, "E1308", {"start": v(96.9, -98.15) * mm, "end": v(96.73, -98.67) * mm});
            skLineSegment(sketch, "E1309", {"start": v(96.73, -98.67) * mm, "end": v(96.73, -98.85) * mm});
            skLineSegment(sketch, "E1310", {"start": v(96.73, -98.85) * mm, "end": v(96.73, -99.37) * mm});
            skLineSegment(sketch, "E1311", {"start": v(96.73, -99.37) * mm, "end": v(96.39, -100.06) * mm});
            skLineSegment(sketch, "E1312", {"start": v(96.39, -100.06) * mm, "end": v(96.21, -100.41) * mm});
            skLineSegment(sketch, "E1313", {"start": v(96.21, -100.41) * mm, "end": v(96.04, -100.41) * mm});
            skLineSegment(sketch, "E1314", {"start": v(96.04, -100.41) * mm, "end": v(95.7, -100.59) * mm});
            skLineSegment(sketch, "E1315", {"start": v(95.7, -100.59) * mm, "end": v(95.34, -100.93) * mm});
            skLineSegment(sketch, "E1316", {"start": v(95.34, -100.93) * mm, "end": v(95.17, -100.93) * mm});
            skLineSegment(sketch, "E1317", {"start": v(95.17, -100.93) * mm, "end": v(95, -101.28) * mm});
            skLineSegment(sketch, "E1318", {"start": v(95, -101.28) * mm, "end": v(94.82, -101.63) * mm});
            skLineSegment(sketch, "E1319", {"start": v(94.82, -101.63) * mm, "end": v(94.82, -101.8) * mm});
            skLineSegment(sketch, "E1320", {"start": v(94.82, -101.8) * mm, "end": v(94.47, -102.33) * mm});
            skLineSegment(sketch, "E1321", {"start": v(94.47, -102.33) * mm, "end": v(94.82, -102.85) * mm});
            skLineSegment(sketch, "E1322", {"start": v(94.82, -102.85) * mm, "end": v(94.3, -103.02) * mm});
            skLineSegment(sketch, "E1323", {"start": v(94.3, -103.02) * mm, "end": v(93.95, -103.2) * mm});
            skLineSegment(sketch, "E1324", {"start": v(93.95, -103.2) * mm, "end": v(93.78, -103.2) * mm});
            skLineSegment(sketch, "E1325", {"start": v(93.78, -103.2) * mm, "end": v(93.6, -103.2) * mm});
            skLineSegment(sketch, "E1326", {"start": v(93.6, -103.2) * mm, "end": v(93.43, -103.37) * mm});
            skLineSegment(sketch, "E1327", {"start": v(93.43, -103.37) * mm, "end": v(93.26, -103.54) * mm});
            skLineSegment(sketch, "E1328", {"start": v(93.26, -103.54) * mm, "end": v(92.9, -103.89) * mm});
            skLineSegment(sketch, "E1329", {"start": v(92.9, -103.89) * mm, "end": v(91.52, -104.41) * mm});
            skLineSegment(sketch, "E1330", {"start": v(91.52, -104.41) * mm, "end": v(91.17, -104.41) * mm});
            skLineSegment(sketch, "E1331", {"start": v(91.17, -104.41) * mm, "end": v(90.13, -104.59) * mm});
            skLineSegment(sketch, "E1332", {"start": v(90.13, -104.59) * mm, "end": v(89.6, -104.59) * mm});
            skLineSegment(sketch, "E1333", {"start": v(89.6, -104.59) * mm, "end": v(89.26, -104.76) * mm});
            skLineSegment(sketch, "E1334", {"start": v(89.26, -104.76) * mm, "end": v(88.39, -105.1) * mm});
            skLineSegment(sketch, "E1335", {"start": v(88.39, -105.1) * mm, "end": v(87.87, -105.28) * mm});
            skLineSegment(sketch, "E1336", {"start": v(87.87, -105.28) * mm, "end": v(87.17, -105.63) * mm});
            skLineSegment(sketch, "E1337", {"start": v(87.17, -105.63) * mm, "end": v(86.48, -105.98) * mm});
            skLineSegment(sketch, "E1338", {"start": v(86.48, -105.98) * mm, "end": v(86.48, -106.15) * mm});
            skLineSegment(sketch, "E1339", {"start": v(86.48, -106.15) * mm, "end": v(86.3, -106.32) * mm});
            skLineSegment(sketch, "E1340", {"start": v(86.3, -106.32) * mm, "end": v(85.6, -107.2) * mm});
            skLineSegment(sketch, "E1341", {"start": v(85.6, -107.2) * mm, "end": v(85.26, -107.72) * mm});
            skLineSegment(sketch, "E1342", {"start": v(85.26, -107.72) * mm, "end": v(85.26, -107.89) * mm});
            skLineSegment(sketch, "E1343", {"start": v(85.26, -107.89) * mm, "end": v(84.57, -109.8) * mm});
            skLineSegment(sketch, "E1344", {"start": v(84.57, -109.8) * mm, "end": v(84.4, -110.15) * mm});
            skLineSegment(sketch, "E1345", {"start": v(84.4, -110.15) * mm, "end": v(84.04, -111.02) * mm});
            skLineSegment(sketch, "E1346", {"start": v(84.04, -111.02) * mm, "end": v(83.7, -111.54) * mm});
            skLineSegment(sketch, "E1347", {"start": v(83.7, -111.54) * mm, "end": v(83.7, -111.89) * mm});
            skLineSegment(sketch, "E1348", {"start": v(83.7, -111.89) * mm, "end": v(83.52, -113.8) * mm});
            skLineSegment(sketch, "E1349", {"start": v(83.52, -113.8) * mm, "end": v(83.52, -114.15) * mm});
            skLineSegment(sketch, "E1350", {"start": v(83.52, -114.15) * mm, "end": v(83.35, -116.23) * mm});
            skLineSegment(sketch, "E1351", {"start": v(83.35, -116.23) * mm, "end": v(83.35, -116.4) * mm});
            skLineSegment(sketch, "E1352", {"start": v(83.35, -116.4) * mm, "end": v(83.7, -118.15) * mm});
            skLineSegment(sketch, "E1353", {"start": v(83.7, -118.15) * mm, "end": v(84.04, -119.2) * mm});
            skLineSegment(sketch, "E1354", {"start": v(84.04, -119.2) * mm, "end": v(84.04, -119.71) * mm});
            skLineSegment(sketch, "E1355", {"start": v(84.04, -119.71) * mm, "end": v(84.22, -119.89) * mm});
            skLineSegment(sketch, "E1356", {"start": v(84.22, -119.89) * mm, "end": v(83.52, -122.67) * mm});
            skLineSegment(sketch, "E1357", {"start": v(83.52, -122.67) * mm, "end": v(82.13, -123.02) * mm});
            skLineSegment(sketch, "E1358", {"start": v(82.13, -123.02) * mm, "end": v(81.61, -123.89) * mm});
            skLineSegment(sketch, "E1359", {"start": v(81.61, -123.89) * mm, "end": v(81.44, -123.89) * mm});
            skLineSegment(sketch, "E1360", {"start": v(81.44, -123.89) * mm, "end": v(80.57, -124.4) * mm});
            skLineSegment(sketch, "E1361", {"start": v(80.57, -124.4) * mm, "end": v(80.4, -124.75) * mm});
            skLineSegment(sketch, "E1362", {"start": v(80.4, -124.75) * mm, "end": v(80.57, -124.75) * mm});
            skLineSegment(sketch, "E1363", {"start": v(80.57, -124.75) * mm, "end": v(80.74, -125.45) * mm});
            skLineSegment(sketch, "E1364", {"start": v(80.74, -125.45) * mm, "end": v(80.57, -126.67) * mm});
            skLineSegment(sketch, "E1365", {"start": v(80.57, -126.67) * mm, "end": v(80.57, -127.02) * mm});
            skLineSegment(sketch, "E1366", {"start": v(80.57, -127.02) * mm, "end": v(80.74, -127.19) * mm});
            skLineSegment(sketch, "E1367", {"start": v(80.74, -127.19) * mm, "end": v(80.91, -127.88) * mm});
            skLineSegment(sketch, "E1368", {"start": v(80.91, -127.88) * mm, "end": v(80.57, -128.75) * mm});
            skLineSegment(sketch, "E1369", {"start": v(80.57, -128.75) * mm, "end": v(80.4, -128.93) * mm});
            skLineSegment(sketch, "E1370", {"start": v(80.4, -128.93) * mm, "end": v(79.35, -128.93) * mm});
            skLineSegment(sketch, "E1371", {"start": v(79.35, -128.93) * mm, "end": v(79.35, -129.62) * mm});
            skLineSegment(sketch, "E1372", {"start": v(79.35, -129.62) * mm, "end": v(79, -130.32) * mm});
            skLineSegment(sketch, "E1373", {"start": v(79, -130.32) * mm, "end": v(78.66, -130.14) * mm});
            skLineSegment(sketch, "E1374", {"start": v(78.66, -130.14) * mm, "end": v(78.3, -130.32) * mm});
            skLineSegment(sketch, "E1375", {"start": v(78.3, -130.32) * mm, "end": v(77.44, -131.19) * mm});
            skLineSegment(sketch, "E1376", {"start": v(77.44, -131.19) * mm, "end": v(77.26, -131.54) * mm});
            skLineSegment(sketch, "E1377", {"start": v(77.26, -131.54) * mm, "end": v(76.92, -132.06) * mm});
            skLineSegment(sketch, "E1378", {"start": v(76.92, -132.06) * mm, "end": v(76.74, -132.4) * mm});
            skLineSegment(sketch, "E1379", {"start": v(76.74, -132.4) * mm, "end": v(76.74, -133.1) * mm});
            skLineSegment(sketch, "E1380", {"start": v(76.74, -133.1) * mm, "end": v(76.57, -133.45) * mm});
            skLineSegment(sketch, "E1381", {"start": v(76.57, -133.45) * mm, "end": v(76.05, -133.97) * mm});
            skLineSegment(sketch, "E1382", {"start": v(76.05, -133.97) * mm, "end": v(75.7, -133.8) * mm});
            skLineSegment(sketch, "E1383", {"start": v(75.7, -133.8) * mm, "end": v(75.18, -133.62) * mm});
            skLineSegment(sketch, "E1384", {"start": v(75.18, -133.62) * mm, "end": v(74.83, -133.62) * mm});
            skLineSegment(sketch, "E1385", {"start": v(74.83, -133.62) * mm, "end": v(74.66, -133.62) * mm});
            skLineSegment(sketch, "E1386", {"start": v(74.66, -133.62) * mm, "end": v(74.3, -133.62) * mm});
            skLineSegment(sketch, "E1387", {"start": v(74.3, -133.62) * mm, "end": v(74.14, -133.8) * mm});
            skLineSegment(sketch, "E1388", {"start": v(74.14, -133.8) * mm, "end": v(73.96, -133.97) * mm});
            skLineSegment(sketch, "E1389", {"start": v(73.96, -133.97) * mm, "end": v(73.79, -133.97) * mm});
            skLineSegment(sketch, "E1390", {"start": v(73.79, -133.97) * mm, "end": v(73.79, -134.14) * mm});
            skLineSegment(sketch, "E1391", {"start": v(73.79, -134.14) * mm, "end": v(73.61, -134.32) * mm});
            skLineSegment(sketch, "E1392", {"start": v(73.61, -134.32) * mm, "end": v(73.44, -134.32) * mm});
            skLineSegment(sketch, "E1393", {"start": v(73.44, -134.32) * mm, "end": v(73.1, -135.01) * mm});
            skLineSegment(sketch, "E1394", {"start": v(73.1, -135.01) * mm, "end": v(72.92, -135.01) * mm});
            skLineSegment(sketch, "E1395", {"start": v(72.92, -135.01) * mm, "end": v(72.92, -135.19) * mm});
            skLineSegment(sketch, "E1396", {"start": v(72.92, -135.19) * mm, "end": v(72.57, -136.23) * mm});
            skLineSegment(sketch, "E1397", {"start": v(72.57, -136.23) * mm, "end": v(72.57, -136.4) * mm});
            skLineSegment(sketch, "E1398", {"start": v(72.57, -136.4) * mm, "end": v(72.57, -137.27) * mm});
            skLineSegment(sketch, "E1399", {"start": v(72.57, -137.27) * mm, "end": v(72.57, -137.45) * mm});
            skLineSegment(sketch, "E1400", {"start": v(72.57, -137.45) * mm, "end": v(72.4, -137.62) * mm});
            skLineSegment(sketch, "E1401", {"start": v(72.4, -137.62) * mm, "end": v(72.22, -138.32) * mm});
            skLineSegment(sketch, "E1402", {"start": v(72.22, -138.32) * mm, "end": v(72.22, -138.5) * mm});
            skLineSegment(sketch, "E1403", {"start": v(72.22, -138.5) * mm, "end": v(71.88, -138.66) * mm});
            skLineSegment(sketch, "E1404", {"start": v(71.88, -138.66) * mm, "end": v(71.7, -138.84) * mm});
            skLineSegment(sketch, "E1405", {"start": v(71.7, -138.84) * mm, "end": v(71.35, -139.19) * mm});
            skLineSegment(sketch, "E1406", {"start": v(71.35, -139.19) * mm, "end": v(71.18, -139.36) * mm});
            skLineSegment(sketch, "E1407", {"start": v(71.18, -139.36) * mm, "end": v(70.83, -139.53) * mm});
            skLineSegment(sketch, "E1408", {"start": v(70.83, -139.53) * mm, "end": v(70.66, -139.36) * mm});
            skLineSegment(sketch, "E1409", {"start": v(70.66, -139.36) * mm, "end": v(70.49, -138.84) * mm});
            skLineSegment(sketch, "E1410", {"start": v(70.49, -138.84) * mm, "end": v(70.14, -139.01) * mm});
            skLineSegment(sketch, "E1411", {"start": v(70.14, -139.01) * mm, "end": v(69.96, -139.01) * mm});
            skLineSegment(sketch, "E1412", {"start": v(69.96, -139.01) * mm, "end": v(69.96, -139.19) * mm});
            skLineSegment(sketch, "E1413", {"start": v(69.96, -139.19) * mm, "end": v(69.44, -139.88) * mm});
            skLineSegment(sketch, "E1414", {"start": v(69.44, -139.88) * mm, "end": v(69.27, -140.23) * mm});
            skLineSegment(sketch, "E1415", {"start": v(69.27, -140.23) * mm, "end": v(69.27, -140.4) * mm});
            skLineSegment(sketch, "E1416", {"start": v(69.27, -140.4) * mm, "end": v(69.1, -140.4) * mm});
            skLineSegment(sketch, "E1417", {"start": v(69.1, -140.4) * mm, "end": v(68.4, -142.14) * mm});
            skLineSegment(sketch, "E1418", {"start": v(68.4, -142.14) * mm, "end": v(68.05, -142.49) * mm});
            skLineSegment(sketch, "E1419", {"start": v(68.05, -142.49) * mm, "end": v(67.7, -142.84) * mm});
            skLineSegment(sketch, "E1420", {"start": v(67.7, -142.84) * mm, "end": v(67.18, -143.01) * mm});
            skLineSegment(sketch, "E1421", {"start": v(67.18, -143.01) * mm, "end": v(67, -143.01) * mm});
            skLineSegment(sketch, "E1422", {"start": v(67, -143.01) * mm, "end": v(67, -143.19) * mm});
            skLineSegment(sketch, "E1423", {"start": v(67, -143.19) * mm, "end": v(66.84, -143.36) * mm});
            skLineSegment(sketch, "E1424", {"start": v(66.84, -143.36) * mm, "end": v(66.84, -143.53) * mm});
            skLineSegment(sketch, "E1425", {"start": v(66.84, -143.53) * mm, "end": v(66.66, -143.88) * mm});
            skLineSegment(sketch, "E1426", {"start": v(66.66, -143.88) * mm, "end": v(66.66, -144.4) * mm});
            skLineSegment(sketch, "E1427", {"start": v(66.66, -144.4) * mm, "end": v(66.66, -144.58) * mm});
            skLineSegment(sketch, "E1428", {"start": v(66.66, -144.58) * mm, "end": v(66.66, -145.1) * mm});
            skLineSegment(sketch, "E1429", {"start": v(66.66, -145.1) * mm, "end": v(66.66, -145.27) * mm});
            skLineSegment(sketch, "E1430", {"start": v(66.66, -145.27) * mm, "end": v(66.66, -145.45) * mm});
            skLineSegment(sketch, "E1431", {"start": v(66.66, -145.45) * mm, "end": v(66.66, -145.62) * mm});
            skLineSegment(sketch, "E1432", {"start": v(66.66, -145.62) * mm, "end": v(66.66, -145.8) * mm});
            skLineSegment(sketch, "E1433", {"start": v(66.66, -145.8) * mm, "end": v(66.66, -145.97) * mm});
            skLineSegment(sketch, "E1434", {"start": v(66.66, -145.97) * mm, "end": v(66.84, -146.66) * mm});
            skLineSegment(sketch, "E1435", {"start": v(66.84, -146.66) * mm, "end": v(67.53, -148.23) * mm});
            skLineSegment(sketch, "E1436", {"start": v(67.53, -148.23) * mm, "end": v(67.7, -148.92) * mm});
            skLineSegment(sketch, "E1437", {"start": v(67.7, -148.92) * mm, "end": v(67.18, -149.1) * mm});
            skLineSegment(sketch, "E1438", {"start": v(67.18, -149.1) * mm, "end": v(66.49, -149.27) * mm});
            skLineSegment(sketch, "E1439", {"start": v(66.49, -149.27) * mm, "end": v(66.14, -149.27) * mm});
            skLineSegment(sketch, "E1440", {"start": v(66.14, -149.27) * mm, "end": v(66.14, -149.45) * mm});
            skLineSegment(sketch, "E1441", {"start": v(66.14, -149.45) * mm, "end": v(65.97, -149.45) * mm});
            skLineSegment(sketch, "E1442", {"start": v(65.97, -149.45) * mm, "end": v(65.44, -149.45) * mm});
            skLineSegment(sketch, "E1443", {"start": v(65.44, -149.45) * mm, "end": v(65.27, -149.45) * mm});
            skLineSegment(sketch, "E1444", {"start": v(65.27, -149.45) * mm, "end": v(64.75, -149.45) * mm});
            skLineSegment(sketch, "E1445", {"start": v(64.75, -149.45) * mm, "end": v(64.58, -149.45) * mm});
            skLineSegment(sketch, "E1446", {"start": v(64.58, -149.45) * mm, "end": v(64.05, -149.62) * mm});
            skLineSegment(sketch, "E1447", {"start": v(64.05, -149.62) * mm, "end": v(63.88, -149.62) * mm});
            skLineSegment(sketch, "E1448", {"start": v(63.88, -149.62) * mm, "end": v(63.53, -149.62) * mm});
            skLineSegment(sketch, "E1449", {"start": v(63.53, -149.62) * mm, "end": v(63.36, -149.62) * mm});
            skLineSegment(sketch, "E1450", {"start": v(63.36, -149.62) * mm, "end": v(63.18, -149.62) * mm});
            skLineSegment(sketch, "E1451", {"start": v(63.18, -149.62) * mm, "end": v(62.32, -149.62) * mm});
            skLineSegment(sketch, "E1452", {"start": v(62.32, -149.62) * mm, "end": v(61.8, -149.62) * mm});
            skLineSegment(sketch, "E1453", {"start": v(61.8, -149.62) * mm, "end": v(60.75, -149.62) * mm});
            skLineSegment(sketch, "E1454", {"start": v(60.75, -149.62) * mm, "end": v(59.7, -149.8) * mm});
            skLineSegment(sketch, "E1455", {"start": v(59.7, -149.8) * mm, "end": v(58.66, -149.8) * mm});
            skLineSegment(sketch, "E1456", {"start": v(58.66, -149.8) * mm, "end": v(58.14, -149.8) * mm});
            skLineSegment(sketch, "E1457", {"start": v(58.14, -149.8) * mm, "end": v(57.62, -149.8) * mm});
            skLineSegment(sketch, "E1458", {"start": v(57.62, -149.8) * mm, "end": v(57.27, -149.8) * mm});
            skLineSegment(sketch, "E1459", {"start": v(57.27, -149.8) * mm, "end": v(57.1, -149.8) * mm});
            skLineSegment(sketch, "E1460", {"start": v(57.1, -149.8) * mm, "end": v(56.58, -149.97) * mm});
            skLineSegment(sketch, "E1461", {"start": v(56.58, -149.97) * mm, "end": v(56.06, -149.97) * mm});
            skLineSegment(sketch, "E1462", {"start": v(56.06, -149.97) * mm, "end": v(55.88, -149.97) * mm});
            skLineSegment(sketch, "E1463", {"start": v(55.88, -149.97) * mm, "end": v(55.71, -149.97) * mm});
            skLineSegment(sketch, "E1464", {"start": v(55.71, -149.97) * mm, "end": v(55.36, -149.97) * mm});
            skLineSegment(sketch, "E1465", {"start": v(55.36, -149.97) * mm, "end": v(55.19, -149.97) * mm});
            skLineSegment(sketch, "E1466", {"start": v(55.19, -149.97) * mm, "end": v(54.15, -149.97) * mm});
            skLineSegment(sketch, "E1467", {"start": v(54.15, -149.97) * mm, "end": v(53.1, -150.14) * mm});
            skLineSegment(sketch, "E1468", {"start": v(53.1, -150.14) * mm, "end": v(52.4, -150.14) * mm});
            skLineSegment(sketch, "E1469", {"start": v(52.4, -150.14) * mm, "end": v(51.89, -150.14) * mm});
            skLineSegment(sketch, "E1470", {"start": v(51.89, -150.14) * mm, "end": v(51.54, -150.14) * mm});
            skLineSegment(sketch, "E1471", {"start": v(51.54, -150.14) * mm, "end": v(51.2, -150.14) * mm});
            skLineSegment(sketch, "E1472", {"start": v(51.2, -150.14) * mm, "end": v(51.02, -150.14) * mm});
            skLineSegment(sketch, "E1473", {"start": v(51.02, -150.14) * mm, "end": v(49.8, -150.31) * mm});
            skLineSegment(sketch, "E1474", {"start": v(49.8, -150.31) * mm, "end": v(48.76, -150.31) * mm});
            skLineSegment(sketch, "E1475", {"start": v(48.76, -150.31) * mm, "end": v(47.71, -150.31) * mm});
            skLineSegment(sketch, "E1476", {"start": v(47.71, -150.31) * mm, "end": v(46.15, -150.49) * mm});
            skLineSegment(sketch, "E1477", {"start": v(46.15, -150.49) * mm, "end": v(43.9, -150.49) * mm});
            skLineSegment(sketch, "E1478", {"start": v(43.9, -150.49) * mm, "end": v(43.37, -150.49) * mm});
            skLineSegment(sketch, "E1479", {"start": v(43.37, -150.49) * mm, "end": v(42.15, -150.66) * mm});
            skLineSegment(sketch, "E1480", {"start": v(42.15, -150.66) * mm, "end": v(41.1, -150.66) * mm});
            skLineSegment(sketch, "E1481", {"start": v(41.1, -150.66) * mm, "end": v(37.98, -150.84) * mm});
            skLineSegment(sketch, "E1482", {"start": v(37.98, -150.84) * mm, "end": v(35.55, -150.84) * mm});
            skLineSegment(sketch, "E1483", {"start": v(35.55, -150.84) * mm, "end": v(35.03, -150.84) * mm});
            skLineSegment(sketch, "E1484", {"start": v(35.03, -150.84) * mm, "end": v(30.33, -151.18) * mm});
            skLineSegment(sketch, "E1485", {"start": v(30.33, -151.18) * mm, "end": v(29.12, -151.18) * mm});
            skLineSegment(sketch, "E1486", {"start": v(29.12, -151.18) * mm, "end": v(28.94, -151.18) * mm});
            skLineSegment(sketch, "E1487", {"start": v(28.94, -151.18) * mm, "end": v(27.55, -151.18) * mm});
            skLineSegment(sketch, "E1488", {"start": v(27.55, -151.18) * mm, "end": v(24.25, -151.36) * mm});
            skLineSegment(sketch, "E1489", {"start": v(24.25, -151.36) * mm, "end": v(23.73, -151.36) * mm});
            skLineSegment(sketch, "E1490", {"start": v(23.73, -151.36) * mm, "end": v(23.2, -151.36) * mm});
            skLineSegment(sketch, "E1491", {"start": v(23.2, -151.36) * mm, "end": v(22.68, -151.36) * mm});
            skLineSegment(sketch, "E1492", {"start": v(22.68, -151.36) * mm, "end": v(20.25, -151.53) * mm});
            skLineSegment(sketch, "E1493", {"start": v(20.25, -151.53) * mm, "end": v(15.38, -151.7) * mm});
            skLineSegment(sketch, "E1494", {"start": v(15.38, -151.7) * mm, "end": v(13.47, -151.7) * mm});
            skLineSegment(sketch, "E1495", {"start": v(13.47, -151.7) * mm, "end": v(13.3, -151.7) * mm});
            skLineSegment(sketch, "E1496", {"start": v(13.3, -151.7) * mm, "end": v(11.04, -151.88) * mm});
            skLineSegment(sketch, "E1497", {"start": v(11.04, -151.88) * mm, "end": v(10, -151.88) * mm});
            skLineSegment(sketch, "E1498", {"start": v(10, -151.88) * mm, "end": v(8.95, -151.88) * mm});
            skLineSegment(sketch, "E1499", {"start": v(8.95, -151.88) * mm, "end": v(6.87, -151.88) * mm});
            skLineSegment(sketch, "E1500", {"start": v(6.87, -151.88) * mm, "end": v(6, -151.88) * mm});
            skLineSegment(sketch, "E1501", {"start": v(6, -151.88) * mm, "end": v(3.56, -152.05) * mm});
            skLineSegment(sketch, "E1502", {"start": v(3.56, -152.05) * mm, "end": v(-1.83, -152.23) * mm});
            skLineSegment(sketch, "E1503", {"start": v(-1.83, -152.23) * mm, "end": v(-2.87, -152.23) * mm});
            skLineSegment(sketch, "E1504", {"start": v(-2.87, -152.23) * mm, "end": v(-4.08, -152.23) * mm});
            skLineSegment(sketch, "E1505", {"start": v(-4.08, -152.23) * mm, "end": v(-6.17, -152.23) * mm});
            skLineSegment(sketch, "E1506", {"start": v(-6.17, -152.23) * mm, "end": v(-6.34, -152.23) * mm});
            skLineSegment(sketch, "E1507", {"start": v(-6.34, -152.23) * mm, "end": v(-9.47, -152.4) * mm});
            skLineSegment(sketch, "E1508", {"start": v(-9.47, -152.4) * mm, "end": v(-9.47, -151.88) * mm});
            skLineSegment(sketch, "E1509", {"start": v(-9.47, -151.88) * mm, "end": v(-9.47, -151.53) * mm});
            skLineSegment(sketch, "E1510", {"start": v(-9.47, -151.53) * mm, "end": v(-9.47, -150.66) * mm});
            skLineSegment(sketch, "E1511", {"start": v(-9.47, -150.66) * mm, "end": v(-9.47, -149.62) * mm});
            skLineSegment(sketch, "E1512", {"start": v(-9.47, -149.62) * mm, "end": v(-9.47, -149.27) * mm});
            skLineSegment(sketch, "E1513", {"start": v(-9.47, -149.27) * mm, "end": v(-9.47, -148.92) * mm});
            skLineSegment(sketch, "E1514", {"start": v(-9.47, -148.92) * mm, "end": v(-9.47, -147.7) * mm});
            skLineSegment(sketch, "E1515", {"start": v(-9.47, -147.7) * mm, "end": v(-10.17, -147.7) * mm});
            skLineSegment(sketch, "E1516", {"start": v(-10.17, -147.7) * mm, "end": v(-10.52, -147.7) * mm});
            skLineSegment(sketch, "E1517", {"start": v(-10.52, -147.7) * mm, "end": v(-12.43, -147.7) * mm});
            skLineSegment(sketch, "E1518", {"start": v(-12.43, -147.7) * mm, "end": v(-16.43, -147.7) * mm});
            skLineSegment(sketch, "E1519", {"start": v(-16.43, -147.7) * mm, "end": v(-16.95, -147.7) * mm});
            skLineSegment(sketch, "E1520", {"start": v(-16.95, -147.7) * mm, "end": v(-18, -147.7) * mm});
            skLineSegment(sketch, "E1521", {"start": v(-18, -147.7) * mm, "end": v(-18.16, -147.7) * mm});
            skLineSegment(sketch, "E1522", {"start": v(-18.16, -147.7) * mm, "end": v(-18.69, -147.7) * mm});
            skLineSegment(sketch, "E1523", {"start": v(-18.69, -147.7) * mm, "end": v(-19.73, -147.7) * mm});
            skLineSegment(sketch, "E1524", {"start": v(-19.73, -147.7) * mm, "end": v(-21.3, -147.53) * mm});
            skLineSegment(sketch, "E1525", {"start": v(-21.3, -147.53) * mm, "end": v(-22.34, -147.53) * mm});
            skLineSegment(sketch, "E1526", {"start": v(-22.34, -147.53) * mm, "end": v(-22.51, -147.53) * mm});
            skLineSegment(sketch, "E1527", {"start": v(-22.51, -147.53) * mm, "end": v(-23.03, -147.53) * mm});
            skLineSegment(sketch, "E1528", {"start": v(-23.03, -147.53) * mm, "end": v(-23.55, -147.53) * mm});
            skLineSegment(sketch, "E1529", {"start": v(-23.55, -147.53) * mm, "end": v(-24.94, -147.53) * mm});
            skLineSegment(sketch, "E1530", {"start": v(-24.94, -147.53) * mm, "end": v(-26.86, -147.53) * mm});
            skLineSegment(sketch, "E1531", {"start": v(-26.86, -147.53) * mm, "end": v(-27.03, -147.53) * mm});
            skLineSegment(sketch, "E1532", {"start": v(-27.03, -147.53) * mm, "end": v(-29.81, -147.53) * mm});
            skLineSegment(sketch, "E1533", {"start": v(-29.81, -147.53) * mm, "end": v(-29.98, -147.53) * mm});
            skLineSegment(sketch, "E1534", {"start": v(-29.98, -147.53) * mm, "end": v(-31.2, -147.53) * mm});
            skLineSegment(sketch, "E1535", {"start": v(-31.2, -147.53) * mm, "end": v(-33.29, -147.53) * mm});
            skLineSegment(sketch, "E1536", {"start": v(-33.29, -147.53) * mm, "end": v(-35.37, -147.36) * mm});
            skLineSegment(sketch, "E1537", {"start": v(-35.37, -147.36) * mm, "end": v(-35.55, -147.53) * mm});
            skLineSegment(sketch, "E1538", {"start": v(-35.55, -147.53) * mm, "end": v(-36.6, -147.36) * mm});
            skLineSegment(sketch, "E1539", {"start": v(-36.6, -147.36) * mm, "end": v(-36.94, -147.36) * mm});
            skLineSegment(sketch, "E1540", {"start": v(-36.94, -147.36) * mm, "end": v(-37.46, -147.36) * mm});
            skLineSegment(sketch, "E1541", {"start": v(-37.46, -147.36) * mm, "end": v(-37.98, -147.36) * mm});
            skLineSegment(sketch, "E1542", {"start": v(-37.98, -147.36) * mm, "end": v(-38.68, -147.36) * mm});
            skLineSegment(sketch, "E1543", {"start": v(-38.68, -147.36) * mm, "end": v(-39.72, -147.36) * mm});
            skLineSegment(sketch, "E1544", {"start": v(-39.72, -147.36) * mm, "end": v(-40.07, -147.36) * mm});
            skLineSegment(sketch, "E1545", {"start": v(-40.07, -147.36) * mm, "end": v(-40.41, -147.36) * mm});
            skLineSegment(sketch, "E1546", {"start": v(-40.41, -147.36) * mm, "end": v(-40.76, -147.36) * mm});
            skLineSegment(sketch, "E1547", {"start": v(-40.76, -147.36) * mm, "end": v(-41.46, -147.36) * mm});
            skLineSegment(sketch, "E1548", {"start": v(-41.46, -147.36) * mm, "end": v(-43.02, -147.36) * mm});
            skLineSegment(sketch, "E1549", {"start": v(-43.02, -147.36) * mm, "end": v(-44.06, -147.36) * mm});
            skLineSegment(sketch, "E1550", {"start": v(-44.06, -147.36) * mm, "end": v(-44.41, -147.36) * mm});
            skLineSegment(sketch, "E1551", {"start": v(-44.41, -147.36) * mm, "end": v(-47.37, -147.36) * mm});
            skLineSegment(sketch, "E1552", {"start": v(-47.37, -147.36) * mm, "end": v(-48.93, -147.36) * mm});
            skLineSegment(sketch, "E1553", {"start": v(-48.93, -147.36) * mm, "end": v(-49.1, -147.36) * mm});
            skLineSegment(sketch, "E1554", {"start": v(-49.1, -147.36) * mm, "end": v(-49.63, -147.36) * mm});
            skLineSegment(sketch, "E1555", {"start": v(-49.63, -147.36) * mm, "end": v(-54.15, -147.18) * mm});
            skLineSegment(sketch, "E1556", {"start": v(-54.15, -147.18) * mm, "end": v(-55.02, -147.18) * mm});
            skLineSegment(sketch, "E1557", {"start": v(-55.02, -147.18) * mm, "end": v(-55.54, -147.18) * mm});
            skLineSegment(sketch, "E1558", {"start": v(-55.54, -147.18) * mm, "end": v(-56.4, -147.18) * mm});
            skLineSegment(sketch, "E1559", {"start": v(-56.4, -147.18) * mm, "end": v(-56.58, -147.18) * mm});
            skLineSegment(sketch, "E1560", {"start": v(-56.58, -147.18) * mm, "end": v(-57.1, -147.18) * mm});
            skLineSegment(sketch, "E1561", {"start": v(-57.1, -147.18) * mm, "end": v(-57.28, -147.18) * mm});
            skLineSegment(sketch, "E1562", {"start": v(-57.28, -147.18) * mm, "end": v(-60.58, -147.18) * mm});
            skLineSegment(sketch, "E1563", {"start": v(-60.58, -147.18) * mm, "end": v(-60.93, -147.18) * mm});
            skLineSegment(sketch, "E1564", {"start": v(-60.93, -147.18) * mm, "end": v(-62.14, -147.18) * mm});
            skLineSegment(sketch, "E1565", {"start": v(-62.14, -147.18) * mm, "end": v(-63.36, -147.18) * mm});
            skLineSegment(sketch, "E1566", {"start": v(-63.36, -147.18) * mm, "end": v(-63.53, -147.18) * mm});
            skLineSegment(sketch, "E1567", {"start": v(-63.53, -147.18) * mm, "end": v(-64.4, -147.01) * mm});
            skLineSegment(sketch, "E1568", {"start": v(-64.4, -147.01) * mm, "end": v(-65.45, -147.01) * mm});
            skLineSegment(sketch, "E1569", {"start": v(-65.45, -147.01) * mm, "end": v(-67.01, -147.01) * mm});
            skLineSegment(sketch, "E1570", {"start": v(-67.01, -147.01) * mm, "end": v(-67.53, -147.01) * mm});
            skLineSegment(sketch, "E1571", {"start": v(-67.53, -147.01) * mm, "end": v(-68.92, -147.01) * mm});
            skLineSegment(sketch, "E1572", {"start": v(-68.92, -147.01) * mm, "end": v(-69.1, -147.01) * mm});
            skLineSegment(sketch, "E1573", {"start": v(-69.1, -147.01) * mm, "end": v(-69.27, -147.01) * mm});
            skLineSegment(sketch, "E1574", {"start": v(-69.27, -147.01) * mm, "end": v(-69.8, -147.01) * mm});
            skLineSegment(sketch, "E1575", {"start": v(-69.8, -147.01) * mm, "end": v(-70.31, -147.01) * mm});
            skLineSegment(sketch, "E1576", {"start": v(-70.31, -147.01) * mm, "end": v(-72.75, -146.84) * mm});
            skLineSegment(sketch, "E1577", {"start": v(-72.75, -146.84) * mm, "end": v(-74.66, -146.84) * mm});
            skLineSegment(sketch, "E1578", {"start": v(-74.66, -146.84) * mm, "end": v(-75.53, -146.84) * mm});
            skLineSegment(sketch, "E1579", {"start": v(-75.53, -146.84) * mm, "end": v(-75.7, -146.84) * mm});
            skLineSegment(sketch, "E1580", {"start": v(-75.7, -146.84) * mm, "end": v(-75.87, -146.84) * mm});
            skLineSegment(sketch, "E1581", {"start": v(-75.87, -146.84) * mm, "end": v(-76.05, -146.84) * mm});
            skLineSegment(sketch, "E1582", {"start": v(-76.05, -146.84) * mm, "end": v(-76.22, -146.84) * mm});
            skLineSegment(sketch, "E1583", {"start": v(-76.22, -146.84) * mm, "end": v(-78.3, -146.66) * mm});
            skLineSegment(sketch, "E1584", {"start": v(-78.3, -146.66) * mm, "end": v(-79.53, -146.66) * mm});
            skLineSegment(sketch, "E1585", {"start": v(-79.53, -146.66) * mm, "end": v(-82.13, -146.66) * mm});
            skLineSegment(sketch, "E1586", {"start": v(-82.13, -146.66) * mm, "end": v(-83, -146.66) * mm});
            skLineSegment(sketch, "E1587", {"start": v(-83, -146.66) * mm, "end": v(-83.18, -146.66) * mm});
            skLineSegment(sketch, "E1588", {"start": v(-83.18, -146.66) * mm, "end": v(-85.96, -146.49) * mm});
            skLineSegment(sketch, "E1589", {"start": v(-85.96, -146.49) * mm, "end": v(-86.48, -146.49) * mm});
            skLineSegment(sketch, "E1590", {"start": v(-86.48, -146.49) * mm, "end": v(-88.22, -146.49) * mm});
            skLineSegment(sketch, "E1591", {"start": v(-88.22, -146.49) * mm, "end": v(-88.56, -146.49) * mm});
            skLineSegment(sketch, "E1592", {"start": v(-88.56, -146.49) * mm, "end": v(-88.91, -146.49) * mm});
            skLineSegment(sketch, "E1593", {"start": v(-88.91, -146.49) * mm, "end": v(-89.08, -146.49) * mm});
            skLineSegment(sketch, "E1594", {"start": v(-89.08, -146.49) * mm, "end": v(-89.43, -146.49) * mm});
            skLineSegment(sketch, "E1595", {"start": v(-89.43, -146.49) * mm, "end": v(-89.6, -146.49) * mm});
            skLineSegment(sketch, "E1596", {"start": v(-89.6, -146.49) * mm, "end": v(-89.95, -146.49) * mm});
            skLineSegment(sketch, "E1597", {"start": v(-89.95, -146.49) * mm, "end": v(-90.3, -146.49) * mm});
            skLineSegment(sketch, "E1598", {"start": v(-90.3, -146.49) * mm, "end": v(-90.82, -146.49) * mm});
            skLineSegment(sketch, "E1599", {"start": v(-90.82, -146.49) * mm, "end": v(-91.17, -146.49) * mm});
            skLineSegment(sketch, "E1600", {"start": v(-91.17, -146.49) * mm, "end": v(-92.9, -146.49) * mm});
            skLineSegment(sketch, "E1601", {"start": v(-92.9, -146.49) * mm, "end": v(-93.26, -146.49) * mm});
            skLineSegment(sketch, "E1602", {"start": v(-93.26, -146.49) * mm, "end": v(-93.6, -146.49) * mm});
            skLineSegment(sketch, "E1603", {"start": v(-93.6, -146.49) * mm, "end": v(-95, -146.31) * mm});
            skLineSegment(sketch, "E1604", {"start": v(-95, -146.31) * mm, "end": v(-95.52, -146.31) * mm});
            skLineSegment(sketch, "E1605", {"start": v(-95.52, -146.31) * mm, "end": v(-96.04, -146.31) * mm});
            skLineSegment(sketch, "E1606", {"start": v(-96.04, -146.31) * mm, "end": v(-99.17, -146.31) * mm});
            skLineSegment(sketch, "E1607", {"start": v(-99.17, -146.31) * mm, "end": v(-99.69, -146.31) * mm});
            skLineSegment(sketch, "E1608", {"start": v(-99.69, -146.31) * mm, "end": v(-101.43, -146.31) * mm});
            skLineSegment(sketch, "E1609", {"start": v(-101.43, -146.31) * mm, "end": v(-104.03, -146.14) * mm});
            skLineSegment(sketch, "E1610", {"start": v(-104.03, -146.14) * mm, "end": v(-104.9, -146.14) * mm});
            skLineSegment(sketch, "E1611", {"start": v(-104.9, -146.14) * mm, "end": v(-105.25, -146.14) * mm});
            skLineSegment(sketch, "E1612", {"start": v(-105.25, -146.14) * mm, "end": v(-106.81, -146.14) * mm});
            skLineSegment(sketch, "E1613", {"start": v(-106.81, -146.14) * mm, "end": v(-106.99, -146.14) * mm});
            skLineSegment(sketch, "E1614", {"start": v(-106.99, -146.14) * mm, "end": v(-107.86, -146.14) * mm});
            skLineSegment(sketch, "E1615", {"start": v(-107.86, -146.14) * mm, "end": v(-108.55, -146.14) * mm});
            skLineSegment(sketch, "E1616", {"start": v(-108.55, -146.14) * mm, "end": v(-110.64, -145.97) * mm});
            skLineSegment(sketch, "E1617", {"start": v(-110.64, -145.97) * mm, "end": v(-111.68, -145.97) * mm});
            skLineSegment(sketch, "E1618", {"start": v(-111.68, -145.97) * mm, "end": v(-113.25, -145.97) * mm});
            skLineSegment(sketch, "E1619", {"start": v(-113.25, -145.97) * mm, "end": v(-114.98, -145.8) * mm});
            skLineSegment(sketch, "E1620", {"start": v(-114.98, -145.8) * mm, "end": v(-116.2, -145.8) * mm});
            skLineSegment(sketch, "E1621", {"start": v(-116.2, -145.8) * mm, "end": v(-117.6, -145.8) * mm});
            skLineSegment(sketch, "E1622", {"start": v(-117.6, -145.8) * mm, "end": v(-117.77, -145.8) * mm});
            skLineSegment(sketch, "E1623", {"start": v(-117.77, -145.8) * mm, "end": v(-117.94, -145.8) * mm});
            skLineSegment(sketch, "E1624", {"start": v(-117.94, -145.8) * mm, "end": v(-119.5, -145.62) * mm});
            skLineSegment(sketch, "E1625", {"start": v(-119.5, -145.62) * mm, "end": v(-120.72, -145.62) * mm});
            skLineSegment(sketch, "E1626", {"start": v(-120.72, -145.62) * mm, "end": v(-120.9, -145.62) * mm});
            skLineSegment(sketch, "E1627", {"start": v(-120.9, -145.62) * mm, "end": v(-121.24, -145.62) * mm});
            skLineSegment(sketch, "E1628", {"start": v(-121.24, -145.62) * mm, "end": v(-121.6, -145.62) * mm});
            skLineSegment(sketch, "E1629", {"start": v(-121.6, -145.62) * mm, "end": v(-121.94, -145.62) * mm});
            skLineSegment(sketch, "E1630", {"start": v(-121.94, -145.62) * mm, "end": v(-120.9, -144.92) * mm});
            skLineSegment(sketch, "E1631", {"start": v(-120.9, -144.92) * mm, "end": v(-120.72, -144.92) * mm});
            skLineSegment(sketch, "E1632", {"start": v(-120.72, -144.92) * mm, "end": v(-120.72, -144.75) * mm});
            skLineSegment(sketch, "E1633", {"start": v(-120.72, -144.75) * mm, "end": v(-119.33, -143.88) * mm});
            skLineSegment(sketch, "E1634", {"start": v(-119.33, -143.88) * mm, "end": v(-118.64, -143.36) * mm});
            skLineSegment(sketch, "E1635", {"start": v(-118.64, -143.36) * mm, "end": v(-117.77, -142.66) * mm});
            skLineSegment(sketch, "E1636", {"start": v(-117.77, -142.66) * mm, "end": v(-117.24, -142.49) * mm});
            skLineSegment(sketch, "E1637", {"start": v(-117.24, -142.49) * mm, "end": v(-116.9, -142.14) * mm});
            skLineSegment(sketch, "E1638", {"start": v(-116.9, -142.14) * mm, "end": v(-116.03, -141.45) * mm});
            skLineSegment(sketch, "E1639", {"start": v(-116.03, -141.45) * mm, "end": v(-115.85, -141.45) * mm});
            skLineSegment(sketch, "E1640", {"start": v(-115.85, -141.45) * mm, "end": v(-115.16, -140.75) * mm});
            skLineSegment(sketch, "E1641", {"start": v(-115.16, -140.75) * mm, "end": v(-114.64, -140.4) * mm});
            skLineSegment(sketch, "E1642", {"start": v(-114.64, -140.4) * mm, "end": v(-113.77, -139.53) * mm});
            skLineSegment(sketch, "E1643", {"start": v(-113.77, -139.53) * mm, "end": v(-112.2, -137.97) * mm});
            skLineSegment(sketch, "E1644", {"start": v(-112.2, -137.97) * mm, "end": v(-111.86, -137.62) * mm});
            skLineSegment(sketch, "E1645", {"start": v(-111.86, -137.62) * mm, "end": v(-111.68, -137.45) * mm});
            skLineSegment(sketch, "E1646", {"start": v(-111.68, -137.45) * mm, "end": v(-110.47, -136.06) * mm});
            skLineSegment(sketch, "E1647", {"start": v(-110.47, -136.06) * mm, "end": v(-110.3, -136.06) * mm});
            skLineSegment(sketch, "E1648", {"start": v(-110.3, -136.06) * mm, "end": v(-110.12, -135.7) * mm});
            skLineSegment(sketch, "E1649", {"start": v(-110.12, -135.7) * mm, "end": v(-109.94, -135.53) * mm});
            skLineSegment(sketch, "E1650", {"start": v(-109.94, -135.53) * mm, "end": v(-109.07, -134.14) * mm});
            skLineSegment(sketch, "E1651", {"start": v(-109.07, -134.14) * mm, "end": v(-108.55, -133.45) * mm});
            skLineSegment(sketch, "E1652", {"start": v(-108.55, -133.45) * mm, "end": v(-108.03, -132.4) * mm});
            skLineSegment(sketch, "E1653", {"start": v(-108.03, -132.4) * mm, "end": v(-107.86, -131.88) * mm});
            skLineSegment(sketch, "E1654", {"start": v(-107.86, -131.88) * mm, "end": v(-107.16, -129.8) * mm});
            skLineSegment(sketch, "E1655", {"start": v(-107.16, -129.8) * mm, "end": v(-106.99, -129.28) * mm});
            skLineSegment(sketch, "E1656", {"start": v(-106.99, -129.28) * mm, "end": v(-106.47, -128.23) * mm});
            skLineSegment(sketch, "E1657", {"start": v(-106.47, -128.23) * mm, "end": v(-105.95, -127.02) * mm});
            skLineSegment(sketch, "E1658", {"start": v(-105.95, -127.02) * mm, "end": v(-105.25, -125.62) * mm});
            skLineSegment(sketch, "E1659", {"start": v(-105.25, -125.62) * mm, "end": v(-104.56, -124.4) * mm});
            skLineSegment(sketch, "E1660", {"start": v(-104.56, -124.4) * mm, "end": v(-103.86, -123.19) * mm});
            skLineSegment(sketch, "E1661", {"start": v(-103.86, -123.19) * mm, "end": v(-103.86, -122.84) * mm});
            skLineSegment(sketch, "E1662", {"start": v(-103.86, -122.84) * mm, "end": v(-103.34, -121.97) * mm});
            skLineSegment(sketch, "E1663", {"start": v(-103.34, -121.97) * mm, "end": v(-102.64, -120.4) * mm});
            skLineSegment(sketch, "E1664", {"start": v(-102.64, -120.4) * mm, "end": v(-102.47, -119.89) * mm});
            skLineSegment(sketch, "E1665", {"start": v(-102.47, -119.89) * mm, "end": v(-102.3, -119.54) * mm});
            skLineSegment(sketch, "E1666", {"start": v(-102.3, -119.54) * mm, "end": v(-101.95, -119.02) * mm});
            skLineSegment(sketch, "E1667", {"start": v(-101.95, -119.02) * mm, "end": v(-101.6, -118.5) * mm});
            skLineSegment(sketch, "E1668", {"start": v(-101.6, -118.5) * mm, "end": v(-101.25, -118.32) * mm});
            skLineSegment(sketch, "E1669", {"start": v(-101.25, -118.32) * mm, "end": v(-101.08, -118.15) * mm});
            skLineSegment(sketch, "E1670", {"start": v(-101.08, -118.15) * mm, "end": v(-100.04, -116.58) * mm});
            skLineSegment(sketch, "E1671", {"start": v(-100.04, -116.58) * mm, "end": v(-98.3, -114.5) * mm});
            skLineSegment(sketch, "E1672", {"start": v(-98.3, -114.5) * mm, "end": v(-97.95, -114.15) * mm});
            skLineSegment(sketch, "E1673", {"start": v(-97.95, -114.15) * mm, "end": v(-97.78, -113.8) * mm});
            skLineSegment(sketch, "E1674", {"start": v(-97.78, -113.8) * mm, "end": v(-96.56, -112.24) * mm});
            skLineSegment(sketch, "E1675", {"start": v(-96.56, -112.24) * mm, "end": v(-96.56, -112.06) * mm});
            skLineSegment(sketch, "E1676", {"start": v(-96.56, -112.06) * mm, "end": v(-95.52, -110.32) * mm});
            skLineSegment(sketch, "E1677", {"start": v(-95.52, -110.32) * mm, "end": v(-95.17, -109.98) * mm});
            skLineSegment(sketch, "E1678", {"start": v(-95.17, -109.98) * mm, "end": v(-95, -109.63) * mm});
            skLineSegment(sketch, "E1679", {"start": v(-95, -109.63) * mm, "end": v(-95, -109.45) * mm});
            skLineSegment(sketch, "E1680", {"start": v(-95, -109.45) * mm, "end": v(-93.6, -106.67) * mm});
            skLineSegment(sketch, "E1681", {"start": v(-93.6, -106.67) * mm, "end": v(-92.9, -105.45) * mm});
            skLineSegment(sketch, "E1682", {"start": v(-92.9, -105.45) * mm, "end": v(-92.39, -103.89) * mm});
            skLineSegment(sketch, "E1683", {"start": v(-92.39, -103.89) * mm, "end": v(-91.52, -101.8) * mm});
            skLineSegment(sketch, "E1684", {"start": v(-91.52, -101.8) * mm, "end": v(-91.17, -100.76) * mm});
            skLineSegment(sketch, "E1685", {"start": v(-91.17, -100.76) * mm, "end": v(-91, -100.06) * mm});
            skLineSegment(sketch, "E1686", {"start": v(-91, -100.06) * mm, "end": v(-91, -99.9) * mm});
            skLineSegment(sketch, "E1687", {"start": v(-91, -99.9) * mm, "end": v(-90.82, -99.37) * mm});
            skLineSegment(sketch, "E1688", {"start": v(-90.82, -99.37) * mm, "end": v(-90.82, -99.2) * mm});
            skLineSegment(sketch, "E1689", {"start": v(-90.82, -99.2) * mm, "end": v(-90.82, -98.85) * mm});
            skLineSegment(sketch, "E1690", {"start": v(-90.82, -98.85) * mm, "end": v(-90.82, -98.67) * mm});
            skLineSegment(sketch, "E1691", {"start": v(-90.82, -98.67) * mm, "end": v(-90.3, -97.8) * mm});
            skLineSegment(sketch, "E1692", {"start": v(-90.3, -97.8) * mm, "end": v(-90.13, -97.28) * mm});
            skLineSegment(sketch, "E1693", {"start": v(-90.13, -97.28) * mm, "end": v(-89.78, -96.41) * mm});
            skLineSegment(sketch, "E1694", {"start": v(-89.78, -96.41) * mm, "end": v(-89.43, -95.72) * mm});
            skLineSegment(sketch, "E1695", {"start": v(-89.43, -95.72) * mm, "end": v(-89.43, -95.54) * mm});
            skLineSegment(sketch, "E1696", {"start": v(-89.43, -95.54) * mm, "end": v(-89.43, -95.37) * mm});
            skLineSegment(sketch, "E1697", {"start": v(-89.43, -95.37) * mm, "end": v(-88.91, -93.46) * mm});
            skLineSegment(sketch, "E1698", {"start": v(-88.91, -93.46) * mm, "end": v(-88.74, -92.94) * mm});
            skLineSegment(sketch, "E1699", {"start": v(-88.74, -92.94) * mm, "end": v(-88.74, -92.76) * mm});
            skLineSegment(sketch, "E1700", {"start": v(-88.74, -92.76) * mm, "end": v(-88.39, -91.02) * mm});
            skLineSegment(sketch, "E1701", {"start": v(-88.39, -91.02) * mm, "end": v(-88.39, -90.15) * mm});
            skLineSegment(sketch, "E1702", {"start": v(-88.39, -90.15) * mm, "end": v(-88.22, -89.8) * mm});
            skLineSegment(sketch, "E1703", {"start": v(-88.22, -89.8) * mm, "end": v(-88.04, -88.42) * mm});
            skLineSegment(sketch, "E1704", {"start": v(-88.04, -88.42) * mm, "end": v(-88.04, -88.24) * mm});
            skLineSegment(sketch, "E1705", {"start": v(-88.04, -88.24) * mm, "end": v(-87.7, -86.5) * mm});
            skLineSegment(sketch, "E1706", {"start": v(-87.7, -86.5) * mm, "end": v(-87.35, -85.28) * mm});
            skLineSegment(sketch, "E1707", {"start": v(-87.35, -85.28) * mm, "end": v(-87.17, -84.42) * mm});
            skLineSegment(sketch, "E1708", {"start": v(-87.17, -84.42) * mm, "end": v(-87.17, -84.07) * mm});
            skLineSegment(sketch, "E1709", {"start": v(-87.17, -84.07) * mm, "end": v(-87.17, -82.68) * mm});
            skLineSegment(sketch, "E1710", {"start": v(-87.17, -82.68) * mm, "end": v(-87.35, -81.29) * mm});
            skLineSegment(sketch, "E1711", {"start": v(-87.35, -81.29) * mm, "end": v(-87.35, -81.11) * mm});
            skLineSegment(sketch, "E1712", {"start": v(-87.35, -81.11) * mm, "end": v(-87.17, -81.11) * mm});
            skLineSegment(sketch, "E1713", {"start": v(-87.17, -81.11) * mm, "end": v(-87.17, -80.94) * mm});
            skLineSegment(sketch, "E1714", {"start": v(-87.17, -80.94) * mm, "end": v(-87.17, -80.6) * mm});
            skLineSegment(sketch, "E1715", {"start": v(-87.17, -80.6) * mm, "end": v(-87, -80.24) * mm});
            skLineSegment(sketch, "E1716", {"start": v(-87, -80.24) * mm, "end": v(-86.48, -79.2) * mm});
            skLineSegment(sketch, "E1717", {"start": v(-86.48, -79.2) * mm, "end": v(-86.48, -79.03) * mm});
            skLineSegment(sketch, "E1718", {"start": v(-86.48, -79.03) * mm, "end": v(-86.3, -78.5) * mm});
            skLineSegment(sketch, "E1719", {"start": v(-86.3, -78.5) * mm, "end": v(-86.3, -78.33) * mm});
            skLineSegment(sketch, "E1720", {"start": v(-86.3, -78.33) * mm, "end": v(-86.3, -77.98) * mm});
            skLineSegment(sketch, "E1721", {"start": v(-86.3, -77.98) * mm, "end": v(-86.13, -77.11) * mm});
            skLineSegment(sketch, "E1722", {"start": v(-86.13, -77.11) * mm, "end": v(-85.96, -75.37) * mm});
            skLineSegment(sketch, "E1723", {"start": v(-85.96, -75.37) * mm, "end": v(-85.96, -75.03) * mm});
            skLineSegment(sketch, "E1724", {"start": v(-85.96, -75.03) * mm, "end": v(-85.96, -74.16) * mm});
            skLineSegment(sketch, "E1725", {"start": v(-85.96, -74.16) * mm, "end": v(-85.96, -73.11) * mm});
            skLineSegment(sketch, "E1726", {"start": v(-85.96, -73.11) * mm, "end": v(-85.96, -72.94) * mm});
            skLineSegment(sketch, "E1727", {"start": v(-85.96, -72.94) * mm, "end": v(-85.96, -71.9) * mm});
            skLineSegment(sketch, "E1728", {"start": v(-85.96, -71.9) * mm, "end": v(-85.96, -71.55) * mm});
            skLineSegment(sketch, "E1729", {"start": v(-85.96, -71.55) * mm, "end": v(-85.96, -71.03) * mm});
            skLineSegment(sketch, "E1730", {"start": v(-85.96, -71.03) * mm, "end": v(-85.96, -70.33) * mm});
            skLineSegment(sketch, "E1731", {"start": v(-85.96, -70.33) * mm, "end": v(-85.96, -69.98) * mm});
            skLineSegment(sketch, "E1732", {"start": v(-85.96, -69.98) * mm, "end": v(-85.96, -69.64) * mm});
            skLineSegment(sketch, "E1733", {"start": v(-85.96, -69.64) * mm, "end": v(-85.96, -68.77) * mm});
            skLineSegment(sketch, "E1734", {"start": v(-85.96, -68.77) * mm, "end": v(-85.96, -68.25) * mm});
            skLineSegment(sketch, "E1735", {"start": v(-85.96, -68.25) * mm, "end": v(-85.96, -67.72) * mm});
            skLineSegment(sketch, "E1736", {"start": v(-85.96, -67.72) * mm, "end": v(-85.96, -66.68) * mm});
            skLineSegment(sketch, "E1737", {"start": v(-85.96, -66.68) * mm, "end": v(-85.96, -66.16) * mm});
            skLineSegment(sketch, "E1738", {"start": v(-85.96, -66.16) * mm, "end": v(-85.96, -64.94) * mm});
            skLineSegment(sketch, "E1739", {"start": v(-85.96, -64.94) * mm, "end": v(-85.96, -64.77) * mm});
            skLineSegment(sketch, "E1740", {"start": v(-85.96, -64.77) * mm, "end": v(-85.96, -64.6) * mm});
            skLineSegment(sketch, "E1741", {"start": v(-85.96, -64.6) * mm, "end": v(-85.96, -64.07) * mm});
            skLineSegment(sketch, "E1742", {"start": v(-85.96, -64.07) * mm, "end": v(-85.96, -63.03) * mm});
            skLineSegment(sketch, "E1743", {"start": v(-85.96, -63.03) * mm, "end": v(-85.96, -62.86) * mm});
            skLineSegment(sketch, "E1744", {"start": v(-85.96, -62.86) * mm, "end": v(-86.13, -61.81) * mm});
            skLineSegment(sketch, "E1745", {"start": v(-86.13, -61.81) * mm, "end": v(-86.13, -61.46) * mm});
            skLineSegment(sketch, "E1746", {"start": v(-86.13, -61.46) * mm, "end": v(-86.13, -60.77) * mm});
            skLineSegment(sketch, "E1747", {"start": v(-86.13, -60.77) * mm, "end": v(-86.13, -60.42) * mm});
            skLineSegment(sketch, "E1748", {"start": v(-86.13, -60.42) * mm, "end": v(-86.13, -60.25) * mm});
            skLineSegment(sketch, "E1749", {"start": v(-86.13, -60.25) * mm, "end": v(-86.13, -59.55) * mm});
            skLineSegment(sketch, "E1750", {"start": v(-86.13, -59.55) * mm, "end": v(-86.3, -58.5) * mm});
            skLineSegment(sketch, "E1751", {"start": v(-86.3, -58.5) * mm, "end": v(-86.3, -56.94) * mm});
            skLineSegment(sketch, "E1752", {"start": v(-86.3, -56.94) * mm, "end": v(-86.48, -55.38) * mm});
            skLineSegment(sketch, "E1753", {"start": v(-86.48, -55.38) * mm, "end": v(-86.48, -55.2) * mm});
            skLineSegment(sketch, "E1754", {"start": v(-86.48, -55.2) * mm, "end": v(-86.48, -55.03) * mm});
            skLineSegment(sketch, "E1755", {"start": v(-86.48, -55.03) * mm, "end": v(-86.83, -52.95) * mm});
            skLineSegment(sketch, "E1756", {"start": v(-86.83, -52.95) * mm, "end": v(-87.17, -51.73) * mm});
            skLineSegment(sketch, "E1757", {"start": v(-87.17, -51.73) * mm, "end": v(-87.35, -50.86) * mm});
            skLineSegment(sketch, "E1758", {"start": v(-87.35, -50.86) * mm, "end": v(-87.35, -50.51) * mm});
            skLineSegment(sketch, "E1759", {"start": v(-87.35, -50.51) * mm, "end": v(-87.7, -49.82) * mm});
            skLineSegment(sketch, "E1760", {"start": v(-87.7, -49.82) * mm, "end": v(-87.7, -49.12) * mm});
            skLineSegment(sketch, "E1761", {"start": v(-87.7, -49.12) * mm, "end": v(-87.87, -48.77) * mm});
            skLineSegment(sketch, "E1762", {"start": v(-87.87, -48.77) * mm, "end": v(-87.87, -47.9) * mm});
            skLineSegment(sketch, "E1763", {"start": v(-87.87, -47.9) * mm, "end": v(-88.04, -47.73) * mm});
            skLineSegment(sketch, "E1764", {"start": v(-88.04, -47.73) * mm, "end": v(-88.04, -47.56) * mm});
            skLineSegment(sketch, "E1765", {"start": v(-88.04, -47.56) * mm, "end": v(-88.56, -45.99) * mm});
            skLineSegment(sketch, "E1766", {"start": v(-88.56, -45.99) * mm, "end": v(-88.74, -45.3) * mm});
            skLineSegment(sketch, "E1767", {"start": v(-88.74, -45.3) * mm, "end": v(-89.26, -43.9) * mm});
            skLineSegment(sketch, "E1768", {"start": v(-89.26, -43.9) * mm, "end": v(-89.78, -42.51) * mm});
            skLineSegment(sketch, "E1769", {"start": v(-89.78, -42.51) * mm, "end": v(-90.13, -41.82) * mm});
            skLineSegment(sketch, "E1770", {"start": v(-90.13, -41.82) * mm, "end": v(-91, -39.56) * mm});
            skLineSegment(sketch, "E1771", {"start": v(-91, -39.56) * mm, "end": v(-91.34, -39.03) * mm});
            skLineSegment(sketch, "E1772", {"start": v(-91.34, -39.03) * mm, "end": v(-92.39, -36.6) * mm});
            skLineSegment(sketch, "E1773", {"start": v(-92.39, -36.6) * mm, "end": v(-93.6, -33.82) * mm});
            skLineSegment(sketch, "E1774", {"start": v(-93.6, -33.82) * mm, "end": v(-94.47, -31.9) * mm});
            skLineSegment(sketch, "E1775", {"start": v(-94.47, -31.9) * mm, "end": v(-95.17, -30.34) * mm});
            skLineSegment(sketch, "E1776", {"start": v(-95.17, -30.34) * mm, "end": v(-95.86, -28.78) * mm});
            skLineSegment(sketch, "E1777", {"start": v(-95.86, -28.78) * mm, "end": v(-95.86, -28.43) * mm});
            skLineSegment(sketch, "E1778", {"start": v(-95.86, -28.43) * mm, "end": v(-96.04, -28.25) * mm});
            skLineSegment(sketch, "E1779", {"start": v(-96.04, -28.25) * mm, "end": v(-96.73, -26) * mm});
            skLineSegment(sketch, "E1780", {"start": v(-96.73, -26) * mm, "end": v(-96.73, -25.65) * mm});
            skLineSegment(sketch, "E1781", {"start": v(-96.73, -25.65) * mm, "end": v(-97.08, -24.43) * mm});
            skLineSegment(sketch, "E1782", {"start": v(-97.08, -24.43) * mm, "end": v(-97.25, -24.26) * mm});
            skLineSegment(sketch, "E1783", {"start": v(-97.25, -24.26) * mm, "end": v(-97.43, -23.39) * mm});
            skLineSegment(sketch, "E1784", {"start": v(-97.43, -23.39) * mm, "end": v(-97.6, -22.86) * mm});
            skLineSegment(sketch, "E1785", {"start": v(-97.6, -22.86) * mm, "end": v(-97.6, -22.52) * mm});
            skLineSegment(sketch, "E1786", {"start": v(-97.6, -22.52) * mm, "end": v(-97.78, -21.82) * mm});
            skLineSegment(sketch, "E1787", {"start": v(-97.78, -21.82) * mm, "end": v(-97.78, -21.65) * mm});
            skLineSegment(sketch, "E1788", {"start": v(-97.78, -21.65) * mm, "end": v(-98.12, -20.43) * mm});
            skLineSegment(sketch, "E1789", {"start": v(-98.12, -20.43) * mm, "end": v(-98.3, -19.56) * mm});
            skLineSegment(sketch, "E1790", {"start": v(-98.3, -19.56) * mm, "end": v(-98.47, -18.7) * mm});
            skSolve(sketch);
        }
        {
            var Q0;
            Q0=makeQuery(id+"F0.imprint","IMPRINT",FACE,{"disambiguationData":[TD([[makeQuery(id+"F0.imprint","IMPRINT",EDGE,{"derivedFrom":sQuery(id+"F0.wireOp",EDGE,"E0")}),-1.0]])]});
            extrude(context, id + "F1", {"entities" : qUnion([Q0]), "depth" : 25.4 * mm});
        }
        {
            var Q0;
            Q0=makeQuery(id+"F1.opExtrude","CAP_FACE",FACE,{"disambiguationData":[OSD([sQuery(id+"F0.wireOp",EDGE,"E0"),sQuery(id+"F0.wireOp",EDGE,"E1"),sQuery(id+"F0.wireOp",EDGE,"E2"),sQuery(id+"F0.wireOp",EDGE,"E3"),sQuery(id+"F0.wireOp",EDGE,"E4"),sQuery(id+"F0.wireOp",EDGE,"E5"),sQuery(id+"F0.wireOp",EDGE,"E6"),sQuery(id+"F0.wireOp",EDGE,"E7"),sQuery(id+"F0.wireOp",EDGE,"E8"),sQuery(id+"F0.wireOp",EDGE,"E9"),sQuery(id+"F0.wireOp",EDGE,"E10"),sQuery(id+"F0.wireOp",EDGE,"E11"),sQuery(id+"F0.wireOp",EDGE,"E12"),sQuery(id+"F0.wireOp",EDGE,"E13"),sQuery(id+"F0.wireOp",EDGE,"E14"),sQuery(id+"F0.wireOp",EDGE,"E15"),sQuery(id+"F0.wireOp",EDGE,"E16"),sQuery(id+"F0.wireOp",EDGE,"E17"),sQuery(id+"F0.wireOp",EDGE,"E18"),sQuery(id+"F0.wireOp",EDGE,"E19"),sQuery(id+"F0.wireOp",EDGE,"E20"),sQuery(id+"F0.wireOp",EDGE,"E21"),sQuery(id+"F0.wireOp",EDGE,"E22"),sQuery(id+"F0.wireOp",EDGE,"E23"),sQuery(id+"F0.wireOp",EDGE,"E24"),sQuery(id+"F0.wireOp",EDGE,"E25"),sQuery(id+"F0.wireOp",EDGE,"E26"),sQuery(id+"F0.wireOp",EDGE,"E27"),sQuery(id+"F0.wireOp",EDGE,"E28"),sQuery(id+"F0.wireOp",EDGE,"E29"),sQuery(id+"F0.wireOp",EDGE,"E30"),sQuery(id+"F0.wireOp",EDGE,"E31"),sQuery(id+"F0.wireOp",EDGE,"E32"),sQuery(id+"F0.wireOp",EDGE,"E33"),sQuery(id+"F0.wireOp",EDGE,"E34"),sQuery(id+"F0.wireOp",EDGE,"E35"),sQuery(id+"F0.wireOp",EDGE,"E36"),sQuery(id+"F0.wireOp",EDGE,"E37"),sQuery(id+"F0.wireOp",EDGE,"E38"),sQuery(id+"F0.wireOp",EDGE,"E39"),sQuery(id+"F0.wireOp",EDGE,"E40"),sQuery(id+"F0.wireOp",EDGE,"E41"),sQuery(id+"F0.wireOp",EDGE,"E42"),sQuery(id+"F0.wireOp",EDGE,"E43"),sQuery(id+"F0.wireOp",EDGE,"E44"),sQuery(id+"F0.wireOp",EDGE,"E45"),sQuery(id+"F0.wireOp",EDGE,"E46"),sQuery(id+"F0.wireOp",EDGE,"E47"),sQuery(id+"F0.wireOp",EDGE,"E48"),sQuery(id+"F0.wireOp",EDGE,"E49"),sQuery(id+"F0.wireOp",EDGE,"E50"),sQuery(id+"F0.wireOp",EDGE,"E51"),sQuery(id+"F0.wireOp",EDGE,"E52"),sQuery(id+"F0.wireOp",EDGE,"E53"),sQuery(id+"F0.wireOp",EDGE,"E54"),sQuery(id+"F0.wireOp",EDGE,"E55"),sQuery(id+"F0.wireOp",EDGE,"E56"),sQuery(id+"F0.wireOp",EDGE,"E57"),sQuery(id+"F0.wireOp",EDGE,"E58"),sQuery(id+"F0.wireOp",EDGE,"E59"),sQuery(id+"F0.wireOp",EDGE,"E60"),sQuery(id+"F0.wireOp",EDGE,"E61"),sQuery(id+"F0.wireOp",EDGE,"E62"),sQuery(id+"F0.wireOp",EDGE,"E63"),sQuery(id+"F0.wireOp",EDGE,"E64"),sQuery(id+"F0.wireOp",EDGE,"E65"),sQuery(id+"F0.wireOp",EDGE,"E66"),sQuery(id+"F0.wireOp",EDGE,"E67"),sQuery(id+"F0.wireOp",EDGE,"E68"),sQuery(id+"F0.wireOp",EDGE,"E69"),sQuery(id+"F0.wireOp",EDGE,"E70"),sQuery(id+"F0.wireOp",EDGE,"E71"),sQuery(id+"F0.wireOp",EDGE,"E72"),sQuery(id+"F0.wireOp",EDGE,"E73"),sQuery(id+"F0.wireOp",EDGE,"E74"),sQuery(id+"F0.wireOp",EDGE,"E75"),sQuery(id+"F0.wireOp",EDGE,"E76"),sQuery(id+"F0.wireOp",EDGE,"E77"),sQuery(id+"F0.wireOp",EDGE,"E78"),sQuery(id+"F0.wireOp",EDGE,"E79"),sQuery(id+"F0.wireOp",EDGE,"E80"),sQuery(id+"F0.wireOp",EDGE,"E81"),sQuery(id+"F0.wireOp",EDGE,"E82"),sQuery(id+"F0.wireOp",EDGE,"E83"),sQuery(id+"F0.wireOp",EDGE,"E84"),sQuery(id+"F0.wireOp",EDGE,"E85"),sQuery(id+"F0.wireOp",EDGE,"E86"),sQuery(id+"F0.wireOp",EDGE,"E87"),sQuery(id+"F0.wireOp",EDGE,"E88"),sQuery(id+"F0.wireOp",EDGE,"E89"),sQuery(id+"F0.wireOp",EDGE,"E90"),sQuery(id+"F0.wireOp",EDGE,"E91"),sQuery(id+"F0.wireOp",EDGE,"E92"),sQuery(id+"F0.wireOp",EDGE,"E93"),sQuery(id+"F0.wireOp",EDGE,"E94"),sQuery(id+"F0.wireOp",EDGE,"E95"),sQuery(id+"F0.wireOp",EDGE,"E96"),sQuery(id+"F0.wireOp",EDGE,"E97"),sQuery(id+"F0.wireOp",EDGE,"E98"),sQuery(id+"F0.wireOp",EDGE,"E99"),sQuery(id+"F0.wireOp",EDGE,"E100"),sQuery(id+"F0.wireOp",EDGE,"E101"),sQuery(id+"F0.wireOp",EDGE,"E102"),sQuery(id+"F0.wireOp",EDGE,"E103"),sQuery(id+"F0.wireOp",EDGE,"E104"),sQuery(id+"F0.wireOp",EDGE,"E105"),sQuery(id+"F0.wireOp",EDGE,"E106"),sQuery(id+"F0.wireOp",EDGE,"E107"),sQuery(id+"F0.wireOp",EDGE,"E108"),sQuery(id+"F0.wireOp",EDGE,"E109"),sQuery(id+"F0.wireOp",EDGE,"E110"),sQuery(id+"F0.wireOp",EDGE,"E111"),sQuery(id+"F0.wireOp",EDGE,"E112"),sQuery(id+"F0.wireOp",EDGE,"E113"),sQuery(id+"F0.wireOp",EDGE,"E114"),sQuery(id+"F0.wireOp",EDGE,"E115"),sQuery(id+"F0.wireOp",EDGE,"E116"),sQuery(id+"F0.wireOp",EDGE,"E117"),sQuery(id+"F0.wireOp",EDGE,"E118"),sQuery(id+"F0.wireOp",EDGE,"E119"),sQuery(id+"F0.wireOp",EDGE,"E120"),sQuery(id+"F0.wireOp",EDGE,"E121"),sQuery(id+"F0.wireOp",EDGE,"E122"),sQuery(id+"F0.wireOp",EDGE,"E123"),sQuery(id+"F0.wireOp",EDGE,"E124"),sQuery(id+"F0.wireOp",EDGE,"E125"),sQuery(id+"F0.wireOp",EDGE,"E126"),sQuery(id+"F0.wireOp",EDGE,"E127"),sQuery(id+"F0.wireOp",EDGE,"E128"),sQuery(id+"F0.wireOp",EDGE,"E129"),sQuery(id+"F0.wireOp",EDGE,"E130"),sQuery(id+"F0.wireOp",EDGE,"E131"),sQuery(id+"F0.wireOp",EDGE,"E132"),sQuery(id+"F0.wireOp",EDGE,"E133"),sQuery(id+"F0.wireOp",EDGE,"E134"),sQuery(id+"F0.wireOp",EDGE,"E135"),sQuery(id+"F0.wireOp",EDGE,"E136"),sQuery(id+"F0.wireOp",EDGE,"E137"),sQuery(id+"F0.wireOp",EDGE,"E138"),sQuery(id+"F0.wireOp",EDGE,"E139"),sQuery(id+"F0.wireOp",EDGE,"E140"),sQuery(id+"F0.wireOp",EDGE,"E141"),sQuery(id+"F0.wireOp",EDGE,"E142"),sQuery(id+"F0.wireOp",EDGE,"E143"),sQuery(id+"F0.wireOp",EDGE,"E144"),sQuery(id+"F0.wireOp",EDGE,"E145"),sQuery(id+"F0.wireOp",EDGE,"E146"),sQuery(id+"F0.wireOp",EDGE,"E147"),sQuery(id+"F0.wireOp",EDGE,"E148"),sQuery(id+"F0.wireOp",EDGE,"E149"),sQuery(id+"F0.wireOp",EDGE,"E150"),sQuery(id+"F0.wireOp",EDGE,"E151"),sQuery(id+"F0.wireOp",EDGE,"E152"),sQuery(id+"F0.wireOp",EDGE,"E153"),sQuery(id+"F0.wireOp",EDGE,"E154"),sQuery(id+"F0.wireOp",EDGE,"E155"),sQuery(id+"F0.wireOp",EDGE,"E156"),sQuery(id+"F0.wireOp",EDGE,"E157"),sQuery(id+"F0.wireOp",EDGE,"E158"),sQuery(id+"F0.wireOp",EDGE,"E159"),sQuery(id+"F0.wireOp",EDGE,"E160"),sQuery(id+"F0.wireOp",EDGE,"E161"),sQuery(id+"F0.wireOp",EDGE,"E162"),sQuery(id+"F0.wireOp",EDGE,"E163"),sQuery(id+"F0.wireOp",EDGE,"E164"),sQuery(id+"F0.wireOp",EDGE,"E165"),sQuery(id+"F0.wireOp",EDGE,"E166"),sQuery(id+"F0.wireOp",EDGE,"E167"),sQuery(id+"F0.wireOp",EDGE,"E168"),sQuery(id+"F0.wireOp",EDGE,"E169"),sQuery(id+"F0.wireOp",EDGE,"E170"),sQuery(id+"F0.wireOp",EDGE,"E171"),sQuery(id+"F0.wireOp",EDGE,"E172"),sQuery(id+"F0.wireOp",EDGE,"E173"),sQuery(id+"F0.wireOp",EDGE,"E174"),sQuery(id+"F0.wireOp",EDGE,"E175"),sQuery(id+"F0.wireOp",EDGE,"E176"),sQuery(id+"F0.wireOp",EDGE,"E177"),sQuery(id+"F0.wireOp",EDGE,"E178"),sQuery(id+"F0.wireOp",EDGE,"E179"),sQuery(id+"F0.wireOp",EDGE,"E180"),sQuery(id+"F0.wireOp",EDGE,"E181"),sQuery(id+"F0.wireOp",EDGE,"E182"),sQuery(id+"F0.wireOp",EDGE,"E183"),sQuery(id+"F0.wireOp",EDGE,"E184"),sQuery(id+"F0.wireOp",EDGE,"E185"),sQuery(id+"F0.wireOp",EDGE,"E186"),sQuery(id+"F0.wireOp",EDGE,"E187"),sQuery(id+"F0.wireOp",EDGE,"E188"),sQuery(id+"F0.wireOp",EDGE,"E189"),sQuery(id+"F0.wireOp",EDGE,"E190"),sQuery(id+"F0.wireOp",EDGE,"E191"),sQuery(id+"F0.wireOp",EDGE,"E192"),sQuery(id+"F0.wireOp",EDGE,"E193"),sQuery(id+"F0.wireOp",EDGE,"E194"),sQuery(id+"F0.wireOp",EDGE,"E195"),sQuery(id+"F0.wireOp",EDGE,"E196"),sQuery(id+"F0.wireOp",EDGE,"E197"),sQuery(id+"F0.wireOp",EDGE,"E198"),sQuery(id+"F0.wireOp",EDGE,"E199"),sQuery(id+"F0.wireOp",EDGE,"E200"),sQuery(id+"F0.wireOp",EDGE,"E201"),sQuery(id+"F0.wireOp",EDGE,"E202"),sQuery(id+"F0.wireOp",EDGE,"E203"),sQuery(id+"F0.wireOp",EDGE,"E204"),sQuery(id+"F0.wireOp",EDGE,"E205"),sQuery(id+"F0.wireOp",EDGE,"E206"),sQuery(id+"F0.wireOp",EDGE,"E207"),sQuery(id+"F0.wireOp",EDGE,"E208"),sQuery(id+"F0.wireOp",EDGE,"E209"),sQuery(id+"F0.wireOp",EDGE,"E210"),sQuery(id+"F0.wireOp",EDGE,"E211"),sQuery(id+"F0.wireOp",EDGE,"E212"),sQuery(id+"F0.wireOp",EDGE,"E213"),sQuery(id+"F0.wireOp",EDGE,"E214"),sQuery(id+"F0.wireOp",EDGE,"E215"),sQuery(id+"F0.wireOp",EDGE,"E216"),sQuery(id+"F0.wireOp",EDGE,"E217"),sQuery(id+"F0.wireOp",EDGE,"E218"),sQuery(id+"F0.wireOp",EDGE,"E219"),sQuery(id+"F0.wireOp",EDGE,"E220"),sQuery(id+"F0.wireOp",EDGE,"E221"),sQuery(id+"F0.wireOp",EDGE,"E222"),sQuery(id+"F0.wireOp",EDGE,"E223"),sQuery(id+"F0.wireOp",EDGE,"E224"),sQuery(id+"F0.wireOp",EDGE,"E225"),sQuery(id+"F0.wireOp",EDGE,"E226"),sQuery(id+"F0.wireOp",EDGE,"E227"),sQuery(id+"F0.wireOp",EDGE,"E228"),sQuery(id+"F0.wireOp",EDGE,"E229"),sQuery(id+"F0.wireOp",EDGE,"E230"),sQuery(id+"F0.wireOp",EDGE,"E231"),sQuery(id+"F0.wireOp",EDGE,"E232"),sQuery(id+"F0.wireOp",EDGE,"E233"),sQuery(id+"F0.wireOp",EDGE,"E234"),sQuery(id+"F0.wireOp",EDGE,"E235"),sQuery(id+"F0.wireOp",EDGE,"E236"),sQuery(id+"F0.wireOp",EDGE,"E237"),sQuery(id+"F0.wireOp",EDGE,"E238"),sQuery(id+"F0.wireOp",EDGE,"E239"),sQuery(id+"F0.wireOp",EDGE,"E240"),sQuery(id+"F0.wireOp",EDGE,"E241"),sQuery(id+"F0.wireOp",EDGE,"E242"),sQuery(id+"F0.wireOp",EDGE,"E243"),sQuery(id+"F0.wireOp",EDGE,"E244"),sQuery(id+"F0.wireOp",EDGE,"E245"),sQuery(id+"F0.wireOp",EDGE,"E246"),sQuery(id+"F0.wireOp",EDGE,"E247"),sQuery(id+"F0.wireOp",EDGE,"E248"),sQuery(id+"F0.wireOp",EDGE,"E249"),sQuery(id+"F0.wireOp",EDGE,"E250"),sQuery(id+"F0.wireOp",EDGE,"E251"),sQuery(id+"F0.wireOp",EDGE,"E252"),sQuery(id+"F0.wireOp",EDGE,"E253"),sQuery(id+"F0.wireOp",EDGE,"E254"),sQuery(id+"F0.wireOp",EDGE,"E255"),sQuery(id+"F0.wireOp",EDGE,"E256"),sQuery(id+"F0.wireOp",EDGE,"E257"),sQuery(id+"F0.wireOp",EDGE,"E258"),sQuery(id+"F0.wireOp",EDGE,"E259"),sQuery(id+"F0.wireOp",EDGE,"E260"),sQuery(id+"F0.wireOp",EDGE,"E261"),sQuery(id+"F0.wireOp",EDGE,"E262"),sQuery(id+"F0.wireOp",EDGE,"E263"),sQuery(id+"F0.wireOp",EDGE,"E264"),sQuery(id+"F0.wireOp",EDGE,"E265"),sQuery(id+"F0.wireOp",EDGE,"E266"),sQuery(id+"F0.wireOp",EDGE,"E267"),sQuery(id+"F0.wireOp",EDGE,"E268"),sQuery(id+"F0.wireOp",EDGE,"E269"),sQuery(id+"F0.wireOp",EDGE,"E270"),sQuery(id+"F0.wireOp",EDGE,"E271"),sQuery(id+"F0.wireOp",EDGE,"E272"),sQuery(id+"F0.wireOp",EDGE,"E273"),sQuery(id+"F0.wireOp",EDGE,"E274"),sQuery(id+"F0.wireOp",EDGE,"E275"),sQuery(id+"F0.wireOp",EDGE,"E276"),sQuery(id+"F0.wireOp",EDGE,"E277"),sQuery(id+"F0.wireOp",EDGE,"E278"),sQuery(id+"F0.wireOp",EDGE,"E279"),sQuery(id+"F0.wireOp",EDGE,"E280"),sQuery(id+"F0.wireOp",EDGE,"E281"),sQuery(id+"F0.wireOp",EDGE,"E282"),sQuery(id+"F0.wireOp",EDGE,"E283"),sQuery(id+"F0.wireOp",EDGE,"E284"),sQuery(id+"F0.wireOp",EDGE,"E285"),sQuery(id+"F0.wireOp",EDGE,"E286"),sQuery(id+"F0.wireOp",EDGE,"E287"),sQuery(id+"F0.wireOp",EDGE,"E288"),sQuery(id+"F0.wireOp",EDGE,"E289"),sQuery(id+"F0.wireOp",EDGE,"E290"),sQuery(id+"F0.wireOp",EDGE,"E291"),sQuery(id+"F0.wireOp",EDGE,"E292"),sQuery(id+"F0.wireOp",EDGE,"E293"),sQuery(id+"F0.wireOp",EDGE,"E294"),sQuery(id+"F0.wireOp",EDGE,"E295"),sQuery(id+"F0.wireOp",EDGE,"E296"),sQuery(id+"F0.wireOp",EDGE,"E297"),sQuery(id+"F0.wireOp",EDGE,"E298"),sQuery(id+"F0.wireOp",EDGE,"E299"),sQuery(id+"F0.wireOp",EDGE,"E300"),sQuery(id+"F0.wireOp",EDGE,"E301"),sQuery(id+"F0.wireOp",EDGE,"E302"),sQuery(id+"F0.wireOp",EDGE,"E303"),sQuery(id+"F0.wireOp",EDGE,"E304"),sQuery(id+"F0.wireOp",EDGE,"E305"),sQuery(id+"F0.wireOp",EDGE,"E306"),sQuery(id+"F0.wireOp",EDGE,"E307"),sQuery(id+"F0.wireOp",EDGE,"E308"),sQuery(id+"F0.wireOp",EDGE,"E309"),sQuery(id+"F0.wireOp",EDGE,"E310"),sQuery(id+"F0.wireOp",EDGE,"E311"),sQuery(id+"F0.wireOp",EDGE,"E312"),sQuery(id+"F0.wireOp",EDGE,"E313"),sQuery(id+"F0.wireOp",EDGE,"E314"),sQuery(id+"F0.wireOp",EDGE,"E315"),sQuery(id+"F0.wireOp",EDGE,"E316"),sQuery(id+"F0.wireOp",EDGE,"E317"),sQuery(id+"F0.wireOp",EDGE,"E318"),sQuery(id+"F0.wireOp",EDGE,"E319"),sQuery(id+"F0.wireOp",EDGE,"E320"),sQuery(id+"F0.wireOp",EDGE,"E321"),sQuery(id+"F0.wireOp",EDGE,"E322"),sQuery(id+"F0.wireOp",EDGE,"E323"),sQuery(id+"F0.wireOp",EDGE,"E324"),sQuery(id+"F0.wireOp",EDGE,"E325"),sQuery(id+"F0.wireOp",EDGE,"E326"),sQuery(id+"F0.wireOp",EDGE,"E327"),sQuery(id+"F0.wireOp",EDGE,"E328"),sQuery(id+"F0.wireOp",EDGE,"E329"),sQuery(id+"F0.wireOp",EDGE,"E330"),sQuery(id+"F0.wireOp",EDGE,"E331"),sQuery(id+"F0.wireOp",EDGE,"E332"),sQuery(id+"F0.wireOp",EDGE,"E333"),sQuery(id+"F0.wireOp",EDGE,"E334"),sQuery(id+"F0.wireOp",EDGE,"E335"),sQuery(id+"F0.wireOp",EDGE,"E336"),sQuery(id+"F0.wireOp",EDGE,"E337"),sQuery(id+"F0.wireOp",EDGE,"E338"),sQuery(id+"F0.wireOp",EDGE,"E339"),sQuery(id+"F0.wireOp",EDGE,"E340"),sQuery(id+"F0.wireOp",EDGE,"E341"),sQuery(id+"F0.wireOp",EDGE,"E342"),sQuery(id+"F0.wireOp",EDGE,"E343"),sQuery(id+"F0.wireOp",EDGE,"E344"),sQuery(id+"F0.wireOp",EDGE,"E345"),sQuery(id+"F0.wireOp",EDGE,"E346"),sQuery(id+"F0.wireOp",EDGE,"E347"),sQuery(id+"F0.wireOp",EDGE,"E348"),sQuery(id+"F0.wireOp",EDGE,"E349"),sQuery(id+"F0.wireOp",EDGE,"E350"),sQuery(id+"F0.wireOp",EDGE,"E351"),sQuery(id+"F0.wireOp",EDGE,"E352"),sQuery(id+"F0.wireOp",EDGE,"E353"),sQuery(id+"F0.wireOp",EDGE,"E354"),sQuery(id+"F0.wireOp",EDGE,"E355"),sQuery(id+"F0.wireOp",EDGE,"E356"),sQuery(id+"F0.wireOp",EDGE,"E357"),sQuery(id+"F0.wireOp",EDGE,"E358"),sQuery(id+"F0.wireOp",EDGE,"E359"),sQuery(id+"F0.wireOp",EDGE,"E360"),sQuery(id+"F0.wireOp",EDGE,"E361"),sQuery(id+"F0.wireOp",EDGE,"E362"),sQuery(id+"F0.wireOp",EDGE,"E363"),sQuery(id+"F0.wireOp",EDGE,"E364"),sQuery(id+"F0.wireOp",EDGE,"E365"),sQuery(id+"F0.wireOp",EDGE,"E366"),sQuery(id+"F0.wireOp",EDGE,"E367"),sQuery(id+"F0.wireOp",EDGE,"E368"),sQuery(id+"F0.wireOp",EDGE,"E369"),sQuery(id+"F0.wireOp",EDGE,"E370"),sQuery(id+"F0.wireOp",EDGE,"E371"),sQuery(id+"F0.wireOp",EDGE,"E372"),sQuery(id+"F0.wireOp",EDGE,"E373"),sQuery(id+"F0.wireOp",EDGE,"E374"),sQuery(id+"F0.wireOp",EDGE,"E375"),sQuery(id+"F0.wireOp",EDGE,"E376"),sQuery(id+"F0.wireOp",EDGE,"E377"),sQuery(id+"F0.wireOp",EDGE,"E378"),sQuery(id+"F0.wireOp",EDGE,"E379"),sQuery(id+"F0.wireOp",EDGE,"E380"),sQuery(id+"F0.wireOp",EDGE,"E381"),sQuery(id+"F0.wireOp",EDGE,"E383"),sQuery(id+"F0.wireOp",EDGE,"E384"),sQuery(id+"F0.wireOp",EDGE,"E385"),sQuery(id+"F0.wireOp",EDGE,"E386"),sQuery(id+"F0.wireOp",EDGE,"E387"),sQuery(id+"F0.wireOp",EDGE,"E388"),sQuery(id+"F0.wireOp",EDGE,"E389"),sQuery(id+"F0.wireOp",EDGE,"E390"),sQuery(id+"F0.wireOp",EDGE,"E391"),sQuery(id+"F0.wireOp",EDGE,"E392"),sQuery(id+"F0.wireOp",EDGE,"E393"),sQuery(id+"F0.wireOp",EDGE,"E394"),sQuery(id+"F0.wireOp",EDGE,"E395"),sQuery(id+"F0.wireOp",EDGE,"E396"),sQuery(id+"F0.wireOp",EDGE,"E397"),sQuery(id+"F0.wireOp",EDGE,"E398"),sQuery(id+"F0.wireOp",EDGE,"E399"),sQuery(id+"F0.wireOp",EDGE,"E400"),sQuery(id+"F0.wireOp",EDGE,"E401"),sQuery(id+"F0.wireOp",EDGE,"E402"),sQuery(id+"F0.wireOp",EDGE,"E403"),sQuery(id+"F0.wireOp",EDGE,"E404"),sQuery(id+"F0.wireOp",EDGE,"E405"),sQuery(id+"F0.wireOp",EDGE,"E406"),sQuery(id+"F0.wireOp",EDGE,"E407"),sQuery(id+"F0.wireOp",EDGE,"E408"),sQuery(id+"F0.wireOp",EDGE,"E409"),sQuery(id+"F0.wireOp",EDGE,"E410"),sQuery(id+"F0.wireOp",EDGE,"E411"),sQuery(id+"F0.wireOp",EDGE,"E412"),sQuery(id+"F0.wireOp",EDGE,"E413"),sQuery(id+"F0.wireOp",EDGE,"E414"),sQuery(id+"F0.wireOp",EDGE,"E415"),sQuery(id+"F0.wireOp",EDGE,"E416"),sQuery(id+"F0.wireOp",EDGE,"E417"),sQuery(id+"F0.wireOp",EDGE,"E418"),sQuery(id+"F0.wireOp",EDGE,"E419"),sQuery(id+"F0.wireOp",EDGE,"E420"),sQuery(id+"F0.wireOp",EDGE,"E421"),sQuery(id+"F0.wireOp",EDGE,"E422"),sQuery(id+"F0.wireOp",EDGE,"E423"),sQuery(id+"F0.wireOp",EDGE,"E424"),sQuery(id+"F0.wireOp",EDGE,"E425"),sQuery(id+"F0.wireOp",EDGE,"E426"),sQuery(id+"F0.wireOp",EDGE,"E427"),sQuery(id+"F0.wireOp",EDGE,"E428"),sQuery(id+"F0.wireOp",EDGE,"E429"),sQuery(id+"F0.wireOp",EDGE,"E430"),sQuery(id+"F0.wireOp",EDGE,"E431"),sQuery(id+"F0.wireOp",EDGE,"E432"),sQuery(id+"F0.wireOp",EDGE,"E433"),sQuery(id+"F0.wireOp",EDGE,"E434"),sQuery(id+"F0.wireOp",EDGE,"E435"),sQuery(id+"F0.wireOp",EDGE,"E436"),sQuery(id+"F0.wireOp",EDGE,"E437"),sQuery(id+"F0.wireOp",EDGE,"E438"),sQuery(id+"F0.wireOp",EDGE,"E439"),sQuery(id+"F0.wireOp",EDGE,"E440"),sQuery(id+"F0.wireOp",EDGE,"E441"),sQuery(id+"F0.wireOp",EDGE,"E442"),sQuery(id+"F0.wireOp",EDGE,"E443"),sQuery(id+"F0.wireOp",EDGE,"E444"),sQuery(id+"F0.wireOp",EDGE,"E445"),sQuery(id+"F0.wireOp",EDGE,"E446"),sQuery(id+"F0.wireOp",EDGE,"E447"),sQuery(id+"F0.wireOp",EDGE,"E448"),sQuery(id+"F0.wireOp",EDGE,"E449"),sQuery(id+"F0.wireOp",EDGE,"E450"),sQuery(id+"F0.wireOp",EDGE,"E451"),sQuery(id+"F0.wireOp",EDGE,"E452"),sQuery(id+"F0.wireOp",EDGE,"E453"),sQuery(id+"F0.wireOp",EDGE,"E454"),sQuery(id+"F0.wireOp",EDGE,"E455"),sQuery(id+"F0.wireOp",EDGE,"E456"),sQuery(id+"F0.wireOp",EDGE,"E457"),sQuery(id+"F0.wireOp",EDGE,"E458"),sQuery(id+"F0.wireOp",EDGE,"E459"),sQuery(id+"F0.wireOp",EDGE,"E460"),sQuery(id+"F0.wireOp",EDGE,"E461"),sQuery(id+"F0.wireOp",EDGE,"E462"),sQuery(id+"F0.wireOp",EDGE,"E463"),sQuery(id+"F0.wireOp",EDGE,"E464"),sQuery(id+"F0.wireOp",EDGE,"E465"),sQuery(id+"F0.wireOp",EDGE,"E466"),sQuery(id+"F0.wireOp",EDGE,"E467"),sQuery(id+"F0.wireOp",EDGE,"E468"),sQuery(id+"F0.wireOp",EDGE,"E469"),sQuery(id+"F0.wireOp",EDGE,"E470"),sQuery(id+"F0.wireOp",EDGE,"E471"),sQuery(id+"F0.wireOp",EDGE,"E472"),sQuery(id+"F0.wireOp",EDGE,"E473"),sQuery(id+"F0.wireOp",EDGE,"E474"),sQuery(id+"F0.wireOp",EDGE,"E475"),sQuery(id+"F0.wireOp",EDGE,"E476"),sQuery(id+"F0.wireOp",EDGE,"E477"),sQuery(id+"F0.wireOp",EDGE,"E478"),sQuery(id+"F0.wireOp",EDGE,"E479"),sQuery(id+"F0.wireOp",EDGE,"E480"),sQuery(id+"F0.wireOp",EDGE,"E481"),sQuery(id+"F0.wireOp",EDGE,"E482"),sQuery(id+"F0.wireOp",EDGE,"E483"),sQuery(id+"F0.wireOp",EDGE,"E484"),sQuery(id+"F0.wireOp",EDGE,"E485"),sQuery(id+"F0.wireOp",EDGE,"E486"),sQuery(id+"F0.wireOp",EDGE,"E487"),sQuery(id+"F0.wireOp",EDGE,"E488"),sQuery(id+"F0.wireOp",EDGE,"E489"),sQuery(id+"F0.wireOp",EDGE,"E490"),sQuery(id+"F0.wireOp",EDGE,"E491"),sQuery(id+"F0.wireOp",EDGE,"E492"),sQuery(id+"F0.wireOp",EDGE,"E493"),sQuery(id+"F0.wireOp",EDGE,"E494"),sQuery(id+"F0.wireOp",EDGE,"E495"),sQuery(id+"F0.wireOp",EDGE,"E496"),sQuery(id+"F0.wireOp",EDGE,"E497"),sQuery(id+"F0.wireOp",EDGE,"E498"),sQuery(id+"F0.wireOp",EDGE,"E499"),sQuery(id+"F0.wireOp",EDGE,"E500"),sQuery(id+"F0.wireOp",EDGE,"E501"),sQuery(id+"F0.wireOp",EDGE,"E502"),sQuery(id+"F0.wireOp",EDGE,"E503"),sQuery(id+"F0.wireOp",EDGE,"E504"),sQuery(id+"F0.wireOp",EDGE,"E505"),sQuery(id+"F0.wireOp",EDGE,"E506"),sQuery(id+"F0.wireOp",EDGE,"E507"),sQuery(id+"F0.wireOp",EDGE,"E508"),sQuery(id+"F0.wireOp",EDGE,"E509"),sQuery(id+"F0.wireOp",EDGE,"E510"),sQuery(id+"F0.wireOp",EDGE,"E511"),sQuery(id+"F0.wireOp",EDGE,"E512"),sQuery(id+"F0.wireOp",EDGE,"E513"),sQuery(id+"F0.wireOp",EDGE,"E514"),sQuery(id+"F0.wireOp",EDGE,"E515"),sQuery(id+"F0.wireOp",EDGE,"E516"),sQuery(id+"F0.wireOp",EDGE,"E517"),sQuery(id+"F0.wireOp",EDGE,"E518"),sQuery(id+"F0.wireOp",EDGE,"E519"),sQuery(id+"F0.wireOp",EDGE,"E520"),sQuery(id+"F0.wireOp",EDGE,"E521"),sQuery(id+"F0.wireOp",EDGE,"E522"),sQuery(id+"F0.wireOp",EDGE,"E523"),sQuery(id+"F0.wireOp",EDGE,"E524"),sQuery(id+"F0.wireOp",EDGE,"E525"),sQuery(id+"F0.wireOp",EDGE,"E526"),sQuery(id+"F0.wireOp",EDGE,"E527"),sQuery(id+"F0.wireOp",EDGE,"E528"),sQuery(id+"F0.wireOp",EDGE,"E529"),sQuery(id+"F0.wireOp",EDGE,"E530"),sQuery(id+"F0.wireOp",EDGE,"E531"),sQuery(id+"F0.wireOp",EDGE,"E532"),sQuery(id+"F0.wireOp",EDGE,"E533"),sQuery(id+"F0.wireOp",EDGE,"E534"),sQuery(id+"F0.wireOp",EDGE,"E535"),sQuery(id+"F0.wireOp",EDGE,"E536"),sQuery(id+"F0.wireOp",EDGE,"E537"),sQuery(id+"F0.wireOp",EDGE,"E538"),sQuery(id+"F0.wireOp",EDGE,"E539"),sQuery(id+"F0.wireOp",EDGE,"E540"),sQuery(id+"F0.wireOp",EDGE,"E541"),sQuery(id+"F0.wireOp",EDGE,"E542"),sQuery(id+"F0.wireOp",EDGE,"E543"),sQuery(id+"F0.wireOp",EDGE,"E544"),sQuery(id+"F0.wireOp",EDGE,"E545"),sQuery(id+"F0.wireOp",EDGE,"E546"),sQuery(id+"F0.wireOp",EDGE,"E547"),sQuery(id+"F0.wireOp",EDGE,"E548"),sQuery(id+"F0.wireOp",EDGE,"E549"),sQuery(id+"F0.wireOp",EDGE,"E550"),sQuery(id+"F0.wireOp",EDGE,"E551"),sQuery(id+"F0.wireOp",EDGE,"E552"),sQuery(id+"F0.wireOp",EDGE,"E553"),sQuery(id+"F0.wireOp",EDGE,"E554"),sQuery(id+"F0.wireOp",EDGE,"E555"),sQuery(id+"F0.wireOp",EDGE,"E556"),sQuery(id+"F0.wireOp",EDGE,"E557"),sQuery(id+"F0.wireOp",EDGE,"E558"),sQuery(id+"F0.wireOp",EDGE,"E559"),sQuery(id+"F0.wireOp",EDGE,"E560"),sQuery(id+"F0.wireOp",EDGE,"E561"),sQuery(id+"F0.wireOp",EDGE,"E562"),sQuery(id+"F0.wireOp",EDGE,"E563"),sQuery(id+"F0.wireOp",EDGE,"E564"),sQuery(id+"F0.wireOp",EDGE,"E565"),sQuery(id+"F0.wireOp",EDGE,"E566"),sQuery(id+"F0.wireOp",EDGE,"E567"),sQuery(id+"F0.wireOp",EDGE,"E568"),sQuery(id+"F0.wireOp",EDGE,"E569"),sQuery(id+"F0.wireOp",EDGE,"E570"),sQuery(id+"F0.wireOp",EDGE,"E571"),sQuery(id+"F0.wireOp",EDGE,"E572"),sQuery(id+"F0.wireOp",EDGE,"E573"),sQuery(id+"F0.wireOp",EDGE,"E574"),sQuery(id+"F0.wireOp",EDGE,"E575"),sQuery(id+"F0.wireOp",EDGE,"E576"),sQuery(id+"F0.wireOp",EDGE,"E577"),sQuery(id+"F0.wireOp",EDGE,"E578"),sQuery(id+"F0.wireOp",EDGE,"E579"),sQuery(id+"F0.wireOp",EDGE,"E580"),sQuery(id+"F0.wireOp",EDGE,"E581"),sQuery(id+"F0.wireOp",EDGE,"E582"),sQuery(id+"F0.wireOp",EDGE,"E583"),sQuery(id+"F0.wireOp",EDGE,"E584"),sQuery(id+"F0.wireOp",EDGE,"E585"),sQuery(id+"F0.wireOp",EDGE,"E586"),sQuery(id+"F0.wireOp",EDGE,"E587"),sQuery(id+"F0.wireOp",EDGE,"E588"),sQuery(id+"F0.wireOp",EDGE,"E589"),sQuery(id+"F0.wireOp",EDGE,"E590"),sQuery(id+"F0.wireOp",EDGE,"E591"),sQuery(id+"F0.wireOp",EDGE,"E592"),sQuery(id+"F0.wireOp",EDGE,"E593"),sQuery(id+"F0.wireOp",EDGE,"E594"),sQuery(id+"F0.wireOp",EDGE,"E595"),sQuery(id+"F0.wireOp",EDGE,"E596"),sQuery(id+"F0.wireOp",EDGE,"E597"),sQuery(id+"F0.wireOp",EDGE,"E598"),sQuery(id+"F0.wireOp",EDGE,"E599"),sQuery(id+"F0.wireOp",EDGE,"E600"),sQuery(id+"F0.wireOp",EDGE,"E601"),sQuery(id+"F0.wireOp",EDGE,"E602"),sQuery(id+"F0.wireOp",EDGE,"E603"),sQuery(id+"F0.wireOp",EDGE,"E604"),sQuery(id+"F0.wireOp",EDGE,"E605"),sQuery(id+"F0.wireOp",EDGE,"E606"),sQuery(id+"F0.wireOp",EDGE,"E607"),sQuery(id+"F0.wireOp",EDGE,"E608"),sQuery(id+"F0.wireOp",EDGE,"E609"),sQuery(id+"F0.wireOp",EDGE,"E610"),sQuery(id+"F0.wireOp",EDGE,"E611"),sQuery(id+"F0.wireOp",EDGE,"E612"),sQuery(id+"F0.wireOp",EDGE,"E613"),sQuery(id+"F0.wireOp",EDGE,"E614"),sQuery(id+"F0.wireOp",EDGE,"E615"),sQuery(id+"F0.wireOp",EDGE,"E616"),sQuery(id+"F0.wireOp",EDGE,"E617"),sQuery(id+"F0.wireOp",EDGE,"E618"),sQuery(id+"F0.wireOp",EDGE,"E619"),sQuery(id+"F0.wireOp",EDGE,"E620"),sQuery(id+"F0.wireOp",EDGE,"E621"),sQuery(id+"F0.wireOp",EDGE,"E622"),sQuery(id+"F0.wireOp",EDGE,"E623"),sQuery(id+"F0.wireOp",EDGE,"E624"),sQuery(id+"F0.wireOp",EDGE,"E625"),sQuery(id+"F0.wireOp",EDGE,"E626"),sQuery(id+"F0.wireOp",EDGE,"E627"),sQuery(id+"F0.wireOp",EDGE,"E628"),sQuery(id+"F0.wireOp",EDGE,"E629"),sQuery(id+"F0.wireOp",EDGE,"E630"),sQuery(id+"F0.wireOp",EDGE,"E631"),sQuery(id+"F0.wireOp",EDGE,"E632"),sQuery(id+"F0.wireOp",EDGE,"E633"),sQuery(id+"F0.wireOp",EDGE,"E634"),sQuery(id+"F0.wireOp",EDGE,"E635"),sQuery(id+"F0.wireOp",EDGE,"E636"),sQuery(id+"F0.wireOp",EDGE,"E637"),sQuery(id+"F0.wireOp",EDGE,"E638"),sQuery(id+"F0.wireOp",EDGE,"E639"),sQuery(id+"F0.wireOp",EDGE,"E640"),sQuery(id+"F0.wireOp",EDGE,"E641"),sQuery(id+"F0.wireOp",EDGE,"E642"),sQuery(id+"F0.wireOp",EDGE,"E643"),sQuery(id+"F0.wireOp",EDGE,"E644"),sQuery(id+"F0.wireOp",EDGE,"E645"),sQuery(id+"F0.wireOp",EDGE,"E646"),sQuery(id+"F0.wireOp",EDGE,"E647"),sQuery(id+"F0.wireOp",EDGE,"E648"),sQuery(id+"F0.wireOp",EDGE,"E649"),sQuery(id+"F0.wireOp",EDGE,"E650"),sQuery(id+"F0.wireOp",EDGE,"E651"),sQuery(id+"F0.wireOp",EDGE,"E652"),sQuery(id+"F0.wireOp",EDGE,"E653"),sQuery(id+"F0.wireOp",EDGE,"E654"),sQuery(id+"F0.wireOp",EDGE,"E655"),sQuery(id+"F0.wireOp",EDGE,"E656"),sQuery(id+"F0.wireOp",EDGE,"E657"),sQuery(id+"F0.wireOp",EDGE,"E658"),sQuery(id+"F0.wireOp",EDGE,"E659"),sQuery(id+"F0.wireOp",EDGE,"E660"),sQuery(id+"F0.wireOp",EDGE,"E661"),sQuery(id+"F0.wireOp",EDGE,"E662"),sQuery(id+"F0.wireOp",EDGE,"E663"),sQuery(id+"F0.wireOp",EDGE,"E664"),sQuery(id+"F0.wireOp",EDGE,"E665"),sQuery(id+"F0.wireOp",EDGE,"E666"),sQuery(id+"F0.wireOp",EDGE,"E667"),sQuery(id+"F0.wireOp",EDGE,"E668"),sQuery(id+"F0.wireOp",EDGE,"E669"),sQuery(id+"F0.wireOp",EDGE,"E670"),sQuery(id+"F0.wireOp",EDGE,"E671"),sQuery(id+"F0.wireOp",EDGE,"E672"),sQuery(id+"F0.wireOp",EDGE,"E673"),sQuery(id+"F0.wireOp",EDGE,"E674"),sQuery(id+"F0.wireOp",EDGE,"E675"),sQuery(id+"F0.wireOp",EDGE,"E676"),sQuery(id+"F0.wireOp",EDGE,"E677"),sQuery(id+"F0.wireOp",EDGE,"E678"),sQuery(id+"F0.wireOp",EDGE,"E679"),sQuery(id+"F0.wireOp",EDGE,"E680"),sQuery(id+"F0.wireOp",EDGE,"E681"),sQuery(id+"F0.wireOp",EDGE,"E682"),sQuery(id+"F0.wireOp",EDGE,"E683"),sQuery(id+"F0.wireOp",EDGE,"E684"),sQuery(id+"F0.wireOp",EDGE,"E685"),sQuery(id+"F0.wireOp",EDGE,"E686"),sQuery(id+"F0.wireOp",EDGE,"E687"),sQuery(id+"F0.wireOp",EDGE,"E688"),sQuery(id+"F0.wireOp",EDGE,"E689"),sQuery(id+"F0.wireOp",EDGE,"E690"),sQuery(id+"F0.wireOp",EDGE,"E691"),sQuery(id+"F0.wireOp",EDGE,"E692"),sQuery(id+"F0.wireOp",EDGE,"E693"),sQuery(id+"F0.wireOp",EDGE,"E694"),sQuery(id+"F0.wireOp",EDGE,"E695"),sQuery(id+"F0.wireOp",EDGE,"E696"),sQuery(id+"F0.wireOp",EDGE,"E697"),sQuery(id+"F0.wireOp",EDGE,"E698"),sQuery(id+"F0.wireOp",EDGE,"E699"),sQuery(id+"F0.wireOp",EDGE,"E700"),sQuery(id+"F0.wireOp",EDGE,"E701"),sQuery(id+"F0.wireOp",EDGE,"E702"),sQuery(id+"F0.wireOp",EDGE,"E703"),sQuery(id+"F0.wireOp",EDGE,"E704"),sQuery(id+"F0.wireOp",EDGE,"E705"),sQuery(id+"F0.wireOp",EDGE,"E706"),sQuery(id+"F0.wireOp",EDGE,"E707"),sQuery(id+"F0.wireOp",EDGE,"E708"),sQuery(id+"F0.wireOp",EDGE,"E709"),sQuery(id+"F0.wireOp",EDGE,"E710"),sQuery(id+"F0.wireOp",EDGE,"E711"),sQuery(id+"F0.wireOp",EDGE,"E712"),sQuery(id+"F0.wireOp",EDGE,"E713"),sQuery(id+"F0.wireOp",EDGE,"E714"),sQuery(id+"F0.wireOp",EDGE,"E715"),sQuery(id+"F0.wireOp",EDGE,"E716"),sQuery(id+"F0.wireOp",EDGE,"E717"),sQuery(id+"F0.wireOp",EDGE,"E718"),sQuery(id+"F0.wireOp",EDGE,"E719"),sQuery(id+"F0.wireOp",EDGE,"E720"),sQuery(id+"F0.wireOp",EDGE,"E721"),sQuery(id+"F0.wireOp",EDGE,"E722"),sQuery(id+"F0.wireOp",EDGE,"E723"),sQuery(id+"F0.wireOp",EDGE,"E724"),sQuery(id+"F0.wireOp",EDGE,"E725"),sQuery(id+"F0.wireOp",EDGE,"E726"),sQuery(id+"F0.wireOp",EDGE,"E727"),sQuery(id+"F0.wireOp",EDGE,"E728"),sQuery(id+"F0.wireOp",EDGE,"E729"),sQuery(id+"F0.wireOp",EDGE,"E730"),sQuery(id+"F0.wireOp",EDGE,"E731"),sQuery(id+"F0.wireOp",EDGE,"E732"),sQuery(id+"F0.wireOp",EDGE,"E733"),sQuery(id+"F0.wireOp",EDGE,"E734"),sQuery(id+"F0.wireOp",EDGE,"E735"),sQuery(id+"F0.wireOp",EDGE,"E736"),sQuery(id+"F0.wireOp",EDGE,"E737"),sQuery(id+"F0.wireOp",EDGE,"E738"),sQuery(id+"F0.wireOp",EDGE,"E739"),sQuery(id+"F0.wireOp",EDGE,"E740"),sQuery(id+"F0.wireOp",EDGE,"E741"),sQuery(id+"F0.wireOp",EDGE,"E742"),sQuery(id+"F0.wireOp",EDGE,"E743"),sQuery(id+"F0.wireOp",EDGE,"E744"),sQuery(id+"F0.wireOp",EDGE,"E745"),sQuery(id+"F0.wireOp",EDGE,"E746"),sQuery(id+"F0.wireOp",EDGE,"E747"),sQuery(id+"F0.wireOp",EDGE,"E748"),sQuery(id+"F0.wireOp",EDGE,"E749"),sQuery(id+"F0.wireOp",EDGE,"E750"),sQuery(id+"F0.wireOp",EDGE,"E751"),sQuery(id+"F0.wireOp",EDGE,"E752"),sQuery(id+"F0.wireOp",EDGE,"E753"),sQuery(id+"F0.wireOp",EDGE,"E754"),sQuery(id+"F0.wireOp",EDGE,"E755"),sQuery(id+"F0.wireOp",EDGE,"E756"),sQuery(id+"F0.wireOp",EDGE,"E757"),sQuery(id+"F0.wireOp",EDGE,"E758"),sQuery(id+"F0.wireOp",EDGE,"E759"),sQuery(id+"F0.wireOp",EDGE,"E760"),sQuery(id+"F0.wireOp",EDGE,"E761"),sQuery(id+"F0.wireOp",EDGE,"E762"),sQuery(id+"F0.wireOp",EDGE,"E763"),sQuery(id+"F0.wireOp",EDGE,"E764"),sQuery(id+"F0.wireOp",EDGE,"E765"),sQuery(id+"F0.wireOp",EDGE,"E766"),sQuery(id+"F0.wireOp",EDGE,"E767"),sQuery(id+"F0.wireOp",EDGE,"E768"),sQuery(id+"F0.wireOp",EDGE,"E769"),sQuery(id+"F0.wireOp",EDGE,"E770"),sQuery(id+"F0.wireOp",EDGE,"E771"),sQuery(id+"F0.wireOp",EDGE,"E772"),sQuery(id+"F0.wireOp",EDGE,"E773"),sQuery(id+"F0.wireOp",EDGE,"E774"),sQuery(id+"F0.wireOp",EDGE,"E775"),sQuery(id+"F0.wireOp",EDGE,"E776"),sQuery(id+"F0.wireOp",EDGE,"E777"),sQuery(id+"F0.wireOp",EDGE,"E778"),sQuery(id+"F0.wireOp",EDGE,"E779"),sQuery(id+"F0.wireOp",EDGE,"E780"),sQuery(id+"F0.wireOp",EDGE,"E781"),sQuery(id+"F0.wireOp",EDGE,"E782"),sQuery(id+"F0.wireOp",EDGE,"E783"),sQuery(id+"F0.wireOp",EDGE,"E784"),sQuery(id+"F0.wireOp",EDGE,"E785"),sQuery(id+"F0.wireOp",EDGE,"E786"),sQuery(id+"F0.wireOp",EDGE,"E787"),sQuery(id+"F0.wireOp",EDGE,"E788"),sQuery(id+"F0.wireOp",EDGE,"E789"),sQuery(id+"F0.wireOp",EDGE,"E790"),sQuery(id+"F0.wireOp",EDGE,"E791"),sQuery(id+"F0.wireOp",EDGE,"E792"),sQuery(id+"F0.wireOp",EDGE,"E793"),sQuery(id+"F0.wireOp",EDGE,"E794"),sQuery(id+"F0.wireOp",EDGE,"E795"),sQuery(id+"F0.wireOp",EDGE,"E796"),sQuery(id+"F0.wireOp",EDGE,"E797"),sQuery(id+"F0.wireOp",EDGE,"E798"),sQuery(id+"F0.wireOp",EDGE,"E799"),sQuery(id+"F0.wireOp",EDGE,"E800"),sQuery(id+"F0.wireOp",EDGE,"E801"),sQuery(id+"F0.wireOp",EDGE,"E802"),sQuery(id+"F0.wireOp",EDGE,"E803"),sQuery(id+"F0.wireOp",EDGE,"E804"),sQuery(id+"F0.wireOp",EDGE,"E805"),sQuery(id+"F0.wireOp",EDGE,"E806"),sQuery(id+"F0.wireOp",EDGE,"E807"),sQuery(id+"F0.wireOp",EDGE,"E808"),sQuery(id+"F0.wireOp",EDGE,"E809"),sQuery(id+"F0.wireOp",EDGE,"E810"),sQuery(id+"F0.wireOp",EDGE,"E811"),sQuery(id+"F0.wireOp",EDGE,"E812"),sQuery(id+"F0.wireOp",EDGE,"E813"),sQuery(id+"F0.wireOp",EDGE,"E814"),sQuery(id+"F0.wireOp",EDGE,"E815"),sQuery(id+"F0.wireOp",EDGE,"E816"),sQuery(id+"F0.wireOp",EDGE,"E817"),sQuery(id+"F0.wireOp",EDGE,"E818"),sQuery(id+"F0.wireOp",EDGE,"E819"),sQuery(id+"F0.wireOp",EDGE,"E820"),sQuery(id+"F0.wireOp",EDGE,"E821"),sQuery(id+"F0.wireOp",EDGE,"E822"),sQuery(id+"F0.wireOp",EDGE,"E823"),sQuery(id+"F0.wireOp",EDGE,"E824"),sQuery(id+"F0.wireOp",EDGE,"E825"),sQuery(id+"F0.wireOp",EDGE,"E826"),sQuery(id+"F0.wireOp",EDGE,"E827"),sQuery(id+"F0.wireOp",EDGE,"E828"),sQuery(id+"F0.wireOp",EDGE,"E829"),sQuery(id+"F0.wireOp",EDGE,"E830"),sQuery(id+"F0.wireOp",EDGE,"E831"),sQuery(id+"F0.wireOp",EDGE,"E832"),sQuery(id+"F0.wireOp",EDGE,"E833"),sQuery(id+"F0.wireOp",EDGE,"E834"),sQuery(id+"F0.wireOp",EDGE,"E835"),sQuery(id+"F0.wireOp",EDGE,"E836"),sQuery(id+"F0.wireOp",EDGE,"E837"),sQuery(id+"F0.wireOp",EDGE,"E838"),sQuery(id+"F0.wireOp",EDGE,"E839"),sQuery(id+"F0.wireOp",EDGE,"E840"),sQuery(id+"F0.wireOp",EDGE,"E841"),sQuery(id+"F0.wireOp",EDGE,"E842"),sQuery(id+"F0.wireOp",EDGE,"E843"),sQuery(id+"F0.wireOp",EDGE,"E844"),sQuery(id+"F0.wireOp",EDGE,"E845"),sQuery(id+"F0.wireOp",EDGE,"E846"),sQuery(id+"F0.wireOp",EDGE,"E847"),sQuery(id+"F0.wireOp",EDGE,"E848"),sQuery(id+"F0.wireOp",EDGE,"E849"),sQuery(id+"F0.wireOp",EDGE,"E850"),sQuery(id+"F0.wireOp",EDGE,"E851"),sQuery(id+"F0.wireOp",EDGE,"E852"),sQuery(id+"F0.wireOp",EDGE,"E853"),sQuery(id+"F0.wireOp",EDGE,"E854"),sQuery(id+"F0.wireOp",EDGE,"E855"),sQuery(id+"F0.wireOp",EDGE,"E856"),sQuery(id+"F0.wireOp",EDGE,"E857"),sQuery(id+"F0.wireOp",EDGE,"E858"),sQuery(id+"F0.wireOp",EDGE,"E859"),sQuery(id+"F0.wireOp",EDGE,"E860"),sQuery(id+"F0.wireOp",EDGE,"E861"),sQuery(id+"F0.wireOp",EDGE,"E862"),sQuery(id+"F0.wireOp",EDGE,"E863"),sQuery(id+"F0.wireOp",EDGE,"E864"),sQuery(id+"F0.wireOp",EDGE,"E865"),sQuery(id+"F0.wireOp",EDGE,"E866"),sQuery(id+"F0.wireOp",EDGE,"E867"),sQuery(id+"F0.wireOp",EDGE,"E868"),sQuery(id+"F0.wireOp",EDGE,"E869"),sQuery(id+"F0.wireOp",EDGE,"E870"),sQuery(id+"F0.wireOp",EDGE,"E871"),sQuery(id+"F0.wireOp",EDGE,"E872"),sQuery(id+"F0.wireOp",EDGE,"E873"),sQuery(id+"F0.wireOp",EDGE,"E874"),sQuery(id+"F0.wireOp",EDGE,"E875"),sQuery(id+"F0.wireOp",EDGE,"E876"),sQuery(id+"F0.wireOp",EDGE,"E877"),sQuery(id+"F0.wireOp",EDGE,"E878"),sQuery(id+"F0.wireOp",EDGE,"E879"),sQuery(id+"F0.wireOp",EDGE,"E880"),sQuery(id+"F0.wireOp",EDGE,"E881"),sQuery(id+"F0.wireOp",EDGE,"E882"),sQuery(id+"F0.wireOp",EDGE,"E883"),sQuery(id+"F0.wireOp",EDGE,"E884"),sQuery(id+"F0.wireOp",EDGE,"E885"),sQuery(id+"F0.wireOp",EDGE,"E886"),sQuery(id+"F0.wireOp",EDGE,"E887"),sQuery(id+"F0.wireOp",EDGE,"E888"),sQuery(id+"F0.wireOp",EDGE,"E889"),sQuery(id+"F0.wireOp",EDGE,"E890"),sQuery(id+"F0.wireOp",EDGE,"E891"),sQuery(id+"F0.wireOp",EDGE,"E892"),sQuery(id+"F0.wireOp",EDGE,"E893"),sQuery(id+"F0.wireOp",EDGE,"E894"),sQuery(id+"F0.wireOp",EDGE,"E895"),sQuery(id+"F0.wireOp",EDGE,"E896"),sQuery(id+"F0.wireOp",EDGE,"E897"),sQuery(id+"F0.wireOp",EDGE,"E898"),sQuery(id+"F0.wireOp",EDGE,"E899"),sQuery(id+"F0.wireOp",EDGE,"E900"),sQuery(id+"F0.wireOp",EDGE,"E901"),sQuery(id+"F0.wireOp",EDGE,"E902"),sQuery(id+"F0.wireOp",EDGE,"E903"),sQuery(id+"F0.wireOp",EDGE,"E904"),sQuery(id+"F0.wireOp",EDGE,"E905"),sQuery(id+"F0.wireOp",EDGE,"E906"),sQuery(id+"F0.wireOp",EDGE,"E907"),sQuery(id+"F0.wireOp",EDGE,"E908"),sQuery(id+"F0.wireOp",EDGE,"E909"),sQuery(id+"F0.wireOp",EDGE,"E910"),sQuery(id+"F0.wireOp",EDGE,"E911"),sQuery(id+"F0.wireOp",EDGE,"E912"),sQuery(id+"F0.wireOp",EDGE,"E913"),sQuery(id+"F0.wireOp",EDGE,"E914"),sQuery(id+"F0.wireOp",EDGE,"E915"),sQuery(id+"F0.wireOp",EDGE,"E916"),sQuery(id+"F0.wireOp",EDGE,"E917"),sQuery(id+"F0.wireOp",EDGE,"E918"),sQuery(id+"F0.wireOp",EDGE,"E919"),sQuery(id+"F0.wireOp",EDGE,"E920"),sQuery(id+"F0.wireOp",EDGE,"E921"),sQuery(id+"F0.wireOp",EDGE,"E922"),sQuery(id+"F0.wireOp",EDGE,"E923"),sQuery(id+"F0.wireOp",EDGE,"E924"),sQuery(id+"F0.wireOp",EDGE,"E925"),sQuery(id+"F0.wireOp",EDGE,"E926"),sQuery(id+"F0.wireOp",EDGE,"E927"),sQuery(id+"F0.wireOp",EDGE,"E928"),sQuery(id+"F0.wireOp",EDGE,"E929"),sQuery(id+"F0.wireOp",EDGE,"E930"),sQuery(id+"F0.wireOp",EDGE,"E931"),sQuery(id+"F0.wireOp",EDGE,"E932"),sQuery(id+"F0.wireOp",EDGE,"E933"),sQuery(id+"F0.wireOp",EDGE,"E934"),sQuery(id+"F0.wireOp",EDGE,"E935"),sQuery(id+"F0.wireOp",EDGE,"E936"),sQuery(id+"F0.wireOp",EDGE,"E937"),sQuery(id+"F0.wireOp",EDGE,"E938"),sQuery(id+"F0.wireOp",EDGE,"E939"),sQuery(id+"F0.wireOp",EDGE,"E940"),sQuery(id+"F0.wireOp",EDGE,"E941"),sQuery(id+"F0.wireOp",EDGE,"E942"),sQuery(id+"F0.wireOp",EDGE,"E943"),sQuery(id+"F0.wireOp",EDGE,"E944"),sQuery(id+"F0.wireOp",EDGE,"E945"),sQuery(id+"F0.wireOp",EDGE,"E946"),sQuery(id+"F0.wireOp",EDGE,"E947"),sQuery(id+"F0.wireOp",EDGE,"E948"),sQuery(id+"F0.wireOp",EDGE,"E949"),sQuery(id+"F0.wireOp",EDGE,"E950"),sQuery(id+"F0.wireOp",EDGE,"E951"),sQuery(id+"F0.wireOp",EDGE,"E952"),sQuery(id+"F0.wireOp",EDGE,"E953"),sQuery(id+"F0.wireOp",EDGE,"E954"),sQuery(id+"F0.wireOp",EDGE,"E955"),sQuery(id+"F0.wireOp",EDGE,"E956"),sQuery(id+"F0.wireOp",EDGE,"E957"),sQuery(id+"F0.wireOp",EDGE,"E958"),sQuery(id+"F0.wireOp",EDGE,"E959"),sQuery(id+"F0.wireOp",EDGE,"E960"),sQuery(id+"F0.wireOp",EDGE,"E961"),sQuery(id+"F0.wireOp",EDGE,"E962"),sQuery(id+"F0.wireOp",EDGE,"E963"),sQuery(id+"F0.wireOp",EDGE,"E964"),sQuery(id+"F0.wireOp",EDGE,"E965"),sQuery(id+"F0.wireOp",EDGE,"E966"),sQuery(id+"F0.wireOp",EDGE,"E967"),sQuery(id+"F0.wireOp",EDGE,"E968"),sQuery(id+"F0.wireOp",EDGE,"E969"),sQuery(id+"F0.wireOp",EDGE,"E970"),sQuery(id+"F0.wireOp",EDGE,"E971"),sQuery(id+"F0.wireOp",EDGE,"E972"),sQuery(id+"F0.wireOp",EDGE,"E973"),sQuery(id+"F0.wireOp",EDGE,"E974"),sQuery(id+"F0.wireOp",EDGE,"E975"),sQuery(id+"F0.wireOp",EDGE,"E976"),sQuery(id+"F0.wireOp",EDGE,"E977"),sQuery(id+"F0.wireOp",EDGE,"E978"),sQuery(id+"F0.wireOp",EDGE,"E979"),sQuery(id+"F0.wireOp",EDGE,"E980"),sQuery(id+"F0.wireOp",EDGE,"E981"),sQuery(id+"F0.wireOp",EDGE,"E982"),sQuery(id+"F0.wireOp",EDGE,"E983"),sQuery(id+"F0.wireOp",EDGE,"E984"),sQuery(id+"F0.wireOp",EDGE,"E985"),sQuery(id+"F0.wireOp",EDGE,"E986"),sQuery(id+"F0.wireOp",EDGE,"E987"),sQuery(id+"F0.wireOp",EDGE,"E988"),sQuery(id+"F0.wireOp",EDGE,"E989"),sQuery(id+"F0.wireOp",EDGE,"E990"),sQuery(id+"F0.wireOp",EDGE,"E991"),sQuery(id+"F0.wireOp",EDGE,"E992"),sQuery(id+"F0.wireOp",EDGE,"E993"),sQuery(id+"F0.wireOp",EDGE,"E994"),sQuery(id+"F0.wireOp",EDGE,"E995"),sQuery(id+"F0.wireOp",EDGE,"E996"),sQuery(id+"F0.wireOp",EDGE,"E997"),sQuery(id+"F0.wireOp",EDGE,"E998"),sQuery(id+"F0.wireOp",EDGE,"E999"),sQuery(id+"F0.wireOp",EDGE,"E1000"),sQuery(id+"F0.wireOp",EDGE,"E1001"),sQuery(id+"F0.wireOp",EDGE,"E1002"),sQuery(id+"F0.wireOp",EDGE,"E1003"),sQuery(id+"F0.wireOp",EDGE,"E1004"),sQuery(id+"F0.wireOp",EDGE,"E1005"),sQuery(id+"F0.wireOp",EDGE,"E1006"),sQuery(id+"F0.wireOp",EDGE,"E1007"),sQuery(id+"F0.wireOp",EDGE,"E1008"),sQuery(id+"F0.wireOp",EDGE,"E1009"),sQuery(id+"F0.wireOp",EDGE,"E1010"),sQuery(id+"F0.wireOp",EDGE,"E1011"),sQuery(id+"F0.wireOp",EDGE,"E1012"),sQuery(id+"F0.wireOp",EDGE,"E1013"),sQuery(id+"F0.wireOp",EDGE,"E1014"),sQuery(id+"F0.wireOp",EDGE,"E1015"),sQuery(id+"F0.wireOp",EDGE,"E1016"),sQuery(id+"F0.wireOp",EDGE,"E1017"),sQuery(id+"F0.wireOp",EDGE,"E1018"),sQuery(id+"F0.wireOp",EDGE,"E1019"),sQuery(id+"F0.wireOp",EDGE,"E1020"),sQuery(id+"F0.wireOp",EDGE,"E1021"),sQuery(id+"F0.wireOp",EDGE,"E1022"),sQuery(id+"F0.wireOp",EDGE,"E1023"),sQuery(id+"F0.wireOp",EDGE,"E1024"),sQuery(id+"F0.wireOp",EDGE,"E1025"),sQuery(id+"F0.wireOp",EDGE,"E1026"),sQuery(id+"F0.wireOp",EDGE,"E1027"),sQuery(id+"F0.wireOp",EDGE,"E1028"),sQuery(id+"F0.wireOp",EDGE,"E1029"),sQuery(id+"F0.wireOp",EDGE,"E1030"),sQuery(id+"F0.wireOp",EDGE,"E1031"),sQuery(id+"F0.wireOp",EDGE,"E1032"),sQuery(id+"F0.wireOp",EDGE,"E1033"),sQuery(id+"F0.wireOp",EDGE,"E1034"),sQuery(id+"F0.wireOp",EDGE,"E1035"),sQuery(id+"F0.wireOp",EDGE,"E1036"),sQuery(id+"F0.wireOp",EDGE,"E1037"),sQuery(id+"F0.wireOp",EDGE,"E1038"),sQuery(id+"F0.wireOp",EDGE,"E1039"),sQuery(id+"F0.wireOp",EDGE,"E1040"),sQuery(id+"F0.wireOp",EDGE,"E1041"),sQuery(id+"F0.wireOp",EDGE,"E1042"),sQuery(id+"F0.wireOp",EDGE,"E1043"),sQuery(id+"F0.wireOp",EDGE,"E1044"),sQuery(id+"F0.wireOp",EDGE,"E1045"),sQuery(id+"F0.wireOp",EDGE,"E1046"),sQuery(id+"F0.wireOp",EDGE,"E1047"),sQuery(id+"F0.wireOp",EDGE,"E1048"),sQuery(id+"F0.wireOp",EDGE,"E1049"),sQuery(id+"F0.wireOp",EDGE,"E1050"),sQuery(id+"F0.wireOp",EDGE,"E1051"),sQuery(id+"F0.wireOp",EDGE,"E1052"),sQuery(id+"F0.wireOp",EDGE,"E1053"),sQuery(id+"F0.wireOp",EDGE,"E1054"),sQuery(id+"F0.wireOp",EDGE,"E1055"),sQuery(id+"F0.wireOp",EDGE,"E1056"),sQuery(id+"F0.wireOp",EDGE,"E1057"),sQuery(id+"F0.wireOp",EDGE,"E1058"),sQuery(id+"F0.wireOp",EDGE,"E1059"),sQuery(id+"F0.wireOp",EDGE,"E1060"),sQuery(id+"F0.wireOp",EDGE,"E1061"),sQuery(id+"F0.wireOp",EDGE,"E1062"),sQuery(id+"F0.wireOp",EDGE,"E1063"),sQuery(id+"F0.wireOp",EDGE,"E1064"),sQuery(id+"F0.wireOp",EDGE,"E1065"),sQuery(id+"F0.wireOp",EDGE,"E1066"),sQuery(id+"F0.wireOp",EDGE,"E1067"),sQuery(id+"F0.wireOp",EDGE,"E1068"),sQuery(id+"F0.wireOp",EDGE,"E1069"),sQuery(id+"F0.wireOp",EDGE,"E1070"),sQuery(id+"F0.wireOp",EDGE,"E1071"),sQuery(id+"F0.wireOp",EDGE,"E1072"),sQuery(id+"F0.wireOp",EDGE,"E1073"),sQuery(id+"F0.wireOp",EDGE,"E1074"),sQuery(id+"F0.wireOp",EDGE,"E1075"),sQuery(id+"F0.wireOp",EDGE,"E1076"),sQuery(id+"F0.wireOp",EDGE,"E1077"),sQuery(id+"F0.wireOp",EDGE,"E1078"),sQuery(id+"F0.wireOp",EDGE,"E1079"),sQuery(id+"F0.wireOp",EDGE,"E1080"),sQuery(id+"F0.wireOp",EDGE,"E1081"),sQuery(id+"F0.wireOp",EDGE,"E1082"),sQuery(id+"F0.wireOp",EDGE,"E1083"),sQuery(id+"F0.wireOp",EDGE,"E1084"),sQuery(id+"F0.wireOp",EDGE,"E1085"),sQuery(id+"F0.wireOp",EDGE,"E1086"),sQuery(id+"F0.wireOp",EDGE,"E1087"),sQuery(id+"F0.wireOp",EDGE,"E1088"),sQuery(id+"F0.wireOp",EDGE,"E1089"),sQuery(id+"F0.wireOp",EDGE,"E1090"),sQuery(id+"F0.wireOp",EDGE,"E1091"),sQuery(id+"F0.wireOp",EDGE,"E1092"),sQuery(id+"F0.wireOp",EDGE,"E1093"),sQuery(id+"F0.wireOp",EDGE,"E1094"),sQuery(id+"F0.wireOp",EDGE,"E1095"),sQuery(id+"F0.wireOp",EDGE,"E1096"),sQuery(id+"F0.wireOp",EDGE,"E1097"),sQuery(id+"F0.wireOp",EDGE,"E1098"),sQuery(id+"F0.wireOp",EDGE,"E1099"),sQuery(id+"F0.wireOp",EDGE,"E1100"),sQuery(id+"F0.wireOp",EDGE,"E1101"),sQuery(id+"F0.wireOp",EDGE,"E1102"),sQuery(id+"F0.wireOp",EDGE,"E1103"),sQuery(id+"F0.wireOp",EDGE,"E1104"),sQuery(id+"F0.wireOp",EDGE,"E1105"),sQuery(id+"F0.wireOp",EDGE,"E1106"),sQuery(id+"F0.wireOp",EDGE,"E1107"),sQuery(id+"F0.wireOp",EDGE,"E1108"),sQuery(id+"F0.wireOp",EDGE,"E1109"),sQuery(id+"F0.wireOp",EDGE,"E1110"),sQuery(id+"F0.wireOp",EDGE,"E1111"),sQuery(id+"F0.wireOp",EDGE,"E1112"),sQuery(id+"F0.wireOp",EDGE,"E1113"),sQuery(id+"F0.wireOp",EDGE,"E1114"),sQuery(id+"F0.wireOp",EDGE,"E1115"),sQuery(id+"F0.wireOp",EDGE,"E1116"),sQuery(id+"F0.wireOp",EDGE,"E1117"),sQuery(id+"F0.wireOp",EDGE,"E1118"),sQuery(id+"F0.wireOp",EDGE,"E1119"),sQuery(id+"F0.wireOp",EDGE,"E1120"),sQuery(id+"F0.wireOp",EDGE,"E1121"),sQuery(id+"F0.wireOp",EDGE,"E1122"),sQuery(id+"F0.wireOp",EDGE,"E1123"),sQuery(id+"F0.wireOp",EDGE,"E1124"),sQuery(id+"F0.wireOp",EDGE,"E1125"),sQuery(id+"F0.wireOp",EDGE,"E1126"),sQuery(id+"F0.wireOp",EDGE,"E1127"),sQuery(id+"F0.wireOp",EDGE,"E1128"),sQuery(id+"F0.wireOp",EDGE,"E1129"),sQuery(id+"F0.wireOp",EDGE,"E1130"),sQuery(id+"F0.wireOp",EDGE,"E1131"),sQuery(id+"F0.wireOp",EDGE,"E1132"),sQuery(id+"F0.wireOp",EDGE,"E1133"),sQuery(id+"F0.wireOp",EDGE,"E1134"),sQuery(id+"F0.wireOp",EDGE,"E1135"),sQuery(id+"F0.wireOp",EDGE,"E1136"),sQuery(id+"F0.wireOp",EDGE,"E1137"),sQuery(id+"F0.wireOp",EDGE,"E1138"),sQuery(id+"F0.wireOp",EDGE,"E1139"),sQuery(id+"F0.wireOp",EDGE,"E1140"),sQuery(id+"F0.wireOp",EDGE,"E1141"),sQuery(id+"F0.wireOp",EDGE,"E1142"),sQuery(id+"F0.wireOp",EDGE,"E1143"),sQuery(id+"F0.wireOp",EDGE,"E1144"),sQuery(id+"F0.wireOp",EDGE,"E1145"),sQuery(id+"F0.wireOp",EDGE,"E1146"),sQuery(id+"F0.wireOp",EDGE,"E1147"),sQuery(id+"F0.wireOp",EDGE,"E1148"),sQuery(id+"F0.wireOp",EDGE,"E1149"),sQuery(id+"F0.wireOp",EDGE,"E1150"),sQuery(id+"F0.wireOp",EDGE,"E1151"),sQuery(id+"F0.wireOp",EDGE,"E1152"),sQuery(id+"F0.wireOp",EDGE,"E1153"),sQuery(id+"F0.wireOp",EDGE,"E1154"),sQuery(id+"F0.wireOp",EDGE,"E1155"),sQuery(id+"F0.wireOp",EDGE,"E1156"),sQuery(id+"F0.wireOp",EDGE,"E1157"),sQuery(id+"F0.wireOp",EDGE,"E1158"),sQuery(id+"F0.wireOp",EDGE,"E1159"),sQuery(id+"F0.wireOp",EDGE,"E1160"),sQuery(id+"F0.wireOp",EDGE,"E1161"),sQuery(id+"F0.wireOp",EDGE,"E1162"),sQuery(id+"F0.wireOp",EDGE,"E1163"),sQuery(id+"F0.wireOp",EDGE,"E1164"),sQuery(id+"F0.wireOp",EDGE,"E1165"),sQuery(id+"F0.wireOp",EDGE,"E1166"),sQuery(id+"F0.wireOp",EDGE,"E1167"),sQuery(id+"F0.wireOp",EDGE,"E1168"),sQuery(id+"F0.wireOp",EDGE,"E1169"),sQuery(id+"F0.wireOp",EDGE,"E1170"),sQuery(id+"F0.wireOp",EDGE,"E1171"),sQuery(id+"F0.wireOp",EDGE,"E1172"),sQuery(id+"F0.wireOp",EDGE,"E1173"),sQuery(id+"F0.wireOp",EDGE,"E1174"),sQuery(id+"F0.wireOp",EDGE,"E1175"),sQuery(id+"F0.wireOp",EDGE,"E1176"),sQuery(id+"F0.wireOp",EDGE,"E1177"),sQuery(id+"F0.wireOp",EDGE,"E1178"),sQuery(id+"F0.wireOp",EDGE,"E1179"),sQuery(id+"F0.wireOp",EDGE,"E1180"),sQuery(id+"F0.wireOp",EDGE,"E1181"),sQuery(id+"F0.wireOp",EDGE,"E1182"),sQuery(id+"F0.wireOp",EDGE,"E1183"),sQuery(id+"F0.wireOp",EDGE,"E1184"),sQuery(id+"F0.wireOp",EDGE,"E1185"),sQuery(id+"F0.wireOp",EDGE,"E1186"),sQuery(id+"F0.wireOp",EDGE,"E1187"),sQuery(id+"F0.wireOp",EDGE,"E1188"),sQuery(id+"F0.wireOp",EDGE,"E1189"),sQuery(id+"F0.wireOp",EDGE,"E1190"),sQuery(id+"F0.wireOp",EDGE,"E1191"),sQuery(id+"F0.wireOp",EDGE,"E1192"),sQuery(id+"F0.wireOp",EDGE,"E1193"),sQuery(id+"F0.wireOp",EDGE,"E1194"),sQuery(id+"F0.wireOp",EDGE,"E1195"),sQuery(id+"F0.wireOp",EDGE,"E1196"),sQuery(id+"F0.wireOp",EDGE,"E1197"),sQuery(id+"F0.wireOp",EDGE,"E1198"),sQuery(id+"F0.wireOp",EDGE,"E1199"),sQuery(id+"F0.wireOp",EDGE,"E1200"),sQuery(id+"F0.wireOp",EDGE,"E1201"),sQuery(id+"F0.wireOp",EDGE,"E1202"),sQuery(id+"F0.wireOp",EDGE,"E1203"),sQuery(id+"F0.wireOp",EDGE,"E1204"),sQuery(id+"F0.wireOp",EDGE,"E1205"),sQuery(id+"F0.wireOp",EDGE,"E1206"),sQuery(id+"F0.wireOp",EDGE,"E1207"),sQuery(id+"F0.wireOp",EDGE,"E1208"),sQuery(id+"F0.wireOp",EDGE,"E1209"),sQuery(id+"F0.wireOp",EDGE,"E1210"),sQuery(id+"F0.wireOp",EDGE,"E1211"),sQuery(id+"F0.wireOp",EDGE,"E1212"),sQuery(id+"F0.wireOp",EDGE,"E1213"),sQuery(id+"F0.wireOp",EDGE,"E1214"),sQuery(id+"F0.wireOp",EDGE,"E1215"),sQuery(id+"F0.wireOp",EDGE,"E1216"),sQuery(id+"F0.wireOp",EDGE,"E1217"),sQuery(id+"F0.wireOp",EDGE,"E1218"),sQuery(id+"F0.wireOp",EDGE,"E1219"),sQuery(id+"F0.wireOp",EDGE,"E1220"),sQuery(id+"F0.wireOp",EDGE,"E1221"),sQuery(id+"F0.wireOp",EDGE,"E1222"),sQuery(id+"F0.wireOp",EDGE,"E1223"),sQuery(id+"F0.wireOp",EDGE,"E1224"),sQuery(id+"F0.wireOp",EDGE,"E1225"),sQuery(id+"F0.wireOp",EDGE,"E1226"),sQuery(id+"F0.wireOp",EDGE,"E1227"),sQuery(id+"F0.wireOp",EDGE,"E1228"),sQuery(id+"F0.wireOp",EDGE,"E1229"),sQuery(id+"F0.wireOp",EDGE,"E1230"),sQuery(id+"F0.wireOp",EDGE,"E1231"),sQuery(id+"F0.wireOp",EDGE,"E1232"),sQuery(id+"F0.wireOp",EDGE,"E1233"),sQuery(id+"F0.wireOp",EDGE,"E1234"),sQuery(id+"F0.wireOp",EDGE,"E1235"),sQuery(id+"F0.wireOp",EDGE,"E1236"),sQuery(id+"F0.wireOp",EDGE,"E1237"),sQuery(id+"F0.wireOp",EDGE,"E1238"),sQuery(id+"F0.wireOp",EDGE,"E1239"),sQuery(id+"F0.wireOp",EDGE,"E1240"),sQuery(id+"F0.wireOp",EDGE,"E1241"),sQuery(id+"F0.wireOp",EDGE,"E1242"),sQuery(id+"F0.wireOp",EDGE,"E1243"),sQuery(id+"F0.wireOp",EDGE,"E1244"),sQuery(id+"F0.wireOp",EDGE,"E1245"),sQuery(id+"F0.wireOp",EDGE,"E1246"),sQuery(id+"F0.wireOp",EDGE,"E1247"),sQuery(id+"F0.wireOp",EDGE,"E1248"),sQuery(id+"F0.wireOp",EDGE,"E1249"),sQuery(id+"F0.wireOp",EDGE,"E1250"),sQuery(id+"F0.wireOp",EDGE,"E1251"),sQuery(id+"F0.wireOp",EDGE,"E1252"),sQuery(id+"F0.wireOp",EDGE,"E1253"),sQuery(id+"F0.wireOp",EDGE,"E1254"),sQuery(id+"F0.wireOp",EDGE,"E1255"),sQuery(id+"F0.wireOp",EDGE,"E1256"),sQuery(id+"F0.wireOp",EDGE,"E1257"),sQuery(id+"F0.wireOp",EDGE,"E1258"),sQuery(id+"F0.wireOp",EDGE,"E1259"),sQuery(id+"F0.wireOp",EDGE,"E1260"),sQuery(id+"F0.wireOp",EDGE,"E1261"),sQuery(id+"F0.wireOp",EDGE,"E1262"),sQuery(id+"F0.wireOp",EDGE,"E1263"),sQuery(id+"F0.wireOp",EDGE,"E1264"),sQuery(id+"F0.wireOp",EDGE,"E1265"),sQuery(id+"F0.wireOp",EDGE,"E1266"),sQuery(id+"F0.wireOp",EDGE,"E1267"),sQuery(id+"F0.wireOp",EDGE,"E1268"),sQuery(id+"F0.wireOp",EDGE,"E1269"),sQuery(id+"F0.wireOp",EDGE,"E1270"),sQuery(id+"F0.wireOp",EDGE,"E1271"),sQuery(id+"F0.wireOp",EDGE,"E1272"),sQuery(id+"F0.wireOp",EDGE,"E1273"),sQuery(id+"F0.wireOp",EDGE,"E1274"),sQuery(id+"F0.wireOp",EDGE,"E1275"),sQuery(id+"F0.wireOp",EDGE,"E1276"),sQuery(id+"F0.wireOp",EDGE,"E1277"),sQuery(id+"F0.wireOp",EDGE,"E1278"),sQuery(id+"F0.wireOp",EDGE,"E1279"),sQuery(id+"F0.wireOp",EDGE,"E1280"),sQuery(id+"F0.wireOp",EDGE,"E1281"),sQuery(id+"F0.wireOp",EDGE,"E1282"),sQuery(id+"F0.wireOp",EDGE,"E1283"),sQuery(id+"F0.wireOp",EDGE,"E1284"),sQuery(id+"F0.wireOp",EDGE,"E1285"),sQuery(id+"F0.wireOp",EDGE,"E1286"),sQuery(id+"F0.wireOp",EDGE,"E1287"),sQuery(id+"F0.wireOp",EDGE,"E1288"),sQuery(id+"F0.wireOp",EDGE,"E1289"),sQuery(id+"F0.wireOp",EDGE,"E1290"),sQuery(id+"F0.wireOp",EDGE,"E1291"),sQuery(id+"F0.wireOp",EDGE,"E1292"),sQuery(id+"F0.wireOp",EDGE,"E1293"),sQuery(id+"F0.wireOp",EDGE,"E1294"),sQuery(id+"F0.wireOp",EDGE,"E1295"),sQuery(id+"F0.wireOp",EDGE,"E1296"),sQuery(id+"F0.wireOp",EDGE,"E1297"),sQuery(id+"F0.wireOp",EDGE,"E1298"),sQuery(id+"F0.wireOp",EDGE,"E1299"),sQuery(id+"F0.wireOp",EDGE,"E1300"),sQuery(id+"F0.wireOp",EDGE,"E1301"),sQuery(id+"F0.wireOp",EDGE,"E1302"),sQuery(id+"F0.wireOp",EDGE,"E1303"),sQuery(id+"F0.wireOp",EDGE,"E1304"),sQuery(id+"F0.wireOp",EDGE,"E1305"),sQuery(id+"F0.wireOp",EDGE,"E1306"),sQuery(id+"F0.wireOp",EDGE,"E1307"),sQuery(id+"F0.wireOp",EDGE,"E1308"),sQuery(id+"F0.wireOp",EDGE,"E1309"),sQuery(id+"F0.wireOp",EDGE,"E1310"),sQuery(id+"F0.wireOp",EDGE,"E1311"),sQuery(id+"F0.wireOp",EDGE,"E1312"),sQuery(id+"F0.wireOp",EDGE,"E1313"),sQuery(id+"F0.wireOp",EDGE,"E1314"),sQuery(id+"F0.wireOp",EDGE,"E1315"),sQuery(id+"F0.wireOp",EDGE,"E1316"),sQuery(id+"F0.wireOp",EDGE,"E1317"),sQuery(id+"F0.wireOp",EDGE,"E1318"),sQuery(id+"F0.wireOp",EDGE,"E1319"),sQuery(id+"F0.wireOp",EDGE,"E1320"),sQuery(id+"F0.wireOp",EDGE,"E1321"),sQuery(id+"F0.wireOp",EDGE,"E1322"),sQuery(id+"F0.wireOp",EDGE,"E1323"),sQuery(id+"F0.wireOp",EDGE,"E1324"),sQuery(id+"F0.wireOp",EDGE,"E1325"),sQuery(id+"F0.wireOp",EDGE,"E1326"),sQuery(id+"F0.wireOp",EDGE,"E1327"),sQuery(id+"F0.wireOp",EDGE,"E1328"),sQuery(id+"F0.wireOp",EDGE,"E1329"),sQuery(id+"F0.wireOp",EDGE,"E1330"),sQuery(id+"F0.wireOp",EDGE,"E1331"),sQuery(id+"F0.wireOp",EDGE,"E1332"),sQuery(id+"F0.wireOp",EDGE,"E1333"),sQuery(id+"F0.wireOp",EDGE,"E1334"),sQuery(id+"F0.wireOp",EDGE,"E1335"),sQuery(id+"F0.wireOp",EDGE,"E1336"),sQuery(id+"F0.wireOp",EDGE,"E1337"),sQuery(id+"F0.wireOp",EDGE,"E1338"),sQuery(id+"F0.wireOp",EDGE,"E1339"),sQuery(id+"F0.wireOp",EDGE,"E1340"),sQuery(id+"F0.wireOp",EDGE,"E1341"),sQuery(id+"F0.wireOp",EDGE,"E1342"),sQuery(id+"F0.wireOp",EDGE,"E1343"),sQuery(id+"F0.wireOp",EDGE,"E1344"),sQuery(id+"F0.wireOp",EDGE,"E1345"),sQuery(id+"F0.wireOp",EDGE,"E1346"),sQuery(id+"F0.wireOp",EDGE,"E1347"),sQuery(id+"F0.wireOp",EDGE,"E1348"),sQuery(id+"F0.wireOp",EDGE,"E1349"),sQuery(id+"F0.wireOp",EDGE,"E1350"),sQuery(id+"F0.wireOp",EDGE,"E1351"),sQuery(id+"F0.wireOp",EDGE,"E1352"),sQuery(id+"F0.wireOp",EDGE,"E1353"),sQuery(id+"F0.wireOp",EDGE,"E1354"),sQuery(id+"F0.wireOp",EDGE,"E1355"),sQuery(id+"F0.wireOp",EDGE,"E1356"),sQuery(id+"F0.wireOp",EDGE,"E1357"),sQuery(id+"F0.wireOp",EDGE,"E1358"),sQuery(id+"F0.wireOp",EDGE,"E1359"),sQuery(id+"F0.wireOp",EDGE,"E1360"),sQuery(id+"F0.wireOp",EDGE,"E1361"),sQuery(id+"F0.wireOp",EDGE,"E1362"),sQuery(id+"F0.wireOp",EDGE,"E1363"),sQuery(id+"F0.wireOp",EDGE,"E1364"),sQuery(id+"F0.wireOp",EDGE,"E1365"),sQuery(id+"F0.wireOp",EDGE,"E1366"),sQuery(id+"F0.wireOp",EDGE,"E1367"),sQuery(id+"F0.wireOp",EDGE,"E1368"),sQuery(id+"F0.wireOp",EDGE,"E1369"),sQuery(id+"F0.wireOp",EDGE,"E1370"),sQuery(id+"F0.wireOp",EDGE,"E1371"),sQuery(id+"F0.wireOp",EDGE,"E1372"),sQuery(id+"F0.wireOp",EDGE,"E1373"),sQuery(id+"F0.wireOp",EDGE,"E1374"),sQuery(id+"F0.wireOp",EDGE,"E1375"),sQuery(id+"F0.wireOp",EDGE,"E1376"),sQuery(id+"F0.wireOp",EDGE,"E1377"),sQuery(id+"F0.wireOp",EDGE,"E1378"),sQuery(id+"F0.wireOp",EDGE,"E1379"),sQuery(id+"F0.wireOp",EDGE,"E1380"),sQuery(id+"F0.wireOp",EDGE,"E1381"),sQuery(id+"F0.wireOp",EDGE,"E1382"),sQuery(id+"F0.wireOp",EDGE,"E1383"),sQuery(id+"F0.wireOp",EDGE,"E1384"),sQuery(id+"F0.wireOp",EDGE,"E1385"),sQuery(id+"F0.wireOp",EDGE,"E1386"),sQuery(id+"F0.wireOp",EDGE,"E1387"),sQuery(id+"F0.wireOp",EDGE,"E1388"),sQuery(id+"F0.wireOp",EDGE,"E1389"),sQuery(id+"F0.wireOp",EDGE,"E1390"),sQuery(id+"F0.wireOp",EDGE,"E1391"),sQuery(id+"F0.wireOp",EDGE,"E1392"),sQuery(id+"F0.wireOp",EDGE,"E1393"),sQuery(id+"F0.wireOp",EDGE,"E1394"),sQuery(id+"F0.wireOp",EDGE,"E1395"),sQuery(id+"F0.wireOp",EDGE,"E1396"),sQuery(id+"F0.wireOp",EDGE,"E1397"),sQuery(id+"F0.wireOp",EDGE,"E1398"),sQuery(id+"F0.wireOp",EDGE,"E1399"),sQuery(id+"F0.wireOp",EDGE,"E1400"),sQuery(id+"F0.wireOp",EDGE,"E1401"),sQuery(id+"F0.wireOp",EDGE,"E1402"),sQuery(id+"F0.wireOp",EDGE,"E1403"),sQuery(id+"F0.wireOp",EDGE,"E1404"),sQuery(id+"F0.wireOp",EDGE,"E1405"),sQuery(id+"F0.wireOp",EDGE,"E1406"),sQuery(id+"F0.wireOp",EDGE,"E1407"),sQuery(id+"F0.wireOp",EDGE,"E1408"),sQuery(id+"F0.wireOp",EDGE,"E1409"),sQuery(id+"F0.wireOp",EDGE,"E1410"),sQuery(id+"F0.wireOp",EDGE,"E1411"),sQuery(id+"F0.wireOp",EDGE,"E1412"),sQuery(id+"F0.wireOp",EDGE,"E1413"),sQuery(id+"F0.wireOp",EDGE,"E1414"),sQuery(id+"F0.wireOp",EDGE,"E1415"),sQuery(id+"F0.wireOp",EDGE,"E1416"),sQuery(id+"F0.wireOp",EDGE,"E1417"),sQuery(id+"F0.wireOp",EDGE,"E1418"),sQuery(id+"F0.wireOp",EDGE,"E1419"),sQuery(id+"F0.wireOp",EDGE,"E1420"),sQuery(id+"F0.wireOp",EDGE,"E1421"),sQuery(id+"F0.wireOp",EDGE,"E1422"),sQuery(id+"F0.wireOp",EDGE,"E1423"),sQuery(id+"F0.wireOp",EDGE,"E1424"),sQuery(id+"F0.wireOp",EDGE,"E1425"),sQuery(id+"F0.wireOp",EDGE,"E1426"),sQuery(id+"F0.wireOp",EDGE,"E1427"),sQuery(id+"F0.wireOp",EDGE,"E1428"),sQuery(id+"F0.wireOp",EDGE,"E1429"),sQuery(id+"F0.wireOp",EDGE,"E1430"),sQuery(id+"F0.wireOp",EDGE,"E1431"),sQuery(id+"F0.wireOp",EDGE,"E1432"),sQuery(id+"F0.wireOp",EDGE,"E1433"),sQuery(id+"F0.wireOp",EDGE,"E1434"),sQuery(id+"F0.wireOp",EDGE,"E1435"),sQuery(id+"F0.wireOp",EDGE,"E1436"),sQuery(id+"F0.wireOp",EDGE,"E1437"),sQuery(id+"F0.wireOp",EDGE,"E1438"),sQuery(id+"F0.wireOp",EDGE,"E1439"),sQuery(id+"F0.wireOp",EDGE,"E1440"),sQuery(id+"F0.wireOp",EDGE,"E1441"),sQuery(id+"F0.wireOp",EDGE,"E1442"),sQuery(id+"F0.wireOp",EDGE,"E1443"),sQuery(id+"F0.wireOp",EDGE,"E1444"),sQuery(id+"F0.wireOp",EDGE,"E1445"),sQuery(id+"F0.wireOp",EDGE,"E1446"),sQuery(id+"F0.wireOp",EDGE,"E1447"),sQuery(id+"F0.wireOp",EDGE,"E1448"),sQuery(id+"F0.wireOp",EDGE,"E1449"),sQuery(id+"F0.wireOp",EDGE,"E1450"),sQuery(id+"F0.wireOp",EDGE,"E1451"),sQuery(id+"F0.wireOp",EDGE,"E1452"),sQuery(id+"F0.wireOp",EDGE,"E1453"),sQuery(id+"F0.wireOp",EDGE,"E1454"),sQuery(id+"F0.wireOp",EDGE,"E1455"),sQuery(id+"F0.wireOp",EDGE,"E1456"),sQuery(id+"F0.wireOp",EDGE,"E1457"),sQuery(id+"F0.wireOp",EDGE,"E1458"),sQuery(id+"F0.wireOp",EDGE,"E1459"),sQuery(id+"F0.wireOp",EDGE,"E1460"),sQuery(id+"F0.wireOp",EDGE,"E1461"),sQuery(id+"F0.wireOp",EDGE,"E1462"),sQuery(id+"F0.wireOp",EDGE,"E1463"),sQuery(id+"F0.wireOp",EDGE,"E1464"),sQuery(id+"F0.wireOp",EDGE,"E1465"),sQuery(id+"F0.wireOp",EDGE,"E1466"),sQuery(id+"F0.wireOp",EDGE,"E1467"),sQuery(id+"F0.wireOp",EDGE,"E1468"),sQuery(id+"F0.wireOp",EDGE,"E1469"),sQuery(id+"F0.wireOp",EDGE,"E1470"),sQuery(id+"F0.wireOp",EDGE,"E1471"),sQuery(id+"F0.wireOp",EDGE,"E1472"),sQuery(id+"F0.wireOp",EDGE,"E1473"),sQuery(id+"F0.wireOp",EDGE,"E1474"),sQuery(id+"F0.wireOp",EDGE,"E1475"),sQuery(id+"F0.wireOp",EDGE,"E1476"),sQuery(id+"F0.wireOp",EDGE,"E1477"),sQuery(id+"F0.wireOp",EDGE,"E1478"),sQuery(id+"F0.wireOp",EDGE,"E1479"),sQuery(id+"F0.wireOp",EDGE,"E1480"),sQuery(id+"F0.wireOp",EDGE,"E1481"),sQuery(id+"F0.wireOp",EDGE,"E1482"),sQuery(id+"F0.wireOp",EDGE,"E1483"),sQuery(id+"F0.wireOp",EDGE,"E1484"),sQuery(id+"F0.wireOp",EDGE,"E1485"),sQuery(id+"F0.wireOp",EDGE,"E1486"),sQuery(id+"F0.wireOp",EDGE,"E1487"),sQuery(id+"F0.wireOp",EDGE,"E1488"),sQuery(id+"F0.wireOp",EDGE,"E1489"),sQuery(id+"F0.wireOp",EDGE,"E1490"),sQuery(id+"F0.wireOp",EDGE,"E1491"),sQuery(id+"F0.wireOp",EDGE,"E1492"),sQuery(id+"F0.wireOp",EDGE,"E1493"),sQuery(id+"F0.wireOp",EDGE,"E1494"),sQuery(id+"F0.wireOp",EDGE,"E1495"),sQuery(id+"F0.wireOp",EDGE,"E1496"),sQuery(id+"F0.wireOp",EDGE,"E1497"),sQuery(id+"F0.wireOp",EDGE,"E1498"),sQuery(id+"F0.wireOp",EDGE,"E1499"),sQuery(id+"F0.wireOp",EDGE,"E1500"),sQuery(id+"F0.wireOp",EDGE,"E1501"),sQuery(id+"F0.wireOp",EDGE,"E1502"),sQuery(id+"F0.wireOp",EDGE,"E1503"),sQuery(id+"F0.wireOp",EDGE,"E1504"),sQuery(id+"F0.wireOp",EDGE,"E1505"),sQuery(id+"F0.wireOp",EDGE,"E1506"),sQuery(id+"F0.wireOp",EDGE,"E1507"),sQuery(id+"F0.wireOp",EDGE,"E1508"),sQuery(id+"F0.wireOp",EDGE,"E1509"),sQuery(id+"F0.wireOp",EDGE,"E1510"),sQuery(id+"F0.wireOp",EDGE,"E1511"),sQuery(id+"F0.wireOp",EDGE,"E1512"),sQuery(id+"F0.wireOp",EDGE,"E1513"),sQuery(id+"F0.wireOp",EDGE,"E1514"),sQuery(id+"F0.wireOp",EDGE,"E1515"),sQuery(id+"F0.wireOp",EDGE,"E1516"),sQuery(id+"F0.wireOp",EDGE,"E1517"),sQuery(id+"F0.wireOp",EDGE,"E1518"),sQuery(id+"F0.wireOp",EDGE,"E1519"),sQuery(id+"F0.wireOp",EDGE,"E1520"),sQuery(id+"F0.wireOp",EDGE,"E1521"),sQuery(id+"F0.wireOp",EDGE,"E1522"),sQuery(id+"F0.wireOp",EDGE,"E1523"),sQuery(id+"F0.wireOp",EDGE,"E1524"),sQuery(id+"F0.wireOp",EDGE,"E1525"),sQuery(id+"F0.wireOp",EDGE,"E1526"),sQuery(id+"F0.wireOp",EDGE,"E1527"),sQuery(id+"F0.wireOp",EDGE,"E1528"),sQuery(id+"F0.wireOp",EDGE,"E1529"),sQuery(id+"F0.wireOp",EDGE,"E1530"),sQuery(id+"F0.wireOp",EDGE,"E1531"),sQuery(id+"F0.wireOp",EDGE,"E1532"),sQuery(id+"F0.wireOp",EDGE,"E1533"),sQuery(id+"F0.wireOp",EDGE,"E1534"),sQuery(id+"F0.wireOp",EDGE,"E1535"),sQuery(id+"F0.wireOp",EDGE,"E1536"),sQuery(id+"F0.wireOp",EDGE,"E1537"),sQuery(id+"F0.wireOp",EDGE,"E1538"),sQuery(id+"F0.wireOp",EDGE,"E1539"),sQuery(id+"F0.wireOp",EDGE,"E1540"),sQuery(id+"F0.wireOp",EDGE,"E1541"),sQuery(id+"F0.wireOp",EDGE,"E1542"),sQuery(id+"F0.wireOp",EDGE,"E1543"),sQuery(id+"F0.wireOp",EDGE,"E1544"),sQuery(id+"F0.wireOp",EDGE,"E1545"),sQuery(id+"F0.wireOp",EDGE,"E1546"),sQuery(id+"F0.wireOp",EDGE,"E1547"),sQuery(id+"F0.wireOp",EDGE,"E1548"),sQuery(id+"F0.wireOp",EDGE,"E1549"),sQuery(id+"F0.wireOp",EDGE,"E1550"),sQuery(id+"F0.wireOp",EDGE,"E1551"),sQuery(id+"F0.wireOp",EDGE,"E1552"),sQuery(id+"F0.wireOp",EDGE,"E1553"),sQuery(id+"F0.wireOp",EDGE,"E1554"),sQuery(id+"F0.wireOp",EDGE,"E1555"),sQuery(id+"F0.wireOp",EDGE,"E1556"),sQuery(id+"F0.wireOp",EDGE,"E1557"),sQuery(id+"F0.wireOp",EDGE,"E1558"),sQuery(id+"F0.wireOp",EDGE,"E1559"),sQuery(id+"F0.wireOp",EDGE,"E1560"),sQuery(id+"F0.wireOp",EDGE,"E1561"),sQuery(id+"F0.wireOp",EDGE,"E1562"),sQuery(id+"F0.wireOp",EDGE,"E1563"),sQuery(id+"F0.wireOp",EDGE,"E1564"),sQuery(id+"F0.wireOp",EDGE,"E1565"),sQuery(id+"F0.wireOp",EDGE,"E1566"),sQuery(id+"F0.wireOp",EDGE,"E1567"),sQuery(id+"F0.wireOp",EDGE,"E1568"),sQuery(id+"F0.wireOp",EDGE,"E1569"),sQuery(id+"F0.wireOp",EDGE,"E1570"),sQuery(id+"F0.wireOp",EDGE,"E1571"),sQuery(id+"F0.wireOp",EDGE,"E1572"),sQuery(id+"F0.wireOp",EDGE,"E1573"),sQuery(id+"F0.wireOp",EDGE,"E1574"),sQuery(id+"F0.wireOp",EDGE,"E1575"),sQuery(id+"F0.wireOp",EDGE,"E1576"),sQuery(id+"F0.wireOp",EDGE,"E1577"),sQuery(id+"F0.wireOp",EDGE,"E1578"),sQuery(id+"F0.wireOp",EDGE,"E1579"),sQuery(id+"F0.wireOp",EDGE,"E1580"),sQuery(id+"F0.wireOp",EDGE,"E1581"),sQuery(id+"F0.wireOp",EDGE,"E1582"),sQuery(id+"F0.wireOp",EDGE,"E1583"),sQuery(id+"F0.wireOp",EDGE,"E1584"),sQuery(id+"F0.wireOp",EDGE,"E1585"),sQuery(id+"F0.wireOp",EDGE,"E1586"),sQuery(id+"F0.wireOp",EDGE,"E1587"),sQuery(id+"F0.wireOp",EDGE,"E1588"),sQuery(id+"F0.wireOp",EDGE,"E1589"),sQuery(id+"F0.wireOp",EDGE,"E1590"),sQuery(id+"F0.wireOp",EDGE,"E1591"),sQuery(id+"F0.wireOp",EDGE,"E1592"),sQuery(id+"F0.wireOp",EDGE,"E1593"),sQuery(id+"F0.wireOp",EDGE,"E1594"),sQuery(id+"F0.wireOp",EDGE,"E1595"),sQuery(id+"F0.wireOp",EDGE,"E1596"),sQuery(id+"F0.wireOp",EDGE,"E1597"),sQuery(id+"F0.wireOp",EDGE,"E1598"),sQuery(id+"F0.wireOp",EDGE,"E1599"),sQuery(id+"F0.wireOp",EDGE,"E1600"),sQuery(id+"F0.wireOp",EDGE,"E1601"),sQuery(id+"F0.wireOp",EDGE,"E1602"),sQuery(id+"F0.wireOp",EDGE,"E1603"),sQuery(id+"F0.wireOp",EDGE,"E1604"),sQuery(id+"F0.wireOp",EDGE,"E1605"),sQuery(id+"F0.wireOp",EDGE,"E1606"),sQuery(id+"F0.wireOp",EDGE,"E1607"),sQuery(id+"F0.wireOp",EDGE,"E1608"),sQuery(id+"F0.wireOp",EDGE,"E1609"),sQuery(id+"F0.wireOp",EDGE,"E1610"),sQuery(id+"F0.wireOp",EDGE,"E1611"),sQuery(id+"F0.wireOp",EDGE,"E1612"),sQuery(id+"F0.wireOp",EDGE,"E1613"),sQuery(id+"F0.wireOp",EDGE,"E1614"),sQuery(id+"F0.wireOp",EDGE,"E1615"),sQuery(id+"F0.wireOp",EDGE,"E1616"),sQuery(id+"F0.wireOp",EDGE,"E1617"),sQuery(id+"F0.wireOp",EDGE,"E1618"),sQuery(id+"F0.wireOp",EDGE,"E1619"),sQuery(id+"F0.wireOp",EDGE,"E1620"),sQuery(id+"F0.wireOp",EDGE,"E1621"),sQuery(id+"F0.wireOp",EDGE,"E1622"),sQuery(id+"F0.wireOp",EDGE,"E1623"),sQuery(id+"F0.wireOp",EDGE,"E1624"),sQuery(id+"F0.wireOp",EDGE,"E1625"),sQuery(id+"F0.wireOp",EDGE,"E1626"),sQuery(id+"F0.wireOp",EDGE,"E1627"),sQuery(id+"F0.wireOp",EDGE,"E1628"),sQuery(id+"F0.wireOp",EDGE,"E1629"),sQuery(id+"F0.wireOp",EDGE,"E1630"),sQuery(id+"F0.wireOp",EDGE,"E1631"),sQuery(id+"F0.wireOp",EDGE,"E1632"),sQuery(id+"F0.wireOp",EDGE,"E1633"),sQuery(id+"F0.wireOp",EDGE,"E1634"),sQuery(id+"F0.wireOp",EDGE,"E1635"),sQuery(id+"F0.wireOp",EDGE,"E1636"),sQuery(id+"F0.wireOp",EDGE,"E1637"),sQuery(id+"F0.wireOp",EDGE,"E1638"),sQuery(id+"F0.wireOp",EDGE,"E1639"),sQuery(id+"F0.wireOp",EDGE,"E1640"),sQuery(id+"F0.wireOp",EDGE,"E1641"),sQuery(id+"F0.wireOp",EDGE,"E1642"),sQuery(id+"F0.wireOp",EDGE,"E1643"),sQuery(id+"F0.wireOp",EDGE,"E1644"),sQuery(id+"F0.wireOp",EDGE,"E1645"),sQuery(id+"F0.wireOp",EDGE,"E1646"),sQuery(id+"F0.wireOp",EDGE,"E1647"),sQuery(id+"F0.wireOp",EDGE,"E1648"),sQuery(id+"F0.wireOp",EDGE,"E1649"),sQuery(id+"F0.wireOp",EDGE,"E1650"),sQuery(id+"F0.wireOp",EDGE,"E1651"),sQuery(id+"F0.wireOp",EDGE,"E1652"),sQuery(id+"F0.wireOp",EDGE,"E1653"),sQuery(id+"F0.wireOp",EDGE,"E1654"),sQuery(id+"F0.wireOp",EDGE,"E1655"),sQuery(id+"F0.wireOp",EDGE,"E1656"),sQuery(id+"F0.wireOp",EDGE,"E1657"),sQuery(id+"F0.wireOp",EDGE,"E1658"),sQuery(id+"F0.wireOp",EDGE,"E1659"),sQuery(id+"F0.wireOp",EDGE,"E1660"),sQuery(id+"F0.wireOp",EDGE,"E1661"),sQuery(id+"F0.wireOp",EDGE,"E1662"),sQuery(id+"F0.wireOp",EDGE,"E1663"),sQuery(id+"F0.wireOp",EDGE,"E1664"),sQuery(id+"F0.wireOp",EDGE,"E1665"),sQuery(id+"F0.wireOp",EDGE,"E1666"),sQuery(id+"F0.wireOp",EDGE,"E1667"),sQuery(id+"F0.wireOp",EDGE,"E1668"),sQuery(id+"F0.wireOp",EDGE,"E1669"),sQuery(id+"F0.wireOp",EDGE,"E1670"),sQuery(id+"F0.wireOp",EDGE,"E1671"),sQuery(id+"F0.wireOp",EDGE,"E1672"),sQuery(id+"F0.wireOp",EDGE,"E1673"),sQuery(id+"F0.wireOp",EDGE,"E1674"),sQuery(id+"F0.wireOp",EDGE,"E1675"),sQuery(id+"F0.wireOp",EDGE,"E1676"),sQuery(id+"F0.wireOp",EDGE,"E1677"),sQuery(id+"F0.wireOp",EDGE,"E1678"),sQuery(id+"F0.wireOp",EDGE,"E1679"),sQuery(id+"F0.wireOp",EDGE,"E1680"),sQuery(id+"F0.wireOp",EDGE,"E1681"),sQuery(id+"F0.wireOp",EDGE,"E1682"),sQuery(id+"F0.wireOp",EDGE,"E1683"),sQuery(id+"F0.wireOp",EDGE,"E1684"),sQuery(id+"F0.wireOp",EDGE,"E1685"),sQuery(id+"F0.wireOp",EDGE,"E1686"),sQuery(id+"F0.wireOp",EDGE,"E1687"),sQuery(id+"F0.wireOp",EDGE,"E1688"),sQuery(id+"F0.wireOp",EDGE,"E1689"),sQuery(id+"F0.wireOp",EDGE,"E1690"),sQuery(id+"F0.wireOp",EDGE,"E1691"),sQuery(id+"F0.wireOp",EDGE,"E1692"),sQuery(id+"F0.wireOp",EDGE,"E1693"),sQuery(id+"F0.wireOp",EDGE,"E1694"),sQuery(id+"F0.wireOp",EDGE,"E1695"),sQuery(id+"F0.wireOp",EDGE,"E1696"),sQuery(id+"F0.wireOp",EDGE,"E1697"),sQuery(id+"F0.wireOp",EDGE,"E1698"),sQuery(id+"F0.wireOp",EDGE,"E1699"),sQuery(id+"F0.wireOp",EDGE,"E1700"),sQuery(id+"F0.wireOp",EDGE,"E1701"),sQuery(id+"F0.wireOp",EDGE,"E1702"),sQuery(id+"F0.wireOp",EDGE,"E1703"),sQuery(id+"F0.wireOp",EDGE,"E1704"),sQuery(id+"F0.wireOp",EDGE,"E1705"),sQuery(id+"F0.wireOp",EDGE,"E1706"),sQuery(id+"F0.wireOp",EDGE,"E1707"),sQuery(id+"F0.wireOp",EDGE,"E1708"),sQuery(id+"F0.wireOp",EDGE,"E1709"),sQuery(id+"F0.wireOp",EDGE,"E1710"),sQuery(id+"F0.wireOp",EDGE,"E1711"),sQuery(id+"F0.wireOp",EDGE,"E1712"),sQuery(id+"F0.wireOp",EDGE,"E1713"),sQuery(id+"F0.wireOp",EDGE,"E1714"),sQuery(id+"F0.wireOp",EDGE,"E1715"),sQuery(id+"F0.wireOp",EDGE,"E1716"),sQuery(id+"F0.wireOp",EDGE,"E1717"),sQuery(id+"F0.wireOp",EDGE,"E1718"),sQuery(id+"F0.wireOp",EDGE,"E1719"),sQuery(id+"F0.wireOp",EDGE,"E1720"),sQuery(id+"F0.wireOp",EDGE,"E1721"),sQuery(id+"F0.wireOp",EDGE,"E1722"),sQuery(id+"F0.wireOp",EDGE,"E1723"),sQuery(id+"F0.wireOp",EDGE,"E1724"),sQuery(id+"F0.wireOp",EDGE,"E1725"),sQuery(id+"F0.wireOp",EDGE,"E1726"),sQuery(id+"F0.wireOp",EDGE,"E1727"),sQuery(id+"F0.wireOp",EDGE,"E1728"),sQuery(id+"F0.wireOp",EDGE,"E1729"),sQuery(id+"F0.wireOp",EDGE,"E1730"),sQuery(id+"F0.wireOp",EDGE,"E1731"),sQuery(id+"F0.wireOp",EDGE,"E1732"),sQuery(id+"F0.wireOp",EDGE,"E1733"),sQuery(id+"F0.wireOp",EDGE,"E1734"),sQuery(id+"F0.wireOp",EDGE,"E1735"),sQuery(id+"F0.wireOp",EDGE,"E1736"),sQuery(id+"F0.wireOp",EDGE,"E1737"),sQuery(id+"F0.wireOp",EDGE,"E1738"),sQuery(id+"F0.wireOp",EDGE,"E1739"),sQuery(id+"F0.wireOp",EDGE,"E1740"),sQuery(id+"F0.wireOp",EDGE,"E1741"),sQuery(id+"F0.wireOp",EDGE,"E1742"),sQuery(id+"F0.wireOp",EDGE,"E1743"),sQuery(id+"F0.wireOp",EDGE,"E1744"),sQuery(id+"F0.wireOp",EDGE,"E1745"),sQuery(id+"F0.wireOp",EDGE,"E1746"),sQuery(id+"F0.wireOp",EDGE,"E1747"),sQuery(id+"F0.wireOp",EDGE,"E1748"),sQuery(id+"F0.wireOp",EDGE,"E1749"),sQuery(id+"F0.wireOp",EDGE,"E1750"),sQuery(id+"F0.wireOp",EDGE,"E1751"),sQuery(id+"F0.wireOp",EDGE,"E1752"),sQuery(id+"F0.wireOp",EDGE,"E1753"),sQuery(id+"F0.wireOp",EDGE,"E1754"),sQuery(id+"F0.wireOp",EDGE,"E1755"),sQuery(id+"F0.wireOp",EDGE,"E1756"),sQuery(id+"F0.wireOp",EDGE,"E1757"),sQuery(id+"F0.wireOp",EDGE,"E1758"),sQuery(id+"F0.wireOp",EDGE,"E1759"),sQuery(id+"F0.wireOp",EDGE,"E1760"),sQuery(id+"F0.wireOp",EDGE,"E1761"),sQuery(id+"F0.wireOp",EDGE,"E1762"),sQuery(id+"F0.wireOp",EDGE,"E1763"),sQuery(id+"F0.wireOp",EDGE,"E1764"),sQuery(id+"F0.wireOp",EDGE,"E1765"),sQuery(id+"F0.wireOp",EDGE,"E1766"),sQuery(id+"F0.wireOp",EDGE,"E1767"),sQuery(id+"F0.wireOp",EDGE,"E1768"),sQuery(id+"F0.wireOp",EDGE,"E1769"),sQuery(id+"F0.wireOp",EDGE,"E1770"),sQuery(id+"F0.wireOp",EDGE,"E1771"),sQuery(id+"F0.wireOp",EDGE,"E1772"),sQuery(id+"F0.wireOp",EDGE,"E1773"),sQuery(id+"F0.wireOp",EDGE,"E1774"),sQuery(id+"F0.wireOp",EDGE,"E1775"),sQuery(id+"F0.wireOp",EDGE,"E1776"),sQuery(id+"F0.wireOp",EDGE,"E1777"),sQuery(id+"F0.wireOp",EDGE,"E1778"),sQuery(id+"F0.wireOp",EDGE,"E1779"),sQuery(id+"F0.wireOp",EDGE,"E1780"),sQuery(id+"F0.wireOp",EDGE,"E1781"),sQuery(id+"F0.wireOp",EDGE,"E1782"),sQuery(id+"F0.wireOp",EDGE,"E1783"),sQuery(id+"F0.wireOp",EDGE,"E1784"),sQuery(id+"F0.wireOp",EDGE,"E1785"),sQuery(id+"F0.wireOp",EDGE,"E1786"),sQuery(id+"F0.wireOp",EDGE,"E1787"),sQuery(id+"F0.wireOp",EDGE,"E1788"),sQuery(id+"F0.wireOp",EDGE,"E1789"),sQuery(id+"F0.wireOp",EDGE,"E1790")])],"isStart":false});
            var sketch = newSketch(context, id + "F2", { "sketchPlane" : qUnion([Q0])});
            skCircle(sketch, "E1791", {"center": v(-35.95, -101.17) * mm, "radius": 28.58 * mm});
            skCircle(sketch, "E1792", {"center": v(60.05, -54.02) * mm, "radius": 28.58 * mm});
            skCircle(sketch, "E1793", {"center": v(25.18, 79.3) * mm, "radius": 28.58 * mm});
            skCircle(sketch, "E1794", {"center": v(-52.6, 18.64) * mm, "radius": 28.58 * mm});
            skSolve(sketch);
        }
        {
            var Q0;
            Q0 = qSketchRegion(id + "F2", true);
            extrude(context, id + "F3", {"entities" : qUnion([Q0]), "operationType" : NewBodyOperationType.REMOVE, "endBound" : BoundingType.THROUGH_ALL, "oppositeDirection" : true, "depth" : 25.4 * mm});
        }
    });
